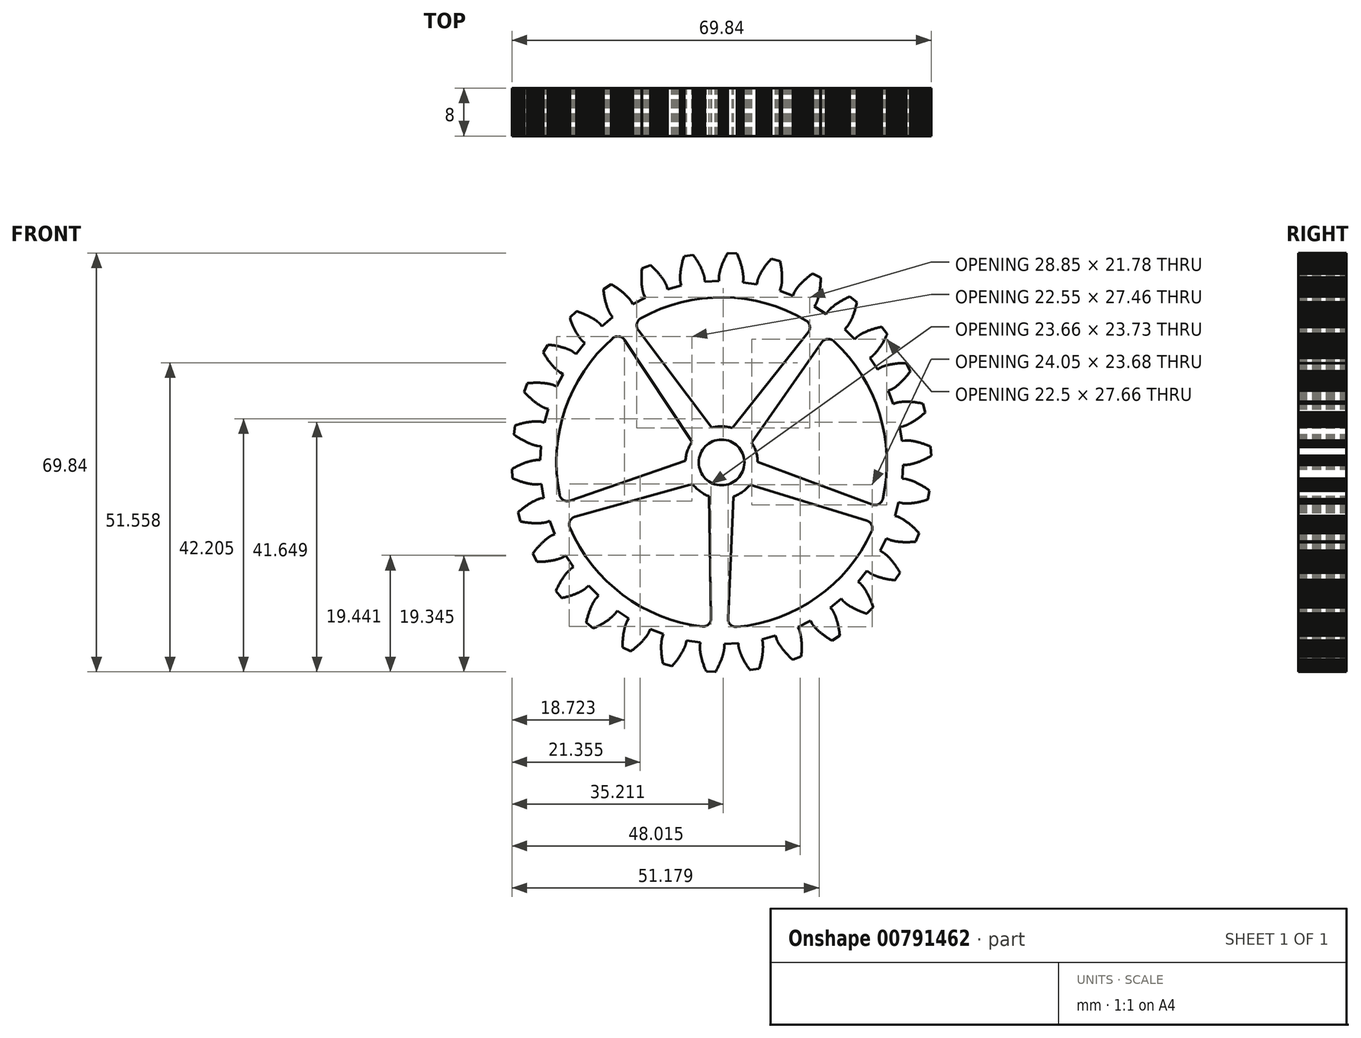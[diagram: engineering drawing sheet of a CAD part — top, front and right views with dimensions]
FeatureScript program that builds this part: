
annotation { "Feature Type Name" : "Feature", "Feature Type Description" : "" }
export const myFeature = defineFeature(function(context is Context, id is Id, definition is map)
    precondition{}
    {
        {
            var Q0;
            Q0=qCreatedBy(makeId("Front.planeOp"),FACE);
            var sketch = newSketch(context, id + "F0", { "sketchPlane" : qUnion([Q0])});
            skCircle(sketch, "E0", {"center": v(0, 0) * mm, "radius": 32.75 * mm, "construction": true});
            skArc(sketch, "E1", {"start": v(26.86, -6.05) * mm, "mid": v(26.3, 8.17) * mm, "end": v(18.7, 20.2) * mm});
            skLineSegment(sketch, "E2", {"start": v(-1.73, -25.97) * mm, "end": v(-2.1, -5.63) * mm});
            skLineSegment(sketch, "E3", {"start": v(1.07, -26) * mm, "end": v(1.95, -5.68) * mm});
            skLineSegment(sketch, "E4", {"start": v(24.16, -9.67) * mm, "end": v(4.7, -3.74) * mm});
            skLineSegment(sketch, "E5", {"start": v(25.06, -7.02) * mm, "end": v(6, 0.1) * mm});
            skLineSegment(sketch, "E6", {"start": v(16.67, 20) * mm, "end": v(5, 3.32) * mm});
            skLineSegment(sketch, "E7", {"start": v(14.42, 21.67) * mm, "end": v(1.76, 5.75) * mm});
            skLineSegment(sketch, "E8", {"start": v(-13.86, 22.03) * mm, "end": v(-1.61, 5.79) * mm});
            skLineSegment(sketch, "E9", {"start": v(-16.15, 20.41) * mm, "end": v(-4.92, 3.45) * mm});
            skLineSegment(sketch, "E10", {"start": v(-25.24, -6.38) * mm, "end": v(-6, 0.26) * mm});
            skLineSegment(sketch, "E11", {"start": v(-24.4, -9.05) * mm, "end": v(-4.8, -3.61) * mm});
            skArc(sketch, "E12", {"start": v(-3.25, -27.34) * mm, "mid": v(-2.18, -27) * mm, "end": v(-1.73, -25.97) * mm});
            skArc(sketch, "E13", {"start": v(1.07, -26) * mm, "mid": v(1.49, -27.05) * mm, "end": v(2.55, -27.41) * mm});
            skArc(sketch, "E14", {"start": v(-24.4, -9.05) * mm, "mid": v(-25.26, -9.77) * mm, "end": v(-25.29, -10.9) * mm});
            skArc(sketch, "E15", {"start": v(-27, -5.36) * mm, "mid": v(-26.35, -6.27) * mm, "end": v(-25.24, -6.38) * mm});
            skArc(sketch, "E16", {"start": v(-16.15, 20.41) * mm, "mid": v(-17.1, 21) * mm, "end": v(-18.17, 20.68) * mm});
            skArc(sketch, "E17", {"start": v(-13.44, 24.03) * mm, "mid": v(-14.1, 23.12) * mm, "end": v(-13.86, 22.03) * mm});
            skArc(sketch, "E18", {"start": v(14.42, 21.67) * mm, "mid": v(14.7, 22.75) * mm, "end": v(14.05, 23.67) * mm});
            skArc(sketch, "E19", {"start": v(18.7, 20.2) * mm, "mid": v(17.63, 20.56) * mm, "end": v(16.67, 20) * mm});
            skArc(sketch, "E20", {"start": v(25.06, -7.02) * mm, "mid": v(26.18, -6.94) * mm, "end": v(26.86, -6.05) * mm});
            skArc(sketch, "E21", {"start": v(25, -11.54) * mm, "mid": v(25, -10.42) * mm, "end": v(24.16, -9.67) * mm});
            skArc(sketch, "E22", {"start": v(2.55, -27.41) * mm, "mid": v(15.9, -22.48) * mm, "end": v(25, -11.54) * mm});
            skArc(sketch, "E23", {"start": v(-25.29, -10.9) * mm, "mid": v(-16.47, -22.06) * mm, "end": v(-3.25, -27.34) * mm});
            skArc(sketch, "E24", {"start": v(-18.17, 20.68) * mm, "mid": v(-26.07, 8.84) * mm, "end": v(-27, -5.36) * mm});
            skArc(sketch, "E25", {"start": v(14.05, 23.67) * mm, "mid": v(0.35, 27.53) * mm, "end": v(-13.44, 24.03) * mm});
            skCircle(sketch, "E26", {"center": v(0, 0) * mm, "radius": 3.8 * mm});
            skLineSegment(sketch, "E27", {"start": v(-30.24, 0.39) * mm, "end": v(-30.78, 0.4) * mm});
            skLineSegment(sketch, "E28", {"start": v(-30.78, 0.4) * mm, "end": v(-30.79, 0.4) * mm});
            skLineSegment(sketch, "E29", {"start": v(-30.79, 0.4) * mm, "end": v(-30.8, 0.4) * mm});
            skLineSegment(sketch, "E30", {"start": v(-30.8, 0.4) * mm, "end": v(-30.81, 0.4) * mm});
            skLineSegment(sketch, "E31", {"start": v(-30.81, 0.4) * mm, "end": v(-30.84, 0.4) * mm});
            skLineSegment(sketch, "E32", {"start": v(-30.84, 0.4) * mm, "end": v(-30.86, 0.4) * mm});
            skLineSegment(sketch, "E33", {"start": v(-30.86, 0.4) * mm, "end": v(-30.89, 0.39) * mm});
            skLineSegment(sketch, "E34", {"start": v(-30.89, 0.39) * mm, "end": v(-30.92, 0.39) * mm});
            skLineSegment(sketch, "E35", {"start": v(-30.92, 0.39) * mm, "end": v(-30.96, 0.38) * mm});
            skLineSegment(sketch, "E36", {"start": v(-30.96, 0.38) * mm, "end": v(-31, 0.38) * mm});
            skLineSegment(sketch, "E37", {"start": v(-31, 0.38) * mm, "end": v(-31.05, 0.37) * mm});
            skLineSegment(sketch, "E38", {"start": v(-31.05, 0.37) * mm, "end": v(-31.1, 0.37) * mm});
            skLineSegment(sketch, "E39", {"start": v(-31.1, 0.37) * mm, "end": v(-31.15, 0.36) * mm});
            skLineSegment(sketch, "E40", {"start": v(-31.15, 0.36) * mm, "end": v(-31.2, 0.35) * mm});
            skLineSegment(sketch, "E41", {"start": v(-31.2, 0.35) * mm, "end": v(-31.27, 0.34) * mm});
            skLineSegment(sketch, "E42", {"start": v(-31.27, 0.34) * mm, "end": v(-31.34, 0.33) * mm});
            skLineSegment(sketch, "E43", {"start": v(-31.34, 0.33) * mm, "end": v(-31.4, 0.32) * mm});
            skLineSegment(sketch, "E44", {"start": v(-31.4, 0.32) * mm, "end": v(-31.48, 0.3) * mm});
            skLineSegment(sketch, "E45", {"start": v(-31.48, 0.3) * mm, "end": v(-31.56, 0.29) * mm});
            skLineSegment(sketch, "E46", {"start": v(-31.56, 0.29) * mm, "end": v(-31.64, 0.27) * mm});
            skLineSegment(sketch, "E47", {"start": v(-31.64, 0.27) * mm, "end": v(-31.72, 0.25) * mm});
            skLineSegment(sketch, "E48", {"start": v(-31.72, 0.25) * mm, "end": v(-31.81, 0.23) * mm});
            skLineSegment(sketch, "E49", {"start": v(-31.81, 0.23) * mm, "end": v(-31.9, 0.2) * mm});
            skLineSegment(sketch, "E50", {"start": v(-31.9, 0.2) * mm, "end": v(-32, 0.17) * mm});
            skLineSegment(sketch, "E51", {"start": v(-32, 0.17) * mm, "end": v(-32.1, 0.15) * mm});
            skLineSegment(sketch, "E52", {"start": v(-32.1, 0.15) * mm, "end": v(-32.2, 0.12) * mm});
            skLineSegment(sketch, "E53", {"start": v(-32.2, 0.12) * mm, "end": v(-32.31, 0.08) * mm});
            skLineSegment(sketch, "E54", {"start": v(-32.31, 0.08) * mm, "end": v(-32.42, 0.05) * mm});
            skLineSegment(sketch, "E55", {"start": v(-32.42, 0.05) * mm, "end": v(-32.54, 0) * mm});
            skLineSegment(sketch, "E56", {"start": v(-32.54, 0) * mm, "end": v(-32.66, -0.03) * mm});
            skLineSegment(sketch, "E57", {"start": v(-32.66, -0.03) * mm, "end": v(-32.78, -0.08) * mm});
            skLineSegment(sketch, "E58", {"start": v(-32.78, -0.08) * mm, "end": v(-32.9, -0.12) * mm});
            skLineSegment(sketch, "E59", {"start": v(-32.9, -0.12) * mm, "end": v(-33.03, -0.17) * mm});
            skLineSegment(sketch, "E60", {"start": v(-33.03, -0.17) * mm, "end": v(-33.16, -0.23) * mm});
            skLineSegment(sketch, "E61", {"start": v(-33.16, -0.23) * mm, "end": v(-33.3, -0.28) * mm});
            skLineSegment(sketch, "E62", {"start": v(-33.3, -0.28) * mm, "end": v(-33.43, -0.34) * mm});
            skLineSegment(sketch, "E63", {"start": v(-33.43, -0.34) * mm, "end": v(-33.57, -0.4) * mm});
            skLineSegment(sketch, "E64", {"start": v(-33.57, -0.4) * mm, "end": v(-33.72, -0.47) * mm});
            skLineSegment(sketch, "E65", {"start": v(-33.72, -0.47) * mm, "end": v(-33.87, -0.54) * mm});
            skLineSegment(sketch, "E66", {"start": v(-33.87, -0.54) * mm, "end": v(-34.02, -0.61) * mm});
            skLineSegment(sketch, "E67", {"start": v(-34.02, -0.61) * mm, "end": v(-34.17, -0.7) * mm});
            skLineSegment(sketch, "E68", {"start": v(-34.17, -0.7) * mm, "end": v(-34.32, -0.77) * mm});
            skLineSegment(sketch, "E69", {"start": v(-34.32, -0.77) * mm, "end": v(-34.48, -0.85) * mm});
            skLineSegment(sketch, "E70", {"start": v(-34.48, -0.85) * mm, "end": v(-34.64, -0.94) * mm});
            skLineSegment(sketch, "E71", {"start": v(-34.64, -0.94) * mm, "end": v(-34.8, -1.03) * mm});
            skLineSegment(sketch, "E72", {"start": v(-34.8, -1.03) * mm, "end": v(-34.92, -1.13) * mm});
            skLineSegment(sketch, "E73", {"start": v(-34.92, -1.13) * mm, "end": v(-34.84, -2.6) * mm});
            skLineSegment(sketch, "E74", {"start": v(-34.84, -2.6) * mm, "end": v(-34.72, -2.68) * mm});
            skLineSegment(sketch, "E75", {"start": v(-34.72, -2.68) * mm, "end": v(-34.55, -2.76) * mm});
            skLineSegment(sketch, "E76", {"start": v(-34.55, -2.76) * mm, "end": v(-34.38, -2.83) * mm});
            skLineSegment(sketch, "E77", {"start": v(-34.38, -2.83) * mm, "end": v(-34.21, -2.9) * mm});
            skLineSegment(sketch, "E78", {"start": v(-34.21, -2.9) * mm, "end": v(-34.05, -2.96) * mm});
            skLineSegment(sketch, "E79", {"start": v(-34.05, -2.96) * mm, "end": v(-33.89, -3.02) * mm});
            skLineSegment(sketch, "E80", {"start": v(-33.89, -3.02) * mm, "end": v(-33.73, -3.07) * mm});
            skLineSegment(sketch, "E81", {"start": v(-33.73, -3.07) * mm, "end": v(-33.58, -3.13) * mm});
            skLineSegment(sketch, "E82", {"start": v(-33.58, -3.13) * mm, "end": v(-33.43, -3.18) * mm});
            skLineSegment(sketch, "E83", {"start": v(-33.43, -3.18) * mm, "end": v(-33.28, -3.22) * mm});
            skLineSegment(sketch, "E84", {"start": v(-33.28, -3.22) * mm, "end": v(-33.14, -3.27) * mm});
            skLineSegment(sketch, "E85", {"start": v(-33.14, -3.27) * mm, "end": v(-33, -3.3) * mm});
            skLineSegment(sketch, "E86", {"start": v(-33, -3.3) * mm, "end": v(-32.86, -3.35) * mm});
            skLineSegment(sketch, "E87", {"start": v(-32.86, -3.35) * mm, "end": v(-32.73, -3.38) * mm});
            skLineSegment(sketch, "E88", {"start": v(-32.73, -3.38) * mm, "end": v(-32.6, -3.42) * mm});
            skLineSegment(sketch, "E89", {"start": v(-32.6, -3.42) * mm, "end": v(-32.47, -3.45) * mm});
            skLineSegment(sketch, "E90", {"start": v(-32.47, -3.45) * mm, "end": v(-32.35, -3.48) * mm});
            skLineSegment(sketch, "E91", {"start": v(-32.35, -3.48) * mm, "end": v(-32.23, -3.5) * mm});
            skLineSegment(sketch, "E92", {"start": v(-32.23, -3.5) * mm, "end": v(-32.12, -3.53) * mm});
            skLineSegment(sketch, "E93", {"start": v(-32.12, -3.53) * mm, "end": v(-32, -3.55) * mm});
            skLineSegment(sketch, "E94", {"start": v(-32, -3.55) * mm, "end": v(-31.9, -3.57) * mm});
            skLineSegment(sketch, "E95", {"start": v(-31.9, -3.57) * mm, "end": v(-31.8, -3.58) * mm});
            skLineSegment(sketch, "E96", {"start": v(-31.8, -3.58) * mm, "end": v(-31.7, -3.6) * mm});
            skLineSegment(sketch, "E97", {"start": v(-31.7, -3.6) * mm, "end": v(-31.6, -3.61) * mm});
            skLineSegment(sketch, "E98", {"start": v(-31.6, -3.61) * mm, "end": v(-31.52, -3.63) * mm});
            skLineSegment(sketch, "E99", {"start": v(-31.52, -3.63) * mm, "end": v(-31.43, -3.64) * mm});
            skLineSegment(sketch, "E100", {"start": v(-31.43, -3.64) * mm, "end": v(-31.35, -3.65) * mm});
            skLineSegment(sketch, "E101", {"start": v(-31.35, -3.65) * mm, "end": v(-31.27, -3.66) * mm});
            skLineSegment(sketch, "E102", {"start": v(-31.27, -3.66) * mm, "end": v(-31.2, -3.66) * mm});
            skLineSegment(sketch, "E103", {"start": v(-31.2, -3.66) * mm, "end": v(-31.12, -3.67) * mm});
            skLineSegment(sketch, "E104", {"start": v(-31.12, -3.67) * mm, "end": v(-31.06, -3.67) * mm});
            skLineSegment(sketch, "E105", {"start": v(-31.06, -3.67) * mm, "end": v(-31, -3.68) * mm});
            skLineSegment(sketch, "E106", {"start": v(-31, -3.68) * mm, "end": v(-30.93, -3.68) * mm});
            skLineSegment(sketch, "E107", {"start": v(-30.93, -3.68) * mm, "end": v(-30.88, -3.68) * mm});
            skLineSegment(sketch, "E108", {"start": v(-30.88, -3.68) * mm, "end": v(-30.83, -3.68) * mm});
            skLineSegment(sketch, "E109", {"start": v(-30.83, -3.68) * mm, "end": v(-30.78, -3.68) * mm});
            skLineSegment(sketch, "E110", {"start": v(-30.78, -3.68) * mm, "end": v(-30.74, -3.68) * mm});
            skLineSegment(sketch, "E111", {"start": v(-30.74, -3.68) * mm, "end": v(-30.7, -3.68) * mm});
            skLineSegment(sketch, "E112", {"start": v(-30.7, -3.68) * mm, "end": v(-30.67, -3.68) * mm});
            skLineSegment(sketch, "E113", {"start": v(-30.67, -3.68) * mm, "end": v(-30.64, -3.68) * mm});
            skLineSegment(sketch, "E114", {"start": v(-30.64, -3.68) * mm, "end": v(-30.62, -3.68) * mm});
            skLineSegment(sketch, "E115", {"start": v(-30.62, -3.68) * mm, "end": v(-30.6, -3.68) * mm});
            skLineSegment(sketch, "E116", {"start": v(-30.6, -3.68) * mm, "end": v(-30.58, -3.68) * mm});
            skLineSegment(sketch, "E117", {"start": v(-30.58, -3.68) * mm, "end": v(-30.57, -3.67) * mm});
            skLineSegment(sketch, "E118", {"start": v(-30.57, -3.67) * mm, "end": v(-30.56, -3.67) * mm});
            skLineSegment(sketch, "E119", {"start": v(-30.56, -3.67) * mm, "end": v(-30.02, -3.6) * mm});
            skLineSegment(sketch, "E120", {"start": v(-30.02, -3.6) * mm, "end": v(-29.66, -5.9) * mm});
            skLineSegment(sketch, "E121", {"start": v(-29.66, -5.9) * mm, "end": v(-30.19, -6.01) * mm});
            skLineSegment(sketch, "E122", {"start": v(-30.19, -6.01) * mm, "end": v(-30.2, -6.01) * mm});
            skLineSegment(sketch, "E123", {"start": v(-30.2, -6.01) * mm, "end": v(-30.2, -6.02) * mm});
            skLineSegment(sketch, "E124", {"start": v(-30.2, -6.02) * mm, "end": v(-30.22, -6.02) * mm});
            skLineSegment(sketch, "E125", {"start": v(-30.22, -6.02) * mm, "end": v(-30.24, -6.03) * mm});
            skLineSegment(sketch, "E126", {"start": v(-30.24, -6.03) * mm, "end": v(-30.27, -6.03) * mm});
            skLineSegment(sketch, "E127", {"start": v(-30.27, -6.03) * mm, "end": v(-30.3, -6.04) * mm});
            skLineSegment(sketch, "E128", {"start": v(-30.3, -6.04) * mm, "end": v(-30.33, -6.05) * mm});
            skLineSegment(sketch, "E129", {"start": v(-30.33, -6.05) * mm, "end": v(-30.36, -6.06) * mm});
            skLineSegment(sketch, "E130", {"start": v(-30.36, -6.06) * mm, "end": v(-30.4, -6.07) * mm});
            skLineSegment(sketch, "E131", {"start": v(-30.4, -6.07) * mm, "end": v(-30.45, -6.09) * mm});
            skLineSegment(sketch, "E132", {"start": v(-30.45, -6.09) * mm, "end": v(-30.5, -6.1) * mm});
            skLineSegment(sketch, "E133", {"start": v(-30.5, -6.1) * mm, "end": v(-30.54, -6.12) * mm});
            skLineSegment(sketch, "E134", {"start": v(-30.54, -6.12) * mm, "end": v(-30.6, -6.15) * mm});
            skLineSegment(sketch, "E135", {"start": v(-30.6, -6.15) * mm, "end": v(-30.66, -6.17) * mm});
            skLineSegment(sketch, "E136", {"start": v(-30.66, -6.17) * mm, "end": v(-30.72, -6.2) * mm});
            skLineSegment(sketch, "E137", {"start": v(-30.72, -6.2) * mm, "end": v(-30.78, -6.22) * mm});
            skLineSegment(sketch, "E138", {"start": v(-30.78, -6.22) * mm, "end": v(-30.85, -6.25) * mm});
            skLineSegment(sketch, "E139", {"start": v(-30.85, -6.25) * mm, "end": v(-30.93, -6.28) * mm});
            skLineSegment(sketch, "E140", {"start": v(-30.93, -6.28) * mm, "end": v(-31, -6.32) * mm});
            skLineSegment(sketch, "E141", {"start": v(-31, -6.32) * mm, "end": v(-31.08, -6.35) * mm});
            skLineSegment(sketch, "E142", {"start": v(-31.08, -6.35) * mm, "end": v(-31.16, -6.4) * mm});
            skLineSegment(sketch, "E143", {"start": v(-31.16, -6.4) * mm, "end": v(-31.25, -6.44) * mm});
            skLineSegment(sketch, "E144", {"start": v(-31.25, -6.44) * mm, "end": v(-31.34, -6.48) * mm});
            skLineSegment(sketch, "E145", {"start": v(-31.34, -6.48) * mm, "end": v(-31.43, -6.53) * mm});
            skLineSegment(sketch, "E146", {"start": v(-31.43, -6.53) * mm, "end": v(-31.52, -6.58) * mm});
            skLineSegment(sketch, "E147", {"start": v(-31.52, -6.58) * mm, "end": v(-31.62, -6.64) * mm});
            skLineSegment(sketch, "E148", {"start": v(-31.62, -6.64) * mm, "end": v(-31.72, -6.7) * mm});
            skLineSegment(sketch, "E149", {"start": v(-31.72, -6.7) * mm, "end": v(-31.83, -6.76) * mm});
            skLineSegment(sketch, "E150", {"start": v(-31.83, -6.76) * mm, "end": v(-31.93, -6.82) * mm});
            skLineSegment(sketch, "E151", {"start": v(-31.93, -6.82) * mm, "end": v(-32.04, -6.9) * mm});
            skLineSegment(sketch, "E152", {"start": v(-32.04, -6.9) * mm, "end": v(-32.16, -6.96) * mm});
            skLineSegment(sketch, "E153", {"start": v(-32.16, -6.96) * mm, "end": v(-32.27, -7.04) * mm});
            skLineSegment(sketch, "E154", {"start": v(-32.27, -7.04) * mm, "end": v(-32.39, -7.12) * mm});
            skLineSegment(sketch, "E155", {"start": v(-32.39, -7.12) * mm, "end": v(-32.5, -7.2) * mm});
            skLineSegment(sketch, "E156", {"start": v(-32.5, -7.2) * mm, "end": v(-32.63, -7.29) * mm});
            skLineSegment(sketch, "E157", {"start": v(-32.63, -7.29) * mm, "end": v(-32.76, -7.38) * mm});
            skLineSegment(sketch, "E158", {"start": v(-32.76, -7.38) * mm, "end": v(-32.88, -7.47) * mm});
            skLineSegment(sketch, "E159", {"start": v(-32.88, -7.47) * mm, "end": v(-33.01, -7.57) * mm});
            skLineSegment(sketch, "E160", {"start": v(-33.01, -7.57) * mm, "end": v(-33.14, -7.67) * mm});
            skLineSegment(sketch, "E161", {"start": v(-33.14, -7.67) * mm, "end": v(-33.28, -7.78) * mm});
            skLineSegment(sketch, "E162", {"start": v(-33.28, -7.78) * mm, "end": v(-33.41, -7.89) * mm});
            skLineSegment(sketch, "E163", {"start": v(-33.41, -7.89) * mm, "end": v(-33.55, -8) * mm});
            skLineSegment(sketch, "E164", {"start": v(-33.55, -8) * mm, "end": v(-33.69, -8.12) * mm});
            skLineSegment(sketch, "E165", {"start": v(-33.69, -8.12) * mm, "end": v(-33.83, -8.25) * mm});
            skLineSegment(sketch, "E166", {"start": v(-33.83, -8.25) * mm, "end": v(-33.92, -8.36) * mm});
            skLineSegment(sketch, "E167", {"start": v(-33.92, -8.36) * mm, "end": v(-33.53, -9.79) * mm});
            skLineSegment(sketch, "E168", {"start": v(-33.53, -9.79) * mm, "end": v(-33.4, -9.84) * mm});
            skLineSegment(sketch, "E169", {"start": v(-33.4, -9.84) * mm, "end": v(-33.22, -9.88) * mm});
            skLineSegment(sketch, "E170", {"start": v(-33.22, -9.88) * mm, "end": v(-33.04, -9.91) * mm});
            skLineSegment(sketch, "E171", {"start": v(-33.04, -9.91) * mm, "end": v(-32.86, -9.94) * mm});
            skLineSegment(sketch, "E172", {"start": v(-32.86, -9.94) * mm, "end": v(-32.69, -9.97) * mm});
            skLineSegment(sketch, "E173", {"start": v(-32.69, -9.97) * mm, "end": v(-32.52, -10) * mm});
            skLineSegment(sketch, "E174", {"start": v(-32.52, -10) * mm, "end": v(-32.35, -10.02) * mm});
            skLineSegment(sketch, "E175", {"start": v(-32.35, -10.02) * mm, "end": v(-32.2, -10.04) * mm});
            skLineSegment(sketch, "E176", {"start": v(-32.2, -10.04) * mm, "end": v(-32.04, -10.06) * mm});
            skLineSegment(sketch, "E177", {"start": v(-32.04, -10.06) * mm, "end": v(-31.88, -10.07) * mm});
            skLineSegment(sketch, "E178", {"start": v(-31.88, -10.07) * mm, "end": v(-31.73, -10.09) * mm});
            skLineSegment(sketch, "E179", {"start": v(-31.73, -10.09) * mm, "end": v(-31.59, -10.1) * mm});
            skLineSegment(sketch, "E180", {"start": v(-31.59, -10.1) * mm, "end": v(-31.45, -10.1) * mm});
            skLineSegment(sketch, "E181", {"start": v(-31.45, -10.1) * mm, "end": v(-31.3, -10.11) * mm});
            skLineSegment(sketch, "E182", {"start": v(-31.3, -10.11) * mm, "end": v(-31.18, -10.12) * mm});
            skLineSegment(sketch, "E183", {"start": v(-31.18, -10.12) * mm, "end": v(-31.05, -10.12) * mm});
            skLineSegment(sketch, "E184", {"start": v(-31.05, -10.12) * mm, "end": v(-30.92, -10.13) * mm});
            skLineSegment(sketch, "E185", {"start": v(-30.92, -10.13) * mm, "end": v(-30.8, -10.13) * mm});
            skLineSegment(sketch, "E186", {"start": v(-30.8, -10.13) * mm, "end": v(-30.68, -10.13) * mm});
            skLineSegment(sketch, "E187", {"start": v(-30.68, -10.13) * mm, "end": v(-30.57, -10.12) * mm});
            skLineSegment(sketch, "E188", {"start": v(-30.57, -10.12) * mm, "end": v(-30.46, -10.12) * mm});
            skLineSegment(sketch, "E189", {"start": v(-30.46, -10.12) * mm, "end": v(-30.36, -10.12) * mm});
            skLineSegment(sketch, "E190", {"start": v(-30.36, -10.12) * mm, "end": v(-30.26, -10.11) * mm});
            skLineSegment(sketch, "E191", {"start": v(-30.26, -10.11) * mm, "end": v(-30.16, -10.1) * mm});
            skLineSegment(sketch, "E192", {"start": v(-30.16, -10.1) * mm, "end": v(-30.07, -10.1) * mm});
            skLineSegment(sketch, "E193", {"start": v(-30.07, -10.1) * mm, "end": v(-29.99, -10.1) * mm});
            skLineSegment(sketch, "E194", {"start": v(-29.99, -10.1) * mm, "end": v(-29.9, -10.09) * mm});
            skLineSegment(sketch, "E195", {"start": v(-29.9, -10.09) * mm, "end": v(-29.82, -10.08) * mm});
            skLineSegment(sketch, "E196", {"start": v(-29.82, -10.08) * mm, "end": v(-29.75, -10.07) * mm});
            skLineSegment(sketch, "E197", {"start": v(-29.75, -10.07) * mm, "end": v(-29.68, -10.06) * mm});
            skLineSegment(sketch, "E198", {"start": v(-29.68, -10.06) * mm, "end": v(-29.61, -10.05) * mm});
            skLineSegment(sketch, "E199", {"start": v(-29.61, -10.05) * mm, "end": v(-29.55, -10.04) * mm});
            skLineSegment(sketch, "E200", {"start": v(-29.55, -10.04) * mm, "end": v(-29.5, -10.03) * mm});
            skLineSegment(sketch, "E201", {"start": v(-29.5, -10.03) * mm, "end": v(-29.44, -10.02) * mm});
            skLineSegment(sketch, "E202", {"start": v(-29.44, -10.02) * mm, "end": v(-29.4, -10.01) * mm});
            skLineSegment(sketch, "E203", {"start": v(-29.4, -10.01) * mm, "end": v(-29.35, -10) * mm});
            skLineSegment(sketch, "E204", {"start": v(-29.35, -10) * mm, "end": v(-29.3, -10) * mm});
            skLineSegment(sketch, "E205", {"start": v(-29.3, -10) * mm, "end": v(-29.27, -9.98) * mm});
            skLineSegment(sketch, "E206", {"start": v(-29.27, -9.98) * mm, "end": v(-29.24, -9.98) * mm});
            skLineSegment(sketch, "E207", {"start": v(-29.24, -9.98) * mm, "end": v(-29.2, -9.97) * mm});
            skLineSegment(sketch, "E208", {"start": v(-29.2, -9.97) * mm, "end": v(-29.18, -9.96) * mm});
            skLineSegment(sketch, "E209", {"start": v(-29.18, -9.96) * mm, "end": v(-29.16, -9.96) * mm});
            skLineSegment(sketch, "E210", {"start": v(-29.16, -9.96) * mm, "end": v(-29.15, -9.95) * mm});
            skLineSegment(sketch, "E211", {"start": v(-29.15, -9.95) * mm, "end": v(-29.14, -9.95) * mm});
            skLineSegment(sketch, "E212", {"start": v(-29.14, -9.95) * mm, "end": v(-29.13, -9.95) * mm});
            skLineSegment(sketch, "E213", {"start": v(-29.13, -9.95) * mm, "end": v(-28.62, -9.77) * mm});
            skLineSegment(sketch, "E214", {"start": v(-28.62, -9.77) * mm, "end": v(-27.78, -11.94) * mm});
            skLineSegment(sketch, "E215", {"start": v(-27.78, -11.94) * mm, "end": v(-28.28, -12.16) * mm});
            skLineSegment(sketch, "E216", {"start": v(-28.28, -12.16) * mm, "end": v(-28.28, -12.16) * mm});
            skLineSegment(sketch, "E217", {"start": v(-28.28, -12.16) * mm, "end": v(-28.3, -12.17) * mm});
            skLineSegment(sketch, "E218", {"start": v(-28.3, -12.17) * mm, "end": v(-28.31, -12.17) * mm});
            skLineSegment(sketch, "E219", {"start": v(-28.31, -12.17) * mm, "end": v(-28.33, -12.18) * mm});
            skLineSegment(sketch, "E220", {"start": v(-28.33, -12.18) * mm, "end": v(-28.35, -12.2) * mm});
            skLineSegment(sketch, "E221", {"start": v(-28.35, -12.2) * mm, "end": v(-28.38, -12.2) * mm});
            skLineSegment(sketch, "E222", {"start": v(-28.38, -12.2) * mm, "end": v(-28.4, -12.22) * mm});
            skLineSegment(sketch, "E223", {"start": v(-28.4, -12.22) * mm, "end": v(-28.44, -12.24) * mm});
            skLineSegment(sketch, "E224", {"start": v(-28.44, -12.24) * mm, "end": v(-28.48, -12.26) * mm});
            skLineSegment(sketch, "E225", {"start": v(-28.48, -12.26) * mm, "end": v(-28.51, -12.29) * mm});
            skLineSegment(sketch, "E226", {"start": v(-28.51, -12.29) * mm, "end": v(-28.56, -12.31) * mm});
            skLineSegment(sketch, "E227", {"start": v(-28.56, -12.31) * mm, "end": v(-28.6, -12.34) * mm});
            skLineSegment(sketch, "E228", {"start": v(-28.6, -12.34) * mm, "end": v(-28.65, -12.37) * mm});
            skLineSegment(sketch, "E229", {"start": v(-28.65, -12.37) * mm, "end": v(-28.7, -12.4) * mm});
            skLineSegment(sketch, "E230", {"start": v(-28.7, -12.4) * mm, "end": v(-28.76, -12.44) * mm});
            skLineSegment(sketch, "E231", {"start": v(-28.76, -12.44) * mm, "end": v(-28.82, -12.48) * mm});
            skLineSegment(sketch, "E232", {"start": v(-28.82, -12.48) * mm, "end": v(-28.88, -12.53) * mm});
            skLineSegment(sketch, "E233", {"start": v(-28.88, -12.53) * mm, "end": v(-28.94, -12.57) * mm});
            skLineSegment(sketch, "E234", {"start": v(-28.94, -12.57) * mm, "end": v(-29.01, -12.62) * mm});
            skLineSegment(sketch, "E235", {"start": v(-29.01, -12.62) * mm, "end": v(-29.08, -12.68) * mm});
            skLineSegment(sketch, "E236", {"start": v(-29.08, -12.68) * mm, "end": v(-29.15, -12.73) * mm});
            skLineSegment(sketch, "E237", {"start": v(-29.15, -12.73) * mm, "end": v(-29.23, -12.8) * mm});
            skLineSegment(sketch, "E238", {"start": v(-29.23, -12.8) * mm, "end": v(-29.3, -12.86) * mm});
            skLineSegment(sketch, "E239", {"start": v(-29.3, -12.86) * mm, "end": v(-29.38, -12.92) * mm});
            skLineSegment(sketch, "E240", {"start": v(-29.38, -12.92) * mm, "end": v(-29.47, -13) * mm});
            skLineSegment(sketch, "E241", {"start": v(-29.47, -13) * mm, "end": v(-29.55, -13.07) * mm});
            skLineSegment(sketch, "E242", {"start": v(-29.55, -13.07) * mm, "end": v(-29.64, -13.15) * mm});
            skLineSegment(sketch, "E243", {"start": v(-29.64, -13.15) * mm, "end": v(-29.73, -13.23) * mm});
            skLineSegment(sketch, "E244", {"start": v(-29.73, -13.23) * mm, "end": v(-29.82, -13.31) * mm});
            skLineSegment(sketch, "E245", {"start": v(-29.82, -13.31) * mm, "end": v(-29.91, -13.4) * mm});
            skLineSegment(sketch, "E246", {"start": v(-29.91, -13.4) * mm, "end": v(-30, -13.5) * mm});
            skLineSegment(sketch, "E247", {"start": v(-30, -13.5) * mm, "end": v(-30.1, -13.6) * mm});
            skLineSegment(sketch, "E248", {"start": v(-30.1, -13.6) * mm, "end": v(-30.2, -13.7) * mm});
            skLineSegment(sketch, "E249", {"start": v(-30.2, -13.7) * mm, "end": v(-30.3, -13.8) * mm});
            skLineSegment(sketch, "E250", {"start": v(-30.3, -13.8) * mm, "end": v(-30.4, -13.91) * mm});
            skLineSegment(sketch, "E251", {"start": v(-30.4, -13.91) * mm, "end": v(-30.5, -14.03) * mm});
            skLineSegment(sketch, "E252", {"start": v(-30.5, -14.03) * mm, "end": v(-30.61, -14.15) * mm});
            skLineSegment(sketch, "E253", {"start": v(-30.61, -14.15) * mm, "end": v(-30.72, -14.27) * mm});
            skLineSegment(sketch, "E254", {"start": v(-30.72, -14.27) * mm, "end": v(-30.82, -14.4) * mm});
            skLineSegment(sketch, "E255", {"start": v(-30.82, -14.4) * mm, "end": v(-30.93, -14.53) * mm});
            skLineSegment(sketch, "E256", {"start": v(-30.93, -14.53) * mm, "end": v(-31.04, -14.66) * mm});
            skLineSegment(sketch, "E257", {"start": v(-31.04, -14.66) * mm, "end": v(-31.15, -14.8) * mm});
            skLineSegment(sketch, "E258", {"start": v(-31.15, -14.8) * mm, "end": v(-31.26, -14.95) * mm});
            skLineSegment(sketch, "E259", {"start": v(-31.26, -14.95) * mm, "end": v(-31.38, -15.1) * mm});
            skLineSegment(sketch, "E260", {"start": v(-31.38, -15.1) * mm, "end": v(-31.44, -15.23) * mm});
            skLineSegment(sketch, "E261", {"start": v(-31.44, -15.23) * mm, "end": v(-30.77, -16.55) * mm});
            skLineSegment(sketch, "E262", {"start": v(-30.77, -16.55) * mm, "end": v(-30.63, -16.57) * mm});
            skLineSegment(sketch, "E263", {"start": v(-30.63, -16.57) * mm, "end": v(-30.44, -16.57) * mm});
            skLineSegment(sketch, "E264", {"start": v(-30.44, -16.57) * mm, "end": v(-30.25, -16.56) * mm});
            skLineSegment(sketch, "E265", {"start": v(-30.25, -16.56) * mm, "end": v(-30.08, -16.56) * mm});
            skLineSegment(sketch, "E266", {"start": v(-30.08, -16.56) * mm, "end": v(-29.9, -16.55) * mm});
            skLineSegment(sketch, "E267", {"start": v(-29.9, -16.55) * mm, "end": v(-29.73, -16.54) * mm});
            skLineSegment(sketch, "E268", {"start": v(-29.73, -16.54) * mm, "end": v(-29.56, -16.53) * mm});
            skLineSegment(sketch, "E269", {"start": v(-29.56, -16.53) * mm, "end": v(-29.4, -16.51) * mm});
            skLineSegment(sketch, "E270", {"start": v(-29.4, -16.51) * mm, "end": v(-29.24, -16.5) * mm});
            skLineSegment(sketch, "E271", {"start": v(-29.24, -16.5) * mm, "end": v(-29.1, -16.48) * mm});
            skLineSegment(sketch, "E272", {"start": v(-29.1, -16.48) * mm, "end": v(-28.94, -16.46) * mm});
            skLineSegment(sketch, "E273", {"start": v(-28.94, -16.46) * mm, "end": v(-28.8, -16.44) * mm});
            skLineSegment(sketch, "E274", {"start": v(-28.8, -16.44) * mm, "end": v(-28.66, -16.42) * mm});
            skLineSegment(sketch, "E275", {"start": v(-28.66, -16.42) * mm, "end": v(-28.52, -16.4) * mm});
            skLineSegment(sketch, "E276", {"start": v(-28.52, -16.4) * mm, "end": v(-28.4, -16.38) * mm});
            skLineSegment(sketch, "E277", {"start": v(-28.4, -16.38) * mm, "end": v(-28.26, -16.36) * mm});
            skLineSegment(sketch, "E278", {"start": v(-28.26, -16.36) * mm, "end": v(-28.14, -16.33) * mm});
            skLineSegment(sketch, "E279", {"start": v(-28.14, -16.33) * mm, "end": v(-28.02, -16.3) * mm});
            skLineSegment(sketch, "E280", {"start": v(-28.02, -16.3) * mm, "end": v(-27.9, -16.28) * mm});
            skLineSegment(sketch, "E281", {"start": v(-27.9, -16.28) * mm, "end": v(-27.8, -16.26) * mm});
            skLineSegment(sketch, "E282", {"start": v(-27.8, -16.26) * mm, "end": v(-27.7, -16.23) * mm});
            skLineSegment(sketch, "E283", {"start": v(-27.7, -16.23) * mm, "end": v(-27.6, -16.2) * mm});
            skLineSegment(sketch, "E284", {"start": v(-27.6, -16.2) * mm, "end": v(-27.5, -16.18) * mm});
            skLineSegment(sketch, "E285", {"start": v(-27.5, -16.18) * mm, "end": v(-27.4, -16.16) * mm});
            skLineSegment(sketch, "E286", {"start": v(-27.4, -16.16) * mm, "end": v(-27.32, -16.13) * mm});
            skLineSegment(sketch, "E287", {"start": v(-27.32, -16.13) * mm, "end": v(-27.23, -16.1) * mm});
            skLineSegment(sketch, "E288", {"start": v(-27.23, -16.1) * mm, "end": v(-27.15, -16.08) * mm});
            skLineSegment(sketch, "E289", {"start": v(-27.15, -16.08) * mm, "end": v(-27.08, -16.06) * mm});
            skLineSegment(sketch, "E290", {"start": v(-27.08, -16.06) * mm, "end": v(-27, -16.03) * mm});
            skLineSegment(sketch, "E291", {"start": v(-27, -16.03) * mm, "end": v(-26.94, -16) * mm});
            skLineSegment(sketch, "E292", {"start": v(-26.94, -16) * mm, "end": v(-26.88, -15.99) * mm});
            skLineSegment(sketch, "E293", {"start": v(-26.88, -15.99) * mm, "end": v(-26.82, -15.96) * mm});
            skLineSegment(sketch, "E294", {"start": v(-26.82, -15.96) * mm, "end": v(-26.76, -15.94) * mm});
            skLineSegment(sketch, "E295", {"start": v(-26.76, -15.94) * mm, "end": v(-26.71, -15.92) * mm});
            skLineSegment(sketch, "E296", {"start": v(-26.71, -15.92) * mm, "end": v(-26.67, -15.9) * mm});
            skLineSegment(sketch, "E297", {"start": v(-26.67, -15.9) * mm, "end": v(-26.63, -15.88) * mm});
            skLineSegment(sketch, "E298", {"start": v(-26.63, -15.88) * mm, "end": v(-26.59, -15.87) * mm});
            skLineSegment(sketch, "E299", {"start": v(-26.59, -15.87) * mm, "end": v(-26.55, -15.85) * mm});
            skLineSegment(sketch, "E300", {"start": v(-26.55, -15.85) * mm, "end": v(-26.52, -15.84) * mm});
            skLineSegment(sketch, "E301", {"start": v(-26.52, -15.84) * mm, "end": v(-26.5, -15.82) * mm});
            skLineSegment(sketch, "E302", {"start": v(-26.5, -15.82) * mm, "end": v(-26.47, -15.81) * mm});
            skLineSegment(sketch, "E303", {"start": v(-26.47, -15.81) * mm, "end": v(-26.46, -15.8) * mm});
            skLineSegment(sketch, "E304", {"start": v(-26.46, -15.8) * mm, "end": v(-26.44, -15.8) * mm});
            skLineSegment(sketch, "E305", {"start": v(-26.44, -15.8) * mm, "end": v(-26.43, -15.79) * mm});
            skLineSegment(sketch, "E306", {"start": v(-26.43, -15.79) * mm, "end": v(-26.42, -15.79) * mm});
            skLineSegment(sketch, "E307", {"start": v(-26.42, -15.79) * mm, "end": v(-25.96, -15.5) * mm});
            skLineSegment(sketch, "E308", {"start": v(-25.96, -15.5) * mm, "end": v(-24.69, -17.46) * mm});
            skLineSegment(sketch, "E309", {"start": v(-24.69, -17.46) * mm, "end": v(-25.13, -17.77) * mm});
            skLineSegment(sketch, "E310", {"start": v(-25.13, -17.77) * mm, "end": v(-25.14, -17.78) * mm});
            skLineSegment(sketch, "E311", {"start": v(-25.14, -17.78) * mm, "end": v(-25.15, -17.78) * mm});
            skLineSegment(sketch, "E312", {"start": v(-25.15, -17.78) * mm, "end": v(-25.16, -17.8) * mm});
            skLineSegment(sketch, "E313", {"start": v(-25.16, -17.8) * mm, "end": v(-25.18, -17.8) * mm});
            skLineSegment(sketch, "E314", {"start": v(-25.18, -17.8) * mm, "end": v(-25.2, -17.82) * mm});
            skLineSegment(sketch, "E315", {"start": v(-25.2, -17.82) * mm, "end": v(-25.22, -17.84) * mm});
            skLineSegment(sketch, "E316", {"start": v(-25.22, -17.84) * mm, "end": v(-25.24, -17.86) * mm});
            skLineSegment(sketch, "E317", {"start": v(-25.24, -17.86) * mm, "end": v(-25.27, -17.89) * mm});
            skLineSegment(sketch, "E318", {"start": v(-25.27, -17.89) * mm, "end": v(-25.3, -17.92) * mm});
            skLineSegment(sketch, "E319", {"start": v(-25.3, -17.92) * mm, "end": v(-25.34, -17.95) * mm});
            skLineSegment(sketch, "E320", {"start": v(-25.34, -17.95) * mm, "end": v(-25.37, -17.98) * mm});
            skLineSegment(sketch, "E321", {"start": v(-25.37, -17.98) * mm, "end": v(-25.41, -18.02) * mm});
            skLineSegment(sketch, "E322", {"start": v(-25.41, -18.02) * mm, "end": v(-25.45, -18.06) * mm});
            skLineSegment(sketch, "E323", {"start": v(-25.45, -18.06) * mm, "end": v(-25.5, -18.1) * mm});
            skLineSegment(sketch, "E324", {"start": v(-25.5, -18.1) * mm, "end": v(-25.54, -18.15) * mm});
            skLineSegment(sketch, "E325", {"start": v(-25.54, -18.15) * mm, "end": v(-25.6, -18.2) * mm});
            skLineSegment(sketch, "E326", {"start": v(-25.6, -18.2) * mm, "end": v(-25.64, -18.26) * mm});
            skLineSegment(sketch, "E327", {"start": v(-25.64, -18.26) * mm, "end": v(-25.7, -18.32) * mm});
            skLineSegment(sketch, "E328", {"start": v(-25.7, -18.32) * mm, "end": v(-25.75, -18.38) * mm});
            skLineSegment(sketch, "E329", {"start": v(-25.75, -18.38) * mm, "end": v(-25.8, -18.45) * mm});
            skLineSegment(sketch, "E330", {"start": v(-25.8, -18.45) * mm, "end": v(-25.87, -18.52) * mm});
            skLineSegment(sketch, "E331", {"start": v(-25.87, -18.52) * mm, "end": v(-25.93, -18.6) * mm});
            skLineSegment(sketch, "E332", {"start": v(-25.93, -18.6) * mm, "end": v(-26, -18.67) * mm});
            skLineSegment(sketch, "E333", {"start": v(-26, -18.67) * mm, "end": v(-26.06, -18.75) * mm});
            skLineSegment(sketch, "E334", {"start": v(-26.06, -18.75) * mm, "end": v(-26.12, -18.84) * mm});
            skLineSegment(sketch, "E335", {"start": v(-26.12, -18.84) * mm, "end": v(-26.19, -18.93) * mm});
            skLineSegment(sketch, "E336", {"start": v(-26.19, -18.93) * mm, "end": v(-26.26, -19.02) * mm});
            skLineSegment(sketch, "E337", {"start": v(-26.26, -19.02) * mm, "end": v(-26.33, -19.12) * mm});
            skLineSegment(sketch, "E338", {"start": v(-26.33, -19.12) * mm, "end": v(-26.4, -19.22) * mm});
            skLineSegment(sketch, "E339", {"start": v(-26.4, -19.22) * mm, "end": v(-26.47, -19.33) * mm});
            skLineSegment(sketch, "E340", {"start": v(-26.47, -19.33) * mm, "end": v(-26.54, -19.44) * mm});
            skLineSegment(sketch, "E341", {"start": v(-26.54, -19.44) * mm, "end": v(-26.62, -19.56) * mm});
            skLineSegment(sketch, "E342", {"start": v(-26.62, -19.56) * mm, "end": v(-26.7, -19.68) * mm});
            skLineSegment(sketch, "E343", {"start": v(-26.7, -19.68) * mm, "end": v(-26.77, -19.8) * mm});
            skLineSegment(sketch, "E344", {"start": v(-26.77, -19.8) * mm, "end": v(-26.85, -19.93) * mm});
            skLineSegment(sketch, "E345", {"start": v(-26.85, -19.93) * mm, "end": v(-26.92, -20.06) * mm});
            skLineSegment(sketch, "E346", {"start": v(-26.92, -20.06) * mm, "end": v(-27, -20.2) * mm});
            skLineSegment(sketch, "E347", {"start": v(-27, -20.2) * mm, "end": v(-27.08, -20.34) * mm});
            skLineSegment(sketch, "E348", {"start": v(-27.08, -20.34) * mm, "end": v(-27.16, -20.5) * mm});
            skLineSegment(sketch, "E349", {"start": v(-27.16, -20.5) * mm, "end": v(-27.24, -20.64) * mm});
            skLineSegment(sketch, "E350", {"start": v(-27.24, -20.64) * mm, "end": v(-27.32, -20.8) * mm});
            skLineSegment(sketch, "E351", {"start": v(-27.32, -20.8) * mm, "end": v(-27.4, -20.96) * mm});
            skLineSegment(sketch, "E352", {"start": v(-27.4, -20.96) * mm, "end": v(-27.47, -21.12) * mm});
            skLineSegment(sketch, "E353", {"start": v(-27.47, -21.12) * mm, "end": v(-27.55, -21.3) * mm});
            skLineSegment(sketch, "E354", {"start": v(-27.55, -21.3) * mm, "end": v(-27.58, -21.43) * mm});
            skLineSegment(sketch, "E355", {"start": v(-27.58, -21.43) * mm, "end": v(-26.65, -22.58) * mm});
            skLineSegment(sketch, "E356", {"start": v(-26.65, -22.58) * mm, "end": v(-26.51, -22.58) * mm});
            skLineSegment(sketch, "E357", {"start": v(-26.51, -22.58) * mm, "end": v(-26.33, -22.54) * mm});
            skLineSegment(sketch, "E358", {"start": v(-26.33, -22.54) * mm, "end": v(-26.15, -22.5) * mm});
            skLineSegment(sketch, "E359", {"start": v(-26.15, -22.5) * mm, "end": v(-25.98, -22.45) * mm});
            skLineSegment(sketch, "E360", {"start": v(-25.98, -22.45) * mm, "end": v(-25.8, -22.4) * mm});
            skLineSegment(sketch, "E361", {"start": v(-25.8, -22.4) * mm, "end": v(-25.64, -22.36) * mm});
            skLineSegment(sketch, "E362", {"start": v(-25.64, -22.36) * mm, "end": v(-25.48, -22.31) * mm});
            skLineSegment(sketch, "E363", {"start": v(-25.48, -22.31) * mm, "end": v(-25.33, -22.26) * mm});
            skLineSegment(sketch, "E364", {"start": v(-25.33, -22.26) * mm, "end": v(-25.18, -22.22) * mm});
            skLineSegment(sketch, "E365", {"start": v(-25.18, -22.22) * mm, "end": v(-25.03, -22.17) * mm});
            skLineSegment(sketch, "E366", {"start": v(-25.03, -22.17) * mm, "end": v(-24.89, -22.12) * mm});
            skLineSegment(sketch, "E367", {"start": v(-24.89, -22.12) * mm, "end": v(-24.75, -22.07) * mm});
            skLineSegment(sketch, "E368", {"start": v(-24.75, -22.07) * mm, "end": v(-24.62, -22.02) * mm});
            skLineSegment(sketch, "E369", {"start": v(-24.62, -22.02) * mm, "end": v(-24.49, -21.97) * mm});
            skLineSegment(sketch, "E370", {"start": v(-24.49, -21.97) * mm, "end": v(-24.36, -21.92) * mm});
            skLineSegment(sketch, "E371", {"start": v(-24.36, -21.92) * mm, "end": v(-24.24, -21.88) * mm});
            skLineSegment(sketch, "E372", {"start": v(-24.24, -21.88) * mm, "end": v(-24.13, -21.83) * mm});
            skLineSegment(sketch, "E373", {"start": v(-24.13, -21.83) * mm, "end": v(-24.02, -21.78) * mm});
            skLineSegment(sketch, "E374", {"start": v(-24.02, -21.78) * mm, "end": v(-23.91, -21.73) * mm});
            skLineSegment(sketch, "E375", {"start": v(-23.91, -21.73) * mm, "end": v(-23.81, -21.68) * mm});
            skLineSegment(sketch, "E376", {"start": v(-23.81, -21.68) * mm, "end": v(-23.71, -21.64) * mm});
            skLineSegment(sketch, "E377", {"start": v(-23.71, -21.64) * mm, "end": v(-23.62, -21.6) * mm});
            skLineSegment(sketch, "E378", {"start": v(-23.62, -21.6) * mm, "end": v(-23.53, -21.55) * mm});
            skLineSegment(sketch, "E379", {"start": v(-23.53, -21.55) * mm, "end": v(-23.45, -21.5) * mm});
            skLineSegment(sketch, "E380", {"start": v(-23.45, -21.5) * mm, "end": v(-23.36, -21.46) * mm});
            skLineSegment(sketch, "E381", {"start": v(-23.36, -21.46) * mm, "end": v(-23.29, -21.42) * mm});
            skLineSegment(sketch, "E382", {"start": v(-23.29, -21.42) * mm, "end": v(-23.22, -21.38) * mm});
            skLineSegment(sketch, "E383", {"start": v(-23.22, -21.38) * mm, "end": v(-23.15, -21.34) * mm});
            skLineSegment(sketch, "E384", {"start": v(-23.15, -21.34) * mm, "end": v(-23.08, -21.3) * mm});
            skLineSegment(sketch, "E385", {"start": v(-23.08, -21.3) * mm, "end": v(-23.02, -21.26) * mm});
            skLineSegment(sketch, "E386", {"start": v(-23.02, -21.26) * mm, "end": v(-22.97, -21.22) * mm});
            skLineSegment(sketch, "E387", {"start": v(-22.97, -21.22) * mm, "end": v(-22.91, -21.2) * mm});
            skLineSegment(sketch, "E388", {"start": v(-22.91, -21.2) * mm, "end": v(-22.86, -21.16) * mm});
            skLineSegment(sketch, "E389", {"start": v(-22.86, -21.16) * mm, "end": v(-22.82, -21.13) * mm});
            skLineSegment(sketch, "E390", {"start": v(-22.82, -21.13) * mm, "end": v(-22.78, -21.1) * mm});
            skLineSegment(sketch, "E391", {"start": v(-22.78, -21.1) * mm, "end": v(-22.74, -21.07) * mm});
            skLineSegment(sketch, "E392", {"start": v(-22.74, -21.07) * mm, "end": v(-22.7, -21.05) * mm});
            skLineSegment(sketch, "E393", {"start": v(-22.7, -21.05) * mm, "end": v(-22.68, -21.03) * mm});
            skLineSegment(sketch, "E394", {"start": v(-22.68, -21.03) * mm, "end": v(-22.65, -21) * mm});
            skLineSegment(sketch, "E395", {"start": v(-22.65, -21) * mm, "end": v(-22.63, -20.99) * mm});
            skLineSegment(sketch, "E396", {"start": v(-22.63, -20.99) * mm, "end": v(-22.6, -20.97) * mm});
            skLineSegment(sketch, "E397", {"start": v(-22.6, -20.97) * mm, "end": v(-22.6, -20.96) * mm});
            skLineSegment(sketch, "E398", {"start": v(-22.6, -20.96) * mm, "end": v(-22.58, -20.95) * mm});
            skLineSegment(sketch, "E399", {"start": v(-22.58, -20.95) * mm, "end": v(-22.57, -20.94) * mm});
            skLineSegment(sketch, "E400", {"start": v(-22.57, -20.94) * mm, "end": v(-22.56, -20.93) * mm});
            skLineSegment(sketch, "E401", {"start": v(-22.56, -20.93) * mm, "end": v(-22.17, -20.57) * mm});
            skLineSegment(sketch, "E402", {"start": v(-22.17, -20.57) * mm, "end": v(-20.52, -22.21) * mm});
            skLineSegment(sketch, "E403", {"start": v(-20.52, -22.21) * mm, "end": v(-20.89, -22.6) * mm});
            skLineSegment(sketch, "E404", {"start": v(-20.89, -22.6) * mm, "end": v(-20.9, -22.61) * mm});
            skLineSegment(sketch, "E405", {"start": v(-20.9, -22.61) * mm, "end": v(-20.9, -22.62) * mm});
            skLineSegment(sketch, "E406", {"start": v(-20.9, -22.62) * mm, "end": v(-20.91, -22.64) * mm});
            skLineSegment(sketch, "E407", {"start": v(-20.91, -22.64) * mm, "end": v(-20.92, -22.65) * mm});
            skLineSegment(sketch, "E408", {"start": v(-20.92, -22.65) * mm, "end": v(-20.94, -22.67) * mm});
            skLineSegment(sketch, "E409", {"start": v(-20.94, -22.67) * mm, "end": v(-20.96, -22.7) * mm});
            skLineSegment(sketch, "E410", {"start": v(-20.96, -22.7) * mm, "end": v(-20.98, -22.72) * mm});
            skLineSegment(sketch, "E411", {"start": v(-20.98, -22.72) * mm, "end": v(-21, -22.75) * mm});
            skLineSegment(sketch, "E412", {"start": v(-21, -22.75) * mm, "end": v(-21.03, -22.79) * mm});
            skLineSegment(sketch, "E413", {"start": v(-21.03, -22.79) * mm, "end": v(-21.05, -22.82) * mm});
            skLineSegment(sketch, "E414", {"start": v(-21.05, -22.82) * mm, "end": v(-21.08, -22.86) * mm});
            skLineSegment(sketch, "E415", {"start": v(-21.08, -22.86) * mm, "end": v(-21.11, -22.9) * mm});
            skLineSegment(sketch, "E416", {"start": v(-21.11, -22.9) * mm, "end": v(-21.14, -22.96) * mm});
            skLineSegment(sketch, "E417", {"start": v(-21.14, -22.96) * mm, "end": v(-21.18, -23) * mm});
            skLineSegment(sketch, "E418", {"start": v(-21.18, -23) * mm, "end": v(-21.21, -23.07) * mm});
            skLineSegment(sketch, "E419", {"start": v(-21.21, -23.07) * mm, "end": v(-21.25, -23.13) * mm});
            skLineSegment(sketch, "E420", {"start": v(-21.25, -23.13) * mm, "end": v(-21.29, -23.2) * mm});
            skLineSegment(sketch, "E421", {"start": v(-21.29, -23.2) * mm, "end": v(-21.33, -23.26) * mm});
            skLineSegment(sketch, "E422", {"start": v(-21.33, -23.26) * mm, "end": v(-21.37, -23.33) * mm});
            skLineSegment(sketch, "E423", {"start": v(-21.37, -23.33) * mm, "end": v(-21.41, -23.4) * mm});
            skLineSegment(sketch, "E424", {"start": v(-21.41, -23.4) * mm, "end": v(-21.45, -23.49) * mm});
            skLineSegment(sketch, "E425", {"start": v(-21.45, -23.49) * mm, "end": v(-21.5, -23.57) * mm});
            skLineSegment(sketch, "E426", {"start": v(-21.5, -23.57) * mm, "end": v(-21.54, -23.66) * mm});
            skLineSegment(sketch, "E427", {"start": v(-21.54, -23.66) * mm, "end": v(-21.59, -23.76) * mm});
            skLineSegment(sketch, "E428", {"start": v(-21.59, -23.76) * mm, "end": v(-21.63, -23.86) * mm});
            skLineSegment(sketch, "E429", {"start": v(-21.63, -23.86) * mm, "end": v(-21.68, -23.96) * mm});
            skLineSegment(sketch, "E430", {"start": v(-21.68, -23.96) * mm, "end": v(-21.73, -24.06) * mm});
            skLineSegment(sketch, "E431", {"start": v(-21.73, -24.06) * mm, "end": v(-21.78, -24.18) * mm});
            skLineSegment(sketch, "E432", {"start": v(-21.78, -24.18) * mm, "end": v(-21.83, -24.3) * mm});
            skLineSegment(sketch, "E433", {"start": v(-21.83, -24.3) * mm, "end": v(-21.87, -24.41) * mm});
            skLineSegment(sketch, "E434", {"start": v(-21.87, -24.41) * mm, "end": v(-21.92, -24.53) * mm});
            skLineSegment(sketch, "E435", {"start": v(-21.92, -24.53) * mm, "end": v(-21.97, -24.66) * mm});
            skLineSegment(sketch, "E436", {"start": v(-21.97, -24.66) * mm, "end": v(-22.02, -24.8) * mm});
            skLineSegment(sketch, "E437", {"start": v(-22.02, -24.8) * mm, "end": v(-22.07, -24.93) * mm});
            skLineSegment(sketch, "E438", {"start": v(-22.07, -24.93) * mm, "end": v(-22.12, -25.08) * mm});
            skLineSegment(sketch, "E439", {"start": v(-22.12, -25.08) * mm, "end": v(-22.16, -25.22) * mm});
            skLineSegment(sketch, "E440", {"start": v(-22.16, -25.22) * mm, "end": v(-22.21, -25.37) * mm});
            skLineSegment(sketch, "E441", {"start": v(-22.21, -25.37) * mm, "end": v(-22.26, -25.53) * mm});
            skLineSegment(sketch, "E442", {"start": v(-22.26, -25.53) * mm, "end": v(-22.3, -25.69) * mm});
            skLineSegment(sketch, "E443", {"start": v(-22.3, -25.69) * mm, "end": v(-22.35, -25.85) * mm});
            skLineSegment(sketch, "E444", {"start": v(-22.35, -25.85) * mm, "end": v(-22.4, -26.02) * mm});
            skLineSegment(sketch, "E445", {"start": v(-22.4, -26.02) * mm, "end": v(-22.44, -26.2) * mm});
            skLineSegment(sketch, "E446", {"start": v(-22.44, -26.2) * mm, "end": v(-22.48, -26.37) * mm});
            skLineSegment(sketch, "E447", {"start": v(-22.48, -26.37) * mm, "end": v(-22.52, -26.56) * mm});
            skLineSegment(sketch, "E448", {"start": v(-22.52, -26.56) * mm, "end": v(-22.52, -26.7) * mm});
            skLineSegment(sketch, "E449", {"start": v(-22.52, -26.7) * mm, "end": v(-21.38, -27.63) * mm});
            skLineSegment(sketch, "E450", {"start": v(-21.38, -27.63) * mm, "end": v(-21.24, -27.6) * mm});
            skLineSegment(sketch, "E451", {"start": v(-21.24, -27.6) * mm, "end": v(-21.07, -27.52) * mm});
            skLineSegment(sketch, "E452", {"start": v(-21.07, -27.52) * mm, "end": v(-20.9, -27.44) * mm});
            skLineSegment(sketch, "E453", {"start": v(-20.9, -27.44) * mm, "end": v(-20.74, -27.36) * mm});
            skLineSegment(sketch, "E454", {"start": v(-20.74, -27.36) * mm, "end": v(-20.59, -27.28) * mm});
            skLineSegment(sketch, "E455", {"start": v(-20.59, -27.28) * mm, "end": v(-20.43, -27.2) * mm});
            skLineSegment(sketch, "E456", {"start": v(-20.43, -27.2) * mm, "end": v(-20.29, -27.12) * mm});
            skLineSegment(sketch, "E457", {"start": v(-20.29, -27.12) * mm, "end": v(-20.14, -27.04) * mm});
            skLineSegment(sketch, "E458", {"start": v(-20.14, -27.04) * mm, "end": v(-20, -26.97) * mm});
            skLineSegment(sketch, "E459", {"start": v(-20, -26.97) * mm, "end": v(-19.87, -26.89) * mm});
            skLineSegment(sketch, "E460", {"start": v(-19.87, -26.89) * mm, "end": v(-19.74, -26.81) * mm});
            skLineSegment(sketch, "E461", {"start": v(-19.74, -26.81) * mm, "end": v(-19.62, -26.73) * mm});
            skLineSegment(sketch, "E462", {"start": v(-19.62, -26.73) * mm, "end": v(-19.5, -26.66) * mm});
            skLineSegment(sketch, "E463", {"start": v(-19.5, -26.66) * mm, "end": v(-19.38, -26.58) * mm});
            skLineSegment(sketch, "E464", {"start": v(-19.38, -26.58) * mm, "end": v(-19.27, -26.51) * mm});
            skLineSegment(sketch, "E465", {"start": v(-19.27, -26.51) * mm, "end": v(-19.17, -26.44) * mm});
            skLineSegment(sketch, "E466", {"start": v(-19.17, -26.44) * mm, "end": v(-19.06, -26.37) * mm});
            skLineSegment(sketch, "E467", {"start": v(-19.06, -26.37) * mm, "end": v(-18.97, -26.3) * mm});
            skLineSegment(sketch, "E468", {"start": v(-18.97, -26.3) * mm, "end": v(-18.87, -26.23) * mm});
            skLineSegment(sketch, "E469", {"start": v(-18.87, -26.23) * mm, "end": v(-18.78, -26.16) * mm});
            skLineSegment(sketch, "E470", {"start": v(-18.78, -26.16) * mm, "end": v(-18.7, -26.1) * mm});
            skLineSegment(sketch, "E471", {"start": v(-18.7, -26.1) * mm, "end": v(-18.61, -26.03) * mm});
            skLineSegment(sketch, "E472", {"start": v(-18.61, -26.03) * mm, "end": v(-18.54, -25.97) * mm});
            skLineSegment(sketch, "E473", {"start": v(-18.54, -25.97) * mm, "end": v(-18.46, -25.9) * mm});
            skLineSegment(sketch, "E474", {"start": v(-18.46, -25.9) * mm, "end": v(-18.4, -25.85) * mm});
            skLineSegment(sketch, "E475", {"start": v(-18.4, -25.85) * mm, "end": v(-18.33, -25.8) * mm});
            skLineSegment(sketch, "E476", {"start": v(-18.33, -25.8) * mm, "end": v(-18.26, -25.74) * mm});
            skLineSegment(sketch, "E477", {"start": v(-18.26, -25.74) * mm, "end": v(-18.2, -25.68) * mm});
            skLineSegment(sketch, "E478", {"start": v(-18.2, -25.68) * mm, "end": v(-18.15, -25.63) * mm});
            skLineSegment(sketch, "E479", {"start": v(-18.15, -25.63) * mm, "end": v(-18.1, -25.58) * mm});
            skLineSegment(sketch, "E480", {"start": v(-18.1, -25.58) * mm, "end": v(-18.05, -25.54) * mm});
            skLineSegment(sketch, "E481", {"start": v(-18.05, -25.54) * mm, "end": v(-18, -25.5) * mm});
            skLineSegment(sketch, "E482", {"start": v(-18, -25.5) * mm, "end": v(-17.97, -25.45) * mm});
            skLineSegment(sketch, "E483", {"start": v(-17.97, -25.45) * mm, "end": v(-17.93, -25.41) * mm});
            skLineSegment(sketch, "E484", {"start": v(-17.93, -25.41) * mm, "end": v(-17.9, -25.37) * mm});
            skLineSegment(sketch, "E485", {"start": v(-17.9, -25.37) * mm, "end": v(-17.86, -25.34) * mm});
            skLineSegment(sketch, "E486", {"start": v(-17.86, -25.34) * mm, "end": v(-17.84, -25.3) * mm});
            skLineSegment(sketch, "E487", {"start": v(-17.84, -25.3) * mm, "end": v(-17.81, -25.28) * mm});
            skLineSegment(sketch, "E488", {"start": v(-17.81, -25.28) * mm, "end": v(-17.79, -25.26) * mm});
            skLineSegment(sketch, "E489", {"start": v(-17.79, -25.26) * mm, "end": v(-17.77, -25.23) * mm});
            skLineSegment(sketch, "E490", {"start": v(-17.77, -25.23) * mm, "end": v(-17.75, -25.21) * mm});
            skLineSegment(sketch, "E491", {"start": v(-17.75, -25.21) * mm, "end": v(-17.74, -25.2) * mm});
            skLineSegment(sketch, "E492", {"start": v(-17.74, -25.2) * mm, "end": v(-17.73, -25.18) * mm});
            skLineSegment(sketch, "E493", {"start": v(-17.73, -25.18) * mm, "end": v(-17.72, -25.17) * mm});
            skLineSegment(sketch, "E494", {"start": v(-17.72, -25.17) * mm, "end": v(-17.72, -25.17) * mm});
            skLineSegment(sketch, "E495", {"start": v(-17.72, -25.17) * mm, "end": v(-17.4, -24.73) * mm});
            skLineSegment(sketch, "E496", {"start": v(-17.4, -24.73) * mm, "end": v(-15.45, -26) * mm});
            skLineSegment(sketch, "E497", {"start": v(-15.45, -26) * mm, "end": v(-15.73, -26.46) * mm});
            skLineSegment(sketch, "E498", {"start": v(-15.73, -26.46) * mm, "end": v(-15.73, -26.46) * mm});
            skLineSegment(sketch, "E499", {"start": v(-15.73, -26.46) * mm, "end": v(-15.74, -26.47) * mm});
            skLineSegment(sketch, "E500", {"start": v(-15.74, -26.47) * mm, "end": v(-15.75, -26.49) * mm});
            skLineSegment(sketch, "E501", {"start": v(-15.75, -26.49) * mm, "end": v(-15.76, -26.5) * mm});
            skLineSegment(sketch, "E502", {"start": v(-15.76, -26.5) * mm, "end": v(-15.77, -26.53) * mm});
            skLineSegment(sketch, "E503", {"start": v(-15.77, -26.53) * mm, "end": v(-15.78, -26.56) * mm});
            skLineSegment(sketch, "E504", {"start": v(-15.78, -26.56) * mm, "end": v(-15.8, -26.59) * mm});
            skLineSegment(sketch, "E505", {"start": v(-15.8, -26.59) * mm, "end": v(-15.81, -26.62) * mm});
            skLineSegment(sketch, "E506", {"start": v(-15.81, -26.62) * mm, "end": v(-15.83, -26.66) * mm});
            skLineSegment(sketch, "E507", {"start": v(-15.83, -26.66) * mm, "end": v(-15.85, -26.7) * mm});
            skLineSegment(sketch, "E508", {"start": v(-15.85, -26.7) * mm, "end": v(-15.87, -26.75) * mm});
            skLineSegment(sketch, "E509", {"start": v(-15.87, -26.75) * mm, "end": v(-15.89, -26.8) * mm});
            skLineSegment(sketch, "E510", {"start": v(-15.89, -26.8) * mm, "end": v(-15.9, -26.85) * mm});
            skLineSegment(sketch, "E511", {"start": v(-15.9, -26.85) * mm, "end": v(-15.93, -26.9) * mm});
            skLineSegment(sketch, "E512", {"start": v(-15.93, -26.9) * mm, "end": v(-15.95, -26.97) * mm});
            skLineSegment(sketch, "E513", {"start": v(-15.95, -26.97) * mm, "end": v(-15.98, -27.04) * mm});
            skLineSegment(sketch, "E514", {"start": v(-15.98, -27.04) * mm, "end": v(-16, -27.11) * mm});
            skLineSegment(sketch, "E515", {"start": v(-16, -27.11) * mm, "end": v(-16.03, -27.19) * mm});
            skLineSegment(sketch, "E516", {"start": v(-16.03, -27.19) * mm, "end": v(-16.05, -27.26) * mm});
            skLineSegment(sketch, "E517", {"start": v(-16.05, -27.26) * mm, "end": v(-16.08, -27.35) * mm});
            skLineSegment(sketch, "E518", {"start": v(-16.08, -27.35) * mm, "end": v(-16.1, -27.44) * mm});
            skLineSegment(sketch, "E519", {"start": v(-16.1, -27.44) * mm, "end": v(-16.13, -27.53) * mm});
            skLineSegment(sketch, "E520", {"start": v(-16.13, -27.53) * mm, "end": v(-16.15, -27.63) * mm});
            skLineSegment(sketch, "E521", {"start": v(-16.15, -27.63) * mm, "end": v(-16.18, -27.73) * mm});
            skLineSegment(sketch, "E522", {"start": v(-16.18, -27.73) * mm, "end": v(-16.2, -27.83) * mm});
            skLineSegment(sketch, "E523", {"start": v(-16.2, -27.83) * mm, "end": v(-16.23, -27.94) * mm});
            skLineSegment(sketch, "E524", {"start": v(-16.23, -27.94) * mm, "end": v(-16.25, -28.06) * mm});
            skLineSegment(sketch, "E525", {"start": v(-16.25, -28.06) * mm, "end": v(-16.27, -28.17) * mm});
            skLineSegment(sketch, "E526", {"start": v(-16.27, -28.17) * mm, "end": v(-16.3, -28.3) * mm});
            skLineSegment(sketch, "E527", {"start": v(-16.3, -28.3) * mm, "end": v(-16.32, -28.42) * mm});
            skLineSegment(sketch, "E528", {"start": v(-16.32, -28.42) * mm, "end": v(-16.34, -28.56) * mm});
            skLineSegment(sketch, "E529", {"start": v(-16.34, -28.56) * mm, "end": v(-16.36, -28.7) * mm});
            skLineSegment(sketch, "E530", {"start": v(-16.36, -28.7) * mm, "end": v(-16.38, -28.83) * mm});
            skLineSegment(sketch, "E531", {"start": v(-16.38, -28.83) * mm, "end": v(-16.4, -28.98) * mm});
            skLineSegment(sketch, "E532", {"start": v(-16.4, -28.98) * mm, "end": v(-16.42, -29.13) * mm});
            skLineSegment(sketch, "E533", {"start": v(-16.42, -29.13) * mm, "end": v(-16.44, -29.28) * mm});
            skLineSegment(sketch, "E534", {"start": v(-16.44, -29.28) * mm, "end": v(-16.45, -29.44) * mm});
            skLineSegment(sketch, "E535", {"start": v(-16.45, -29.44) * mm, "end": v(-16.46, -29.6) * mm});
            skLineSegment(sketch, "E536", {"start": v(-16.46, -29.6) * mm, "end": v(-16.48, -29.76) * mm});
            skLineSegment(sketch, "E537", {"start": v(-16.48, -29.76) * mm, "end": v(-16.49, -29.94) * mm});
            skLineSegment(sketch, "E538", {"start": v(-16.49, -29.94) * mm, "end": v(-16.5, -30.11) * mm});
            skLineSegment(sketch, "E539", {"start": v(-16.5, -30.11) * mm, "end": v(-16.5, -30.29) * mm});
            skLineSegment(sketch, "E540", {"start": v(-16.5, -30.29) * mm, "end": v(-16.5, -30.47) * mm});
            skLineSegment(sketch, "E541", {"start": v(-16.5, -30.47) * mm, "end": v(-16.5, -30.66) * mm});
            skLineSegment(sketch, "E542", {"start": v(-16.5, -30.66) * mm, "end": v(-16.48, -30.8) * mm});
            skLineSegment(sketch, "E543", {"start": v(-16.48, -30.8) * mm, "end": v(-15.17, -31.47) * mm});
            skLineSegment(sketch, "E544", {"start": v(-15.17, -31.47) * mm, "end": v(-15.04, -31.4) * mm});
            skLineSegment(sketch, "E545", {"start": v(-15.04, -31.4) * mm, "end": v(-14.89, -31.3) * mm});
            skLineSegment(sketch, "E546", {"start": v(-14.89, -31.3) * mm, "end": v(-14.74, -31.18) * mm});
            skLineSegment(sketch, "E547", {"start": v(-14.74, -31.18) * mm, "end": v(-14.6, -31.07) * mm});
            skLineSegment(sketch, "E548", {"start": v(-14.6, -31.07) * mm, "end": v(-14.46, -30.96) * mm});
            skLineSegment(sketch, "E549", {"start": v(-14.46, -30.96) * mm, "end": v(-14.33, -30.85) * mm});
            skLineSegment(sketch, "E550", {"start": v(-14.33, -30.85) * mm, "end": v(-14.2, -30.75) * mm});
            skLineSegment(sketch, "E551", {"start": v(-14.2, -30.75) * mm, "end": v(-14.08, -30.64) * mm});
            skLineSegment(sketch, "E552", {"start": v(-14.08, -30.64) * mm, "end": v(-13.96, -30.54) * mm});
            skLineSegment(sketch, "E553", {"start": v(-13.96, -30.54) * mm, "end": v(-13.85, -30.43) * mm});
            skLineSegment(sketch, "E554", {"start": v(-13.85, -30.43) * mm, "end": v(-13.74, -30.33) * mm});
            skLineSegment(sketch, "E555", {"start": v(-13.74, -30.33) * mm, "end": v(-13.63, -30.23) * mm});
            skLineSegment(sketch, "E556", {"start": v(-13.63, -30.23) * mm, "end": v(-13.53, -30.13) * mm});
            skLineSegment(sketch, "E557", {"start": v(-13.53, -30.13) * mm, "end": v(-13.43, -30.03) * mm});
            skLineSegment(sketch, "E558", {"start": v(-13.43, -30.03) * mm, "end": v(-13.34, -29.94) * mm});
            skLineSegment(sketch, "E559", {"start": v(-13.34, -29.94) * mm, "end": v(-13.25, -29.85) * mm});
            skLineSegment(sketch, "E560", {"start": v(-13.25, -29.85) * mm, "end": v(-13.17, -29.75) * mm});
            skLineSegment(sketch, "E561", {"start": v(-13.17, -29.75) * mm, "end": v(-13.08, -29.67) * mm});
            skLineSegment(sketch, "E562", {"start": v(-13.08, -29.67) * mm, "end": v(-13, -29.58) * mm});
            skLineSegment(sketch, "E563", {"start": v(-13, -29.58) * mm, "end": v(-12.93, -29.5) * mm});
            skLineSegment(sketch, "E564", {"start": v(-12.93, -29.5) * mm, "end": v(-12.86, -29.41) * mm});
            skLineSegment(sketch, "E565", {"start": v(-12.86, -29.41) * mm, "end": v(-12.8, -29.33) * mm});
            skLineSegment(sketch, "E566", {"start": v(-12.8, -29.33) * mm, "end": v(-12.73, -29.25) * mm});
            skLineSegment(sketch, "E567", {"start": v(-12.73, -29.25) * mm, "end": v(-12.67, -29.18) * mm});
            skLineSegment(sketch, "E568", {"start": v(-12.67, -29.18) * mm, "end": v(-12.62, -29.1) * mm});
            skLineSegment(sketch, "E569", {"start": v(-12.62, -29.1) * mm, "end": v(-12.56, -29.04) * mm});
            skLineSegment(sketch, "E570", {"start": v(-12.56, -29.04) * mm, "end": v(-12.51, -28.97) * mm});
            skLineSegment(sketch, "E571", {"start": v(-12.51, -28.97) * mm, "end": v(-12.47, -28.9) * mm});
            skLineSegment(sketch, "E572", {"start": v(-12.47, -28.9) * mm, "end": v(-12.42, -28.84) * mm});
            skLineSegment(sketch, "E573", {"start": v(-12.42, -28.84) * mm, "end": v(-12.38, -28.79) * mm});
            skLineSegment(sketch, "E574", {"start": v(-12.38, -28.79) * mm, "end": v(-12.35, -28.73) * mm});
            skLineSegment(sketch, "E575", {"start": v(-12.35, -28.73) * mm, "end": v(-12.31, -28.68) * mm});
            skLineSegment(sketch, "E576", {"start": v(-12.31, -28.68) * mm, "end": v(-12.28, -28.63) * mm});
            skLineSegment(sketch, "E577", {"start": v(-12.28, -28.63) * mm, "end": v(-12.25, -28.58) * mm});
            skLineSegment(sketch, "E578", {"start": v(-12.25, -28.58) * mm, "end": v(-12.23, -28.54) * mm});
            skLineSegment(sketch, "E579", {"start": v(-12.23, -28.54) * mm, "end": v(-12.2, -28.5) * mm});
            skLineSegment(sketch, "E580", {"start": v(-12.2, -28.5) * mm, "end": v(-12.18, -28.46) * mm});
            skLineSegment(sketch, "E581", {"start": v(-12.18, -28.46) * mm, "end": v(-12.17, -28.43) * mm});
            skLineSegment(sketch, "E582", {"start": v(-12.17, -28.43) * mm, "end": v(-12.15, -28.4) * mm});
            skLineSegment(sketch, "E583", {"start": v(-12.15, -28.4) * mm, "end": v(-12.14, -28.38) * mm});
            skLineSegment(sketch, "E584", {"start": v(-12.14, -28.38) * mm, "end": v(-12.12, -28.35) * mm});
            skLineSegment(sketch, "E585", {"start": v(-12.12, -28.35) * mm, "end": v(-12.11, -28.34) * mm});
            skLineSegment(sketch, "E586", {"start": v(-12.11, -28.34) * mm, "end": v(-12.1, -28.32) * mm});
            skLineSegment(sketch, "E587", {"start": v(-12.1, -28.32) * mm, "end": v(-12.1, -28.3) * mm});
            skLineSegment(sketch, "E588", {"start": v(-12.1, -28.3) * mm, "end": v(-12.1, -28.3) * mm});
            skLineSegment(sketch, "E589", {"start": v(-12.1, -28.3) * mm, "end": v(-11.89, -27.8) * mm});
            skLineSegment(sketch, "E590", {"start": v(-11.89, -27.8) * mm, "end": v(-9.71, -28.64) * mm});
            skLineSegment(sketch, "E591", {"start": v(-9.71, -28.64) * mm, "end": v(-9.89, -29.15) * mm});
            skLineSegment(sketch, "E592", {"start": v(-9.89, -29.15) * mm, "end": v(-9.89, -29.16) * mm});
            skLineSegment(sketch, "E593", {"start": v(-9.89, -29.16) * mm, "end": v(-9.9, -29.17) * mm});
            skLineSegment(sketch, "E594", {"start": v(-9.9, -29.17) * mm, "end": v(-9.9, -29.18) * mm});
            skLineSegment(sketch, "E595", {"start": v(-9.9, -29.18) * mm, "end": v(-9.9, -29.2) * mm});
            skLineSegment(sketch, "E596", {"start": v(-9.9, -29.2) * mm, "end": v(-9.9, -29.23) * mm});
            skLineSegment(sketch, "E597", {"start": v(-9.9, -29.23) * mm, "end": v(-9.92, -29.26) * mm});
            skLineSegment(sketch, "E598", {"start": v(-9.92, -29.26) * mm, "end": v(-9.92, -29.29) * mm});
            skLineSegment(sketch, "E599", {"start": v(-9.92, -29.29) * mm, "end": v(-9.93, -29.33) * mm});
            skLineSegment(sketch, "E600", {"start": v(-9.93, -29.33) * mm, "end": v(-9.94, -29.37) * mm});
            skLineSegment(sketch, "E601", {"start": v(-9.94, -29.37) * mm, "end": v(-9.95, -29.41) * mm});
            skLineSegment(sketch, "E602", {"start": v(-9.95, -29.41) * mm, "end": v(-9.96, -29.46) * mm});
            skLineSegment(sketch, "E603", {"start": v(-9.96, -29.46) * mm, "end": v(-9.97, -29.51) * mm});
            skLineSegment(sketch, "E604", {"start": v(-9.97, -29.51) * mm, "end": v(-9.98, -29.57) * mm});
            skLineSegment(sketch, "E605", {"start": v(-9.98, -29.57) * mm, "end": v(-9.99, -29.63) * mm});
            skLineSegment(sketch, "E606", {"start": v(-9.99, -29.63) * mm, "end": v(-10, -29.7) * mm});
            skLineSegment(sketch, "E607", {"start": v(-10, -29.7) * mm, "end": v(-10, -29.77) * mm});
            skLineSegment(sketch, "E608", {"start": v(-10, -29.77) * mm, "end": v(-10.01, -29.84) * mm});
            skLineSegment(sketch, "E609", {"start": v(-10.01, -29.84) * mm, "end": v(-10.02, -29.92) * mm});
            skLineSegment(sketch, "E610", {"start": v(-10.02, -29.92) * mm, "end": v(-10.03, -30) * mm});
            skLineSegment(sketch, "E611", {"start": v(-10.03, -30) * mm, "end": v(-10.04, -30.1) * mm});
            skLineSegment(sketch, "E612", {"start": v(-10.04, -30.1) * mm, "end": v(-10.04, -30.18) * mm});
            skLineSegment(sketch, "E613", {"start": v(-10.04, -30.18) * mm, "end": v(-10.05, -30.28) * mm});
            skLineSegment(sketch, "E614", {"start": v(-10.05, -30.28) * mm, "end": v(-10.05, -30.38) * mm});
            skLineSegment(sketch, "E615", {"start": v(-10.05, -30.38) * mm, "end": v(-10.06, -30.48) * mm});
            skLineSegment(sketch, "E616", {"start": v(-10.06, -30.48) * mm, "end": v(-10.06, -30.6) * mm});
            skLineSegment(sketch, "E617", {"start": v(-10.06, -30.6) * mm, "end": v(-10.06, -30.7) * mm});
            skLineSegment(sketch, "E618", {"start": v(-10.06, -30.7) * mm, "end": v(-10.06, -30.82) * mm});
            skLineSegment(sketch, "E619", {"start": v(-10.06, -30.82) * mm, "end": v(-10.06, -30.94) * mm});
            skLineSegment(sketch, "E620", {"start": v(-10.06, -30.94) * mm, "end": v(-10.06, -31.07) * mm});
            skLineSegment(sketch, "E621", {"start": v(-10.06, -31.07) * mm, "end": v(-10.05, -31.2) * mm});
            skLineSegment(sketch, "E622", {"start": v(-10.05, -31.2) * mm, "end": v(-10.05, -31.33) * mm});
            skLineSegment(sketch, "E623", {"start": v(-10.05, -31.33) * mm, "end": v(-10.04, -31.47) * mm});
            skLineSegment(sketch, "E624", {"start": v(-10.04, -31.47) * mm, "end": v(-10.03, -31.6) * mm});
            skLineSegment(sketch, "E625", {"start": v(-10.03, -31.6) * mm, "end": v(-10.02, -31.75) * mm});
            skLineSegment(sketch, "E626", {"start": v(-10.02, -31.75) * mm, "end": v(-10, -31.9) * mm});
            skLineSegment(sketch, "E627", {"start": v(-10, -31.9) * mm, "end": v(-9.99, -32.06) * mm});
            skLineSegment(sketch, "E628", {"start": v(-9.99, -32.06) * mm, "end": v(-9.97, -32.21) * mm});
            skLineSegment(sketch, "E629", {"start": v(-9.97, -32.21) * mm, "end": v(-9.95, -32.38) * mm});
            skLineSegment(sketch, "E630", {"start": v(-9.95, -32.38) * mm, "end": v(-9.93, -32.54) * mm});
            skLineSegment(sketch, "E631", {"start": v(-9.93, -32.54) * mm, "end": v(-9.9, -32.7) * mm});
            skLineSegment(sketch, "E632", {"start": v(-9.9, -32.7) * mm, "end": v(-9.87, -32.88) * mm});
            skLineSegment(sketch, "E633", {"start": v(-9.87, -32.88) * mm, "end": v(-9.84, -33.06) * mm});
            skLineSegment(sketch, "E634", {"start": v(-9.84, -33.06) * mm, "end": v(-9.8, -33.24) * mm});
            skLineSegment(sketch, "E635", {"start": v(-9.8, -33.24) * mm, "end": v(-9.77, -33.42) * mm});
            skLineSegment(sketch, "E636", {"start": v(-9.77, -33.42) * mm, "end": v(-9.72, -33.55) * mm});
            skLineSegment(sketch, "E637", {"start": v(-9.72, -33.55) * mm, "end": v(-8.3, -33.94) * mm});
            skLineSegment(sketch, "E638", {"start": v(-8.3, -33.94) * mm, "end": v(-8.18, -33.85) * mm});
            skLineSegment(sketch, "E639", {"start": v(-8.18, -33.85) * mm, "end": v(-8.05, -33.7) * mm});
            skLineSegment(sketch, "E640", {"start": v(-8.05, -33.7) * mm, "end": v(-7.93, -33.57) * mm});
            skLineSegment(sketch, "E641", {"start": v(-7.93, -33.57) * mm, "end": v(-7.82, -33.43) * mm});
            skLineSegment(sketch, "E642", {"start": v(-7.82, -33.43) * mm, "end": v(-7.7, -33.3) * mm});
            skLineSegment(sketch, "E643", {"start": v(-7.7, -33.3) * mm, "end": v(-7.6, -33.16) * mm});
            skLineSegment(sketch, "E644", {"start": v(-7.6, -33.16) * mm, "end": v(-7.5, -33.03) * mm});
            skLineSegment(sketch, "E645", {"start": v(-7.5, -33.03) * mm, "end": v(-7.4, -32.9) * mm});
            skLineSegment(sketch, "E646", {"start": v(-7.4, -32.9) * mm, "end": v(-7.3, -32.77) * mm});
            skLineSegment(sketch, "E647", {"start": v(-7.3, -32.77) * mm, "end": v(-7.22, -32.65) * mm});
            skLineSegment(sketch, "E648", {"start": v(-7.22, -32.65) * mm, "end": v(-7.13, -32.52) * mm});
            skLineSegment(sketch, "E649", {"start": v(-7.13, -32.52) * mm, "end": v(-7.05, -32.4) * mm});
            skLineSegment(sketch, "E650", {"start": v(-7.05, -32.4) * mm, "end": v(-6.97, -32.29) * mm});
            skLineSegment(sketch, "E651", {"start": v(-6.97, -32.29) * mm, "end": v(-6.9, -32.17) * mm});
            skLineSegment(sketch, "E652", {"start": v(-6.9, -32.17) * mm, "end": v(-6.82, -32.06) * mm});
            skLineSegment(sketch, "E653", {"start": v(-6.82, -32.06) * mm, "end": v(-6.76, -31.95) * mm});
            skLineSegment(sketch, "E654", {"start": v(-6.76, -31.95) * mm, "end": v(-6.7, -31.84) * mm});
            skLineSegment(sketch, "E655", {"start": v(-6.7, -31.84) * mm, "end": v(-6.63, -31.74) * mm});
            skLineSegment(sketch, "E656", {"start": v(-6.63, -31.74) * mm, "end": v(-6.57, -31.64) * mm});
            skLineSegment(sketch, "E657", {"start": v(-6.57, -31.64) * mm, "end": v(-6.52, -31.54) * mm});
            skLineSegment(sketch, "E658", {"start": v(-6.52, -31.54) * mm, "end": v(-6.47, -31.44) * mm});
            skLineSegment(sketch, "E659", {"start": v(-6.47, -31.44) * mm, "end": v(-6.42, -31.35) * mm});
            skLineSegment(sketch, "E660", {"start": v(-6.42, -31.35) * mm, "end": v(-6.37, -31.26) * mm});
            skLineSegment(sketch, "E661", {"start": v(-6.37, -31.26) * mm, "end": v(-6.33, -31.18) * mm});
            skLineSegment(sketch, "E662", {"start": v(-6.33, -31.18) * mm, "end": v(-6.29, -31.1) * mm});
            skLineSegment(sketch, "E663", {"start": v(-6.29, -31.1) * mm, "end": v(-6.25, -31.01) * mm});
            skLineSegment(sketch, "E664", {"start": v(-6.25, -31.01) * mm, "end": v(-6.22, -30.94) * mm});
            skLineSegment(sketch, "E665", {"start": v(-6.22, -30.94) * mm, "end": v(-6.19, -30.87) * mm});
            skLineSegment(sketch, "E666", {"start": v(-6.19, -30.87) * mm, "end": v(-6.16, -30.8) * mm});
            skLineSegment(sketch, "E667", {"start": v(-6.16, -30.8) * mm, "end": v(-6.13, -30.73) * mm});
            skLineSegment(sketch, "E668", {"start": v(-6.13, -30.73) * mm, "end": v(-6.1, -30.67) * mm});
            skLineSegment(sketch, "E669", {"start": v(-6.1, -30.67) * mm, "end": v(-6.08, -30.61) * mm});
            skLineSegment(sketch, "E670", {"start": v(-6.08, -30.61) * mm, "end": v(-6.06, -30.56) * mm});
            skLineSegment(sketch, "E671", {"start": v(-6.06, -30.56) * mm, "end": v(-6.04, -30.5) * mm});
            skLineSegment(sketch, "E672", {"start": v(-6.04, -30.5) * mm, "end": v(-6.03, -30.46) * mm});
            skLineSegment(sketch, "E673", {"start": v(-6.03, -30.46) * mm, "end": v(-6.01, -30.42) * mm});
            skLineSegment(sketch, "E674", {"start": v(-6.01, -30.42) * mm, "end": v(-6, -30.38) * mm});
            skLineSegment(sketch, "E675", {"start": v(-6, -30.38) * mm, "end": v(-5.99, -30.34) * mm});
            skLineSegment(sketch, "E676", {"start": v(-5.99, -30.34) * mm, "end": v(-5.98, -30.3) * mm});
            skLineSegment(sketch, "E677", {"start": v(-5.98, -30.3) * mm, "end": v(-5.97, -30.28) * mm});
            skLineSegment(sketch, "E678", {"start": v(-5.97, -30.28) * mm, "end": v(-5.96, -30.26) * mm});
            skLineSegment(sketch, "E679", {"start": v(-5.96, -30.26) * mm, "end": v(-5.96, -30.24) * mm});
            skLineSegment(sketch, "E680", {"start": v(-5.96, -30.24) * mm, "end": v(-5.95, -30.22) * mm});
            skLineSegment(sketch, "E681", {"start": v(-5.95, -30.22) * mm, "end": v(-5.95, -30.2) * mm});
            skLineSegment(sketch, "E682", {"start": v(-5.95, -30.2) * mm, "end": v(-5.95, -30.2) * mm});
            skLineSegment(sketch, "E683", {"start": v(-5.95, -30.2) * mm, "end": v(-5.85, -29.67) * mm});
            skLineSegment(sketch, "E684", {"start": v(-5.85, -29.67) * mm, "end": v(-3.55, -30.03) * mm});
            skLineSegment(sketch, "E685", {"start": v(-3.55, -30.03) * mm, "end": v(-3.6, -30.57) * mm});
            skLineSegment(sketch, "E686", {"start": v(-3.6, -30.57) * mm, "end": v(-3.61, -30.58) * mm});
            skLineSegment(sketch, "E687", {"start": v(-3.61, -30.58) * mm, "end": v(-3.61, -30.59) * mm});
            skLineSegment(sketch, "E688", {"start": v(-3.61, -30.59) * mm, "end": v(-3.61, -30.6) * mm});
            skLineSegment(sketch, "E689", {"start": v(-3.61, -30.6) * mm, "end": v(-3.61, -30.63) * mm});
            skLineSegment(sketch, "E690", {"start": v(-3.61, -30.63) * mm, "end": v(-3.61, -30.65) * mm});
            skLineSegment(sketch, "E691", {"start": v(-3.61, -30.65) * mm, "end": v(-3.62, -30.68) * mm});
            skLineSegment(sketch, "E692", {"start": v(-3.62, -30.68) * mm, "end": v(-3.62, -30.71) * mm});
            skLineSegment(sketch, "E693", {"start": v(-3.62, -30.71) * mm, "end": v(-3.62, -30.75) * mm});
            skLineSegment(sketch, "E694", {"start": v(-3.62, -30.75) * mm, "end": v(-3.62, -30.8) * mm});
            skLineSegment(sketch, "E695", {"start": v(-3.62, -30.8) * mm, "end": v(-3.62, -30.84) * mm});
            skLineSegment(sketch, "E696", {"start": v(-3.62, -30.84) * mm, "end": v(-3.62, -30.89) * mm});
            skLineSegment(sketch, "E697", {"start": v(-3.62, -30.89) * mm, "end": v(-3.61, -30.94) * mm});
            skLineSegment(sketch, "E698", {"start": v(-3.61, -30.94) * mm, "end": v(-3.61, -31) * mm});
            skLineSegment(sketch, "E699", {"start": v(-3.61, -31) * mm, "end": v(-3.6, -31.06) * mm});
            skLineSegment(sketch, "E700", {"start": v(-3.6, -31.06) * mm, "end": v(-3.6, -31.13) * mm});
            skLineSegment(sketch, "E701", {"start": v(-3.6, -31.13) * mm, "end": v(-3.6, -31.2) * mm});
            skLineSegment(sketch, "E702", {"start": v(-3.6, -31.2) * mm, "end": v(-3.6, -31.27) * mm});
            skLineSegment(sketch, "E703", {"start": v(-3.6, -31.27) * mm, "end": v(-3.58, -31.35) * mm});
            skLineSegment(sketch, "E704", {"start": v(-3.58, -31.35) * mm, "end": v(-3.57, -31.44) * mm});
            skLineSegment(sketch, "E705", {"start": v(-3.57, -31.44) * mm, "end": v(-3.56, -31.52) * mm});
            skLineSegment(sketch, "E706", {"start": v(-3.56, -31.52) * mm, "end": v(-3.55, -31.61) * mm});
            skLineSegment(sketch, "E707", {"start": v(-3.55, -31.61) * mm, "end": v(-3.53, -31.7) * mm});
            skLineSegment(sketch, "E708", {"start": v(-3.53, -31.7) * mm, "end": v(-3.52, -31.8) * mm});
            skLineSegment(sketch, "E709", {"start": v(-3.52, -31.8) * mm, "end": v(-3.5, -31.9) * mm});
            skLineSegment(sketch, "E710", {"start": v(-3.5, -31.9) * mm, "end": v(-3.48, -32.02) * mm});
            skLineSegment(sketch, "E711", {"start": v(-3.48, -32.02) * mm, "end": v(-3.46, -32.13) * mm});
            skLineSegment(sketch, "E712", {"start": v(-3.46, -32.13) * mm, "end": v(-3.43, -32.24) * mm});
            skLineSegment(sketch, "E713", {"start": v(-3.43, -32.24) * mm, "end": v(-3.4, -32.36) * mm});
            skLineSegment(sketch, "E714", {"start": v(-3.4, -32.36) * mm, "end": v(-3.38, -32.48) * mm});
            skLineSegment(sketch, "E715", {"start": v(-3.38, -32.48) * mm, "end": v(-3.35, -32.6) * mm});
            skLineSegment(sketch, "E716", {"start": v(-3.35, -32.6) * mm, "end": v(-3.31, -32.73) * mm});
            skLineSegment(sketch, "E717", {"start": v(-3.31, -32.73) * mm, "end": v(-3.28, -32.87) * mm});
            skLineSegment(sketch, "E718", {"start": v(-3.28, -32.87) * mm, "end": v(-3.24, -33) * mm});
            skLineSegment(sketch, "E719", {"start": v(-3.24, -33) * mm, "end": v(-3.2, -33.14) * mm});
            skLineSegment(sketch, "E720", {"start": v(-3.2, -33.14) * mm, "end": v(-3.15, -33.29) * mm});
            skLineSegment(sketch, "E721", {"start": v(-3.15, -33.29) * mm, "end": v(-3.1, -33.43) * mm});
            skLineSegment(sketch, "E722", {"start": v(-3.1, -33.43) * mm, "end": v(-3.06, -33.58) * mm});
            skLineSegment(sketch, "E723", {"start": v(-3.06, -33.58) * mm, "end": v(-3, -33.74) * mm});
            skLineSegment(sketch, "E724", {"start": v(-3, -33.74) * mm, "end": v(-2.95, -33.9) * mm});
            skLineSegment(sketch, "E725", {"start": v(-2.95, -33.9) * mm, "end": v(-2.89, -34.05) * mm});
            skLineSegment(sketch, "E726", {"start": v(-2.89, -34.05) * mm, "end": v(-2.82, -34.22) * mm});
            skLineSegment(sketch, "E727", {"start": v(-2.82, -34.22) * mm, "end": v(-2.75, -34.38) * mm});
            skLineSegment(sketch, "E728", {"start": v(-2.75, -34.38) * mm, "end": v(-2.68, -34.55) * mm});
            skLineSegment(sketch, "E729", {"start": v(-2.68, -34.55) * mm, "end": v(-2.61, -34.72) * mm});
            skLineSegment(sketch, "E730", {"start": v(-2.61, -34.72) * mm, "end": v(-2.53, -34.84) * mm});
            skLineSegment(sketch, "E731", {"start": v(-2.53, -34.84) * mm, "end": v(-1.05, -34.92) * mm});
            skLineSegment(sketch, "E732", {"start": v(-1.05, -34.92) * mm, "end": v(-0.96, -34.8) * mm});
            skLineSegment(sketch, "E733", {"start": v(-0.96, -34.8) * mm, "end": v(-0.87, -34.64) * mm});
            skLineSegment(sketch, "E734", {"start": v(-0.87, -34.64) * mm, "end": v(-0.78, -34.48) * mm});
            skLineSegment(sketch, "E735", {"start": v(-0.78, -34.48) * mm, "end": v(-0.7, -34.33) * mm});
            skLineSegment(sketch, "E736", {"start": v(-0.7, -34.33) * mm, "end": v(-0.62, -34.17) * mm});
            skLineSegment(sketch, "E737", {"start": v(-0.62, -34.17) * mm, "end": v(-0.54, -34.02) * mm});
            skLineSegment(sketch, "E738", {"start": v(-0.54, -34.02) * mm, "end": v(-0.47, -33.87) * mm});
            skLineSegment(sketch, "E739", {"start": v(-0.47, -33.87) * mm, "end": v(-0.4, -33.72) * mm});
            skLineSegment(sketch, "E740", {"start": v(-0.4, -33.72) * mm, "end": v(-0.34, -33.58) * mm});
            skLineSegment(sketch, "E741", {"start": v(-0.34, -33.58) * mm, "end": v(-0.27, -33.43) * mm});
            skLineSegment(sketch, "E742", {"start": v(-0.27, -33.43) * mm, "end": v(-0.21, -33.3) * mm});
            skLineSegment(sketch, "E743", {"start": v(-0.21, -33.3) * mm, "end": v(-0.16, -33.16) * mm});
            skLineSegment(sketch, "E744", {"start": v(-0.16, -33.16) * mm, "end": v(-0.1, -33.03) * mm});
            skLineSegment(sketch, "E745", {"start": v(-0.1, -33.03) * mm, "end": v(-0.06, -32.9) * mm});
            skLineSegment(sketch, "E746", {"start": v(-0.06, -32.9) * mm, "end": v(0, -32.78) * mm});
            skLineSegment(sketch, "E747", {"start": v(0, -32.78) * mm, "end": v(0.03, -32.66) * mm});
            skLineSegment(sketch, "E748", {"start": v(0.03, -32.66) * mm, "end": v(0.07, -32.54) * mm});
            skLineSegment(sketch, "E749", {"start": v(0.07, -32.54) * mm, "end": v(0.11, -32.42) * mm});
            skLineSegment(sketch, "E750", {"start": v(0.11, -32.42) * mm, "end": v(0.15, -32.31) * mm});
            skLineSegment(sketch, "E751", {"start": v(0.15, -32.31) * mm, "end": v(0.18, -32.2) * mm});
            skLineSegment(sketch, "E752", {"start": v(0.18, -32.2) * mm, "end": v(0.21, -32.1) * mm});
            skLineSegment(sketch, "E753", {"start": v(0.21, -32.1) * mm, "end": v(0.24, -32) * mm});
            skLineSegment(sketch, "E754", {"start": v(0.24, -32) * mm, "end": v(0.27, -31.9) * mm});
            skLineSegment(sketch, "E755", {"start": v(0.27, -31.9) * mm, "end": v(0.3, -31.81) * mm});
            skLineSegment(sketch, "E756", {"start": v(0.3, -31.81) * mm, "end": v(0.31, -31.72) * mm});
            skLineSegment(sketch, "E757", {"start": v(0.31, -31.72) * mm, "end": v(0.33, -31.64) * mm});
            skLineSegment(sketch, "E758", {"start": v(0.33, -31.64) * mm, "end": v(0.35, -31.56) * mm});
            skLineSegment(sketch, "E759", {"start": v(0.35, -31.56) * mm, "end": v(0.37, -31.48) * mm});
            skLineSegment(sketch, "E760", {"start": v(0.37, -31.48) * mm, "end": v(0.38, -31.4) * mm});
            skLineSegment(sketch, "E761", {"start": v(0.38, -31.4) * mm, "end": v(0.4, -31.33) * mm});
            skLineSegment(sketch, "E762", {"start": v(0.4, -31.33) * mm, "end": v(0.4, -31.27) * mm});
            skLineSegment(sketch, "E763", {"start": v(0.4, -31.27) * mm, "end": v(0.42, -31.2) * mm});
            skLineSegment(sketch, "E764", {"start": v(0.42, -31.2) * mm, "end": v(0.42, -31.15) * mm});
            skLineSegment(sketch, "E765", {"start": v(0.42, -31.15) * mm, "end": v(0.43, -31.1) * mm});
            skLineSegment(sketch, "E766", {"start": v(0.43, -31.1) * mm, "end": v(0.44, -31.05) * mm});
            skLineSegment(sketch, "E767", {"start": v(0.44, -31.05) * mm, "end": v(0.44, -31) * mm});
            skLineSegment(sketch, "E768", {"start": v(0.44, -31) * mm, "end": v(0.45, -30.96) * mm});
            skLineSegment(sketch, "E769", {"start": v(0.45, -30.96) * mm, "end": v(0.45, -30.92) * mm});
            skLineSegment(sketch, "E770", {"start": v(0.45, -30.92) * mm, "end": v(0.45, -30.89) * mm});
            skLineSegment(sketch, "E771", {"start": v(0.45, -30.89) * mm, "end": v(0.46, -30.86) * mm});
            skLineSegment(sketch, "E772", {"start": v(0.46, -30.86) * mm, "end": v(0.46, -30.83) * mm});
            skLineSegment(sketch, "E773", {"start": v(0.46, -30.83) * mm, "end": v(0.46, -30.81) * mm});
            skLineSegment(sketch, "E774", {"start": v(0.46, -30.81) * mm, "end": v(0.46, -30.8) * mm});
            skLineSegment(sketch, "E775", {"start": v(0.46, -30.8) * mm, "end": v(0.46, -30.78) * mm});
            skLineSegment(sketch, "E776", {"start": v(0.46, -30.78) * mm, "end": v(0.46, -30.78) * mm});
            skLineSegment(sketch, "E777", {"start": v(0.46, -30.78) * mm, "end": v(0.45, -30.24) * mm});
            skLineSegment(sketch, "E778", {"start": v(0.45, -30.24) * mm, "end": v(2.77, -30.11) * mm});
            skLineSegment(sketch, "E779", {"start": v(2.77, -30.11) * mm, "end": v(2.82, -30.65) * mm});
            skLineSegment(sketch, "E780", {"start": v(2.82, -30.65) * mm, "end": v(2.83, -30.66) * mm});
            skLineSegment(sketch, "E781", {"start": v(2.83, -30.66) * mm, "end": v(2.83, -30.67) * mm});
            skLineSegment(sketch, "E782", {"start": v(2.83, -30.67) * mm, "end": v(2.83, -30.69) * mm});
            skLineSegment(sketch, "E783", {"start": v(2.83, -30.69) * mm, "end": v(2.83, -30.7) * mm});
            skLineSegment(sketch, "E784", {"start": v(2.83, -30.7) * mm, "end": v(2.84, -30.73) * mm});
            skLineSegment(sketch, "E785", {"start": v(2.84, -30.73) * mm, "end": v(2.84, -30.76) * mm});
            skLineSegment(sketch, "E786", {"start": v(2.84, -30.76) * mm, "end": v(2.85, -30.8) * mm});
            skLineSegment(sketch, "E787", {"start": v(2.85, -30.8) * mm, "end": v(2.86, -30.83) * mm});
            skLineSegment(sketch, "E788", {"start": v(2.86, -30.83) * mm, "end": v(2.86, -30.87) * mm});
            skLineSegment(sketch, "E789", {"start": v(2.86, -30.87) * mm, "end": v(2.87, -30.92) * mm});
            skLineSegment(sketch, "E790", {"start": v(2.87, -30.92) * mm, "end": v(2.89, -30.96) * mm});
            skLineSegment(sketch, "E791", {"start": v(2.89, -30.96) * mm, "end": v(2.9, -31.02) * mm});
            skLineSegment(sketch, "E792", {"start": v(2.9, -31.02) * mm, "end": v(2.91, -31.07) * mm});
            skLineSegment(sketch, "E793", {"start": v(2.91, -31.07) * mm, "end": v(2.93, -31.13) * mm});
            skLineSegment(sketch, "E794", {"start": v(2.93, -31.13) * mm, "end": v(2.95, -31.2) * mm});
            skLineSegment(sketch, "E795", {"start": v(2.95, -31.2) * mm, "end": v(2.97, -31.27) * mm});
            skLineSegment(sketch, "E796", {"start": v(2.97, -31.27) * mm, "end": v(3, -31.34) * mm});
            skLineSegment(sketch, "E797", {"start": v(3, -31.34) * mm, "end": v(3.01, -31.41) * mm});
            skLineSegment(sketch, "E798", {"start": v(3.01, -31.41) * mm, "end": v(3.04, -31.5) * mm});
            skLineSegment(sketch, "E799", {"start": v(3.04, -31.5) * mm, "end": v(3.07, -31.57) * mm});
            skLineSegment(sketch, "E800", {"start": v(3.07, -31.57) * mm, "end": v(3.1, -31.66) * mm});
            skLineSegment(sketch, "E801", {"start": v(3.1, -31.66) * mm, "end": v(3.13, -31.75) * mm});
            skLineSegment(sketch, "E802", {"start": v(3.13, -31.75) * mm, "end": v(3.17, -31.84) * mm});
            skLineSegment(sketch, "E803", {"start": v(3.17, -31.84) * mm, "end": v(3.21, -31.94) * mm});
            skLineSegment(sketch, "E804", {"start": v(3.21, -31.94) * mm, "end": v(3.25, -32.04) * mm});
            skLineSegment(sketch, "E805", {"start": v(3.25, -32.04) * mm, "end": v(3.3, -32.14) * mm});
            skLineSegment(sketch, "E806", {"start": v(3.3, -32.14) * mm, "end": v(3.34, -32.25) * mm});
            skLineSegment(sketch, "E807", {"start": v(3.34, -32.25) * mm, "end": v(3.4, -32.36) * mm});
            skLineSegment(sketch, "E808", {"start": v(3.4, -32.36) * mm, "end": v(3.45, -32.47) * mm});
            skLineSegment(sketch, "E809", {"start": v(3.45, -32.47) * mm, "end": v(3.5, -32.59) * mm});
            skLineSegment(sketch, "E810", {"start": v(3.5, -32.59) * mm, "end": v(3.56, -32.7) * mm});
            skLineSegment(sketch, "E811", {"start": v(3.56, -32.7) * mm, "end": v(3.63, -32.83) * mm});
            skLineSegment(sketch, "E812", {"start": v(3.63, -32.83) * mm, "end": v(3.7, -32.96) * mm});
            skLineSegment(sketch, "E813", {"start": v(3.7, -32.96) * mm, "end": v(3.76, -33.08) * mm});
            skLineSegment(sketch, "E814", {"start": v(3.76, -33.08) * mm, "end": v(3.84, -33.21) * mm});
            skLineSegment(sketch, "E815", {"start": v(3.84, -33.21) * mm, "end": v(3.91, -33.35) * mm});
            skLineSegment(sketch, "E816", {"start": v(3.91, -33.35) * mm, "end": v(4, -33.48) * mm});
            skLineSegment(sketch, "E817", {"start": v(4, -33.48) * mm, "end": v(4.08, -33.62) * mm});
            skLineSegment(sketch, "E818", {"start": v(4.08, -33.62) * mm, "end": v(4.17, -33.76) * mm});
            skLineSegment(sketch, "E819", {"start": v(4.17, -33.76) * mm, "end": v(4.26, -33.9) * mm});
            skLineSegment(sketch, "E820", {"start": v(4.26, -33.9) * mm, "end": v(4.35, -34.06) * mm});
            skLineSegment(sketch, "E821", {"start": v(4.35, -34.06) * mm, "end": v(4.45, -34.2) * mm});
            skLineSegment(sketch, "E822", {"start": v(4.45, -34.2) * mm, "end": v(4.56, -34.35) * mm});
            skLineSegment(sketch, "E823", {"start": v(4.56, -34.35) * mm, "end": v(4.67, -34.5) * mm});
            skLineSegment(sketch, "E824", {"start": v(4.67, -34.5) * mm, "end": v(4.77, -34.6) * mm});
            skLineSegment(sketch, "E825", {"start": v(4.77, -34.6) * mm, "end": v(6.23, -34.37) * mm});
            skLineSegment(sketch, "E826", {"start": v(6.23, -34.37) * mm, "end": v(6.3, -34.25) * mm});
            skLineSegment(sketch, "E827", {"start": v(6.3, -34.25) * mm, "end": v(6.35, -34.07) * mm});
            skLineSegment(sketch, "E828", {"start": v(6.35, -34.07) * mm, "end": v(6.4, -33.9) * mm});
            skLineSegment(sketch, "E829", {"start": v(6.4, -33.9) * mm, "end": v(6.45, -33.72) * mm});
            skLineSegment(sketch, "E830", {"start": v(6.45, -33.72) * mm, "end": v(6.5, -33.55) * mm});
            skLineSegment(sketch, "E831", {"start": v(6.5, -33.55) * mm, "end": v(6.54, -33.39) * mm});
            skLineSegment(sketch, "E832", {"start": v(6.54, -33.39) * mm, "end": v(6.58, -33.22) * mm});
            skLineSegment(sketch, "E833", {"start": v(6.58, -33.22) * mm, "end": v(6.62, -33.07) * mm});
            skLineSegment(sketch, "E834", {"start": v(6.62, -33.07) * mm, "end": v(6.65, -32.91) * mm});
            skLineSegment(sketch, "E835", {"start": v(6.65, -32.91) * mm, "end": v(6.68, -32.76) * mm});
            skLineSegment(sketch, "E836", {"start": v(6.68, -32.76) * mm, "end": v(6.71, -32.61) * mm});
            skLineSegment(sketch, "E837", {"start": v(6.71, -32.61) * mm, "end": v(6.74, -32.47) * mm});
            skLineSegment(sketch, "E838", {"start": v(6.74, -32.47) * mm, "end": v(6.76, -32.33) * mm});
            skLineSegment(sketch, "E839", {"start": v(6.76, -32.33) * mm, "end": v(6.79, -32.2) * mm});
            skLineSegment(sketch, "E840", {"start": v(6.79, -32.2) * mm, "end": v(6.8, -32.06) * mm});
            skLineSegment(sketch, "E841", {"start": v(6.8, -32.06) * mm, "end": v(6.82, -31.93) * mm});
            skLineSegment(sketch, "E842", {"start": v(6.82, -31.93) * mm, "end": v(6.84, -31.81) * mm});
            skLineSegment(sketch, "E843", {"start": v(6.84, -31.81) * mm, "end": v(6.85, -31.7) * mm});
            skLineSegment(sketch, "E844", {"start": v(6.85, -31.7) * mm, "end": v(6.86, -31.57) * mm});
            skLineSegment(sketch, "E845", {"start": v(6.86, -31.57) * mm, "end": v(6.87, -31.46) * mm});
            skLineSegment(sketch, "E846", {"start": v(6.87, -31.46) * mm, "end": v(6.88, -31.35) * mm});
            skLineSegment(sketch, "E847", {"start": v(6.88, -31.35) * mm, "end": v(6.89, -31.25) * mm});
            skLineSegment(sketch, "E848", {"start": v(6.89, -31.25) * mm, "end": v(6.9, -31.15) * mm});
            skLineSegment(sketch, "E849", {"start": v(6.9, -31.15) * mm, "end": v(6.9, -31.06) * mm});
            skLineSegment(sketch, "E850", {"start": v(6.9, -31.06) * mm, "end": v(6.9, -30.96) * mm});
            skLineSegment(sketch, "E851", {"start": v(6.9, -30.96) * mm, "end": v(6.9, -30.88) * mm});
            skLineSegment(sketch, "E852", {"start": v(6.9, -30.88) * mm, "end": v(6.9, -30.8) * mm});
            skLineSegment(sketch, "E853", {"start": v(6.9, -30.8) * mm, "end": v(6.9, -30.71) * mm});
            skLineSegment(sketch, "E854", {"start": v(6.9, -30.71) * mm, "end": v(6.9, -30.64) * mm});
            skLineSegment(sketch, "E855", {"start": v(6.9, -30.64) * mm, "end": v(6.9, -30.57) * mm});
            skLineSegment(sketch, "E856", {"start": v(6.9, -30.57) * mm, "end": v(6.9, -30.5) * mm});
            skLineSegment(sketch, "E857", {"start": v(6.9, -30.5) * mm, "end": v(6.9, -30.44) * mm});
            skLineSegment(sketch, "E858", {"start": v(6.9, -30.44) * mm, "end": v(6.9, -30.38) * mm});
            skLineSegment(sketch, "E859", {"start": v(6.9, -30.38) * mm, "end": v(6.89, -30.33) * mm});
            skLineSegment(sketch, "E860", {"start": v(6.89, -30.33) * mm, "end": v(6.88, -30.28) * mm});
            skLineSegment(sketch, "E861", {"start": v(6.88, -30.28) * mm, "end": v(6.88, -30.23) * mm});
            skLineSegment(sketch, "E862", {"start": v(6.88, -30.23) * mm, "end": v(6.87, -30.19) * mm});
            skLineSegment(sketch, "E863", {"start": v(6.87, -30.19) * mm, "end": v(6.87, -30.15) * mm});
            skLineSegment(sketch, "E864", {"start": v(6.87, -30.15) * mm, "end": v(6.87, -30.12) * mm});
            skLineSegment(sketch, "E865", {"start": v(6.87, -30.12) * mm, "end": v(6.86, -30.1) * mm});
            skLineSegment(sketch, "E866", {"start": v(6.86, -30.1) * mm, "end": v(6.86, -30.07) * mm});
            skLineSegment(sketch, "E867", {"start": v(6.86, -30.07) * mm, "end": v(6.85, -30.05) * mm});
            skLineSegment(sketch, "E868", {"start": v(6.85, -30.05) * mm, "end": v(6.85, -30.03) * mm});
            skLineSegment(sketch, "E869", {"start": v(6.85, -30.03) * mm, "end": v(6.85, -30.02) * mm});
            skLineSegment(sketch, "E870", {"start": v(6.85, -30.02) * mm, "end": v(6.85, -30) * mm});
            skLineSegment(sketch, "E871", {"start": v(6.85, -30) * mm, "end": v(6.73, -29.48) * mm});
            skLineSegment(sketch, "E872", {"start": v(6.73, -29.48) * mm, "end": v(8.97, -28.88) * mm});
            skLineSegment(sketch, "E873", {"start": v(8.97, -28.88) * mm, "end": v(9.14, -29.4) * mm});
            skLineSegment(sketch, "E874", {"start": v(9.14, -29.4) * mm, "end": v(9.14, -29.4) * mm});
            skLineSegment(sketch, "E875", {"start": v(9.14, -29.4) * mm, "end": v(9.14, -29.41) * mm});
            skLineSegment(sketch, "E876", {"start": v(9.14, -29.41) * mm, "end": v(9.15, -29.43) * mm});
            skLineSegment(sketch, "E877", {"start": v(9.15, -29.43) * mm, "end": v(9.16, -29.45) * mm});
            skLineSegment(sketch, "E878", {"start": v(9.16, -29.45) * mm, "end": v(9.16, -29.47) * mm});
            skLineSegment(sketch, "E879", {"start": v(9.16, -29.47) * mm, "end": v(9.18, -29.5) * mm});
            skLineSegment(sketch, "E880", {"start": v(9.18, -29.5) * mm, "end": v(9.19, -29.53) * mm});
            skLineSegment(sketch, "E881", {"start": v(9.19, -29.53) * mm, "end": v(9.2, -29.56) * mm});
            skLineSegment(sketch, "E882", {"start": v(9.2, -29.56) * mm, "end": v(9.22, -29.6) * mm});
            skLineSegment(sketch, "E883", {"start": v(9.22, -29.6) * mm, "end": v(9.24, -29.64) * mm});
            skLineSegment(sketch, "E884", {"start": v(9.24, -29.64) * mm, "end": v(9.26, -29.69) * mm});
            skLineSegment(sketch, "E885", {"start": v(9.26, -29.69) * mm, "end": v(9.28, -29.74) * mm});
            skLineSegment(sketch, "E886", {"start": v(9.28, -29.74) * mm, "end": v(9.3, -29.79) * mm});
            skLineSegment(sketch, "E887", {"start": v(9.3, -29.79) * mm, "end": v(9.34, -29.84) * mm});
            skLineSegment(sketch, "E888", {"start": v(9.34, -29.84) * mm, "end": v(9.37, -29.9) * mm});
            skLineSegment(sketch, "E889", {"start": v(9.37, -29.9) * mm, "end": v(9.4, -29.97) * mm});
            skLineSegment(sketch, "E890", {"start": v(9.4, -29.97) * mm, "end": v(9.44, -30.03) * mm});
            skLineSegment(sketch, "E891", {"start": v(9.44, -30.03) * mm, "end": v(9.48, -30.1) * mm});
            skLineSegment(sketch, "E892", {"start": v(9.48, -30.1) * mm, "end": v(9.52, -30.17) * mm});
            skLineSegment(sketch, "E893", {"start": v(9.52, -30.17) * mm, "end": v(9.57, -30.25) * mm});
            skLineSegment(sketch, "E894", {"start": v(9.57, -30.25) * mm, "end": v(9.62, -30.32) * mm});
            skLineSegment(sketch, "E895", {"start": v(9.62, -30.32) * mm, "end": v(9.67, -30.4) * mm});
            skLineSegment(sketch, "E896", {"start": v(9.67, -30.4) * mm, "end": v(9.72, -30.49) * mm});
            skLineSegment(sketch, "E897", {"start": v(9.72, -30.49) * mm, "end": v(9.78, -30.57) * mm});
            skLineSegment(sketch, "E898", {"start": v(9.78, -30.57) * mm, "end": v(9.84, -30.66) * mm});
            skLineSegment(sketch, "E899", {"start": v(9.84, -30.66) * mm, "end": v(9.9, -30.76) * mm});
            skLineSegment(sketch, "E900", {"start": v(9.9, -30.76) * mm, "end": v(9.98, -30.85) * mm});
            skLineSegment(sketch, "E901", {"start": v(9.98, -30.85) * mm, "end": v(10.05, -30.95) * mm});
            skLineSegment(sketch, "E902", {"start": v(10.05, -30.95) * mm, "end": v(10.12, -31.05) * mm});
            skLineSegment(sketch, "E903", {"start": v(10.12, -31.05) * mm, "end": v(10.2, -31.15) * mm});
            skLineSegment(sketch, "E904", {"start": v(10.2, -31.15) * mm, "end": v(10.29, -31.25) * mm});
            skLineSegment(sketch, "E905", {"start": v(10.29, -31.25) * mm, "end": v(10.37, -31.36) * mm});
            skLineSegment(sketch, "E906", {"start": v(10.37, -31.36) * mm, "end": v(10.46, -31.47) * mm});
            skLineSegment(sketch, "E907", {"start": v(10.46, -31.47) * mm, "end": v(10.56, -31.58) * mm});
            skLineSegment(sketch, "E908", {"start": v(10.56, -31.58) * mm, "end": v(10.66, -31.7) * mm});
            skLineSegment(sketch, "E909", {"start": v(10.66, -31.7) * mm, "end": v(10.76, -31.8) * mm});
            skLineSegment(sketch, "E910", {"start": v(10.76, -31.8) * mm, "end": v(10.87, -31.92) * mm});
            skLineSegment(sketch, "E911", {"start": v(10.87, -31.92) * mm, "end": v(10.98, -32.04) * mm});
            skLineSegment(sketch, "E912", {"start": v(10.98, -32.04) * mm, "end": v(11.1, -32.16) * mm});
            skLineSegment(sketch, "E913", {"start": v(11.1, -32.16) * mm, "end": v(11.21, -32.28) * mm});
            skLineSegment(sketch, "E914", {"start": v(11.21, -32.28) * mm, "end": v(11.34, -32.4) * mm});
            skLineSegment(sketch, "E915", {"start": v(11.34, -32.4) * mm, "end": v(11.47, -32.53) * mm});
            skLineSegment(sketch, "E916", {"start": v(11.47, -32.53) * mm, "end": v(11.6, -32.66) * mm});
            skLineSegment(sketch, "E917", {"start": v(11.6, -32.66) * mm, "end": v(11.74, -32.78) * mm});
            skLineSegment(sketch, "E918", {"start": v(11.74, -32.78) * mm, "end": v(11.86, -32.86) * mm});
            skLineSegment(sketch, "E919", {"start": v(11.86, -32.86) * mm, "end": v(13.24, -32.33) * mm});
            skLineSegment(sketch, "E920", {"start": v(13.24, -32.33) * mm, "end": v(13.28, -32.2) * mm});
            skLineSegment(sketch, "E921", {"start": v(13.28, -32.2) * mm, "end": v(13.3, -32) * mm});
            skLineSegment(sketch, "E922", {"start": v(13.3, -32) * mm, "end": v(13.31, -31.82) * mm});
            skLineSegment(sketch, "E923", {"start": v(13.31, -31.82) * mm, "end": v(13.32, -31.64) * mm});
            skLineSegment(sketch, "E924", {"start": v(13.32, -31.64) * mm, "end": v(13.33, -31.47) * mm});
            skLineSegment(sketch, "E925", {"start": v(13.33, -31.47) * mm, "end": v(13.34, -31.3) * mm});
            skLineSegment(sketch, "E926", {"start": v(13.34, -31.3) * mm, "end": v(13.35, -31.13) * mm});
            skLineSegment(sketch, "E927", {"start": v(13.35, -31.13) * mm, "end": v(13.35, -30.97) * mm});
            skLineSegment(sketch, "E928", {"start": v(13.35, -30.97) * mm, "end": v(13.35, -30.8) * mm});
            skLineSegment(sketch, "E929", {"start": v(13.35, -30.8) * mm, "end": v(13.35, -30.65) * mm});
            skLineSegment(sketch, "E930", {"start": v(13.35, -30.65) * mm, "end": v(13.35, -30.5) * mm});
            skLineSegment(sketch, "E931", {"start": v(13.35, -30.5) * mm, "end": v(13.34, -30.36) * mm});
            skLineSegment(sketch, "E932", {"start": v(13.34, -30.36) * mm, "end": v(13.34, -30.22) * mm});
            skLineSegment(sketch, "E933", {"start": v(13.34, -30.22) * mm, "end": v(13.33, -30.08) * mm});
            skLineSegment(sketch, "E934", {"start": v(13.33, -30.08) * mm, "end": v(13.32, -29.95) * mm});
            skLineSegment(sketch, "E935", {"start": v(13.32, -29.95) * mm, "end": v(13.31, -29.82) * mm});
            skLineSegment(sketch, "E936", {"start": v(13.31, -29.82) * mm, "end": v(13.3, -29.7) * mm});
            skLineSegment(sketch, "E937", {"start": v(13.3, -29.7) * mm, "end": v(13.3, -29.57) * mm});
            skLineSegment(sketch, "E938", {"start": v(13.3, -29.57) * mm, "end": v(13.28, -29.46) * mm});
            skLineSegment(sketch, "E939", {"start": v(13.28, -29.46) * mm, "end": v(13.27, -29.35) * mm});
            skLineSegment(sketch, "E940", {"start": v(13.27, -29.35) * mm, "end": v(13.25, -29.24) * mm});
            skLineSegment(sketch, "E941", {"start": v(13.25, -29.24) * mm, "end": v(13.24, -29.14) * mm});
            skLineSegment(sketch, "E942", {"start": v(13.24, -29.14) * mm, "end": v(13.22, -29.04) * mm});
            skLineSegment(sketch, "E943", {"start": v(13.22, -29.04) * mm, "end": v(13.2, -28.94) * mm});
            skLineSegment(sketch, "E944", {"start": v(13.2, -28.94) * mm, "end": v(13.19, -28.85) * mm});
            skLineSegment(sketch, "E945", {"start": v(13.19, -28.85) * mm, "end": v(13.17, -28.77) * mm});
            skLineSegment(sketch, "E946", {"start": v(13.17, -28.77) * mm, "end": v(13.16, -28.68) * mm});
            skLineSegment(sketch, "E947", {"start": v(13.16, -28.68) * mm, "end": v(13.14, -28.6) * mm});
            skLineSegment(sketch, "E948", {"start": v(13.14, -28.6) * mm, "end": v(13.12, -28.53) * mm});
            skLineSegment(sketch, "E949", {"start": v(13.12, -28.53) * mm, "end": v(13.1, -28.46) * mm});
            skLineSegment(sketch, "E950", {"start": v(13.1, -28.46) * mm, "end": v(13.09, -28.4) * mm});
            skLineSegment(sketch, "E951", {"start": v(13.09, -28.4) * mm, "end": v(13.07, -28.34) * mm});
            skLineSegment(sketch, "E952", {"start": v(13.07, -28.34) * mm, "end": v(13.06, -28.28) * mm});
            skLineSegment(sketch, "E953", {"start": v(13.06, -28.28) * mm, "end": v(13.04, -28.23) * mm});
            skLineSegment(sketch, "E954", {"start": v(13.04, -28.23) * mm, "end": v(13.03, -28.18) * mm});
            skLineSegment(sketch, "E955", {"start": v(13.03, -28.18) * mm, "end": v(13.01, -28.14) * mm});
            skLineSegment(sketch, "E956", {"start": v(13.01, -28.14) * mm, "end": v(13, -28.1) * mm});
            skLineSegment(sketch, "E957", {"start": v(13, -28.1) * mm, "end": v(12.99, -28.07) * mm});
            skLineSegment(sketch, "E958", {"start": v(12.99, -28.07) * mm, "end": v(12.98, -28.03) * mm});
            skLineSegment(sketch, "E959", {"start": v(12.98, -28.03) * mm, "end": v(12.97, -28) * mm});
            skLineSegment(sketch, "E960", {"start": v(12.97, -28) * mm, "end": v(12.96, -27.98) * mm});
            skLineSegment(sketch, "E961", {"start": v(12.96, -27.98) * mm, "end": v(12.95, -27.96) * mm});
            skLineSegment(sketch, "E962", {"start": v(12.95, -27.96) * mm, "end": v(12.95, -27.95) * mm});
            skLineSegment(sketch, "E963", {"start": v(12.95, -27.95) * mm, "end": v(12.94, -27.94) * mm});
            skLineSegment(sketch, "E964", {"start": v(12.94, -27.94) * mm, "end": v(12.94, -27.93) * mm});
            skLineSegment(sketch, "E965", {"start": v(12.94, -27.93) * mm, "end": v(12.7, -27.44) * mm});
            skLineSegment(sketch, "E966", {"start": v(12.7, -27.44) * mm, "end": v(14.78, -26.38) * mm});
            skLineSegment(sketch, "E967", {"start": v(14.78, -26.38) * mm, "end": v(15.05, -26.85) * mm});
            skLineSegment(sketch, "E968", {"start": v(15.05, -26.85) * mm, "end": v(15.05, -26.86) * mm});
            skLineSegment(sketch, "E969", {"start": v(15.05, -26.86) * mm, "end": v(15.06, -26.87) * mm});
            skLineSegment(sketch, "E970", {"start": v(15.06, -26.87) * mm, "end": v(15.07, -26.88) * mm});
            skLineSegment(sketch, "E971", {"start": v(15.07, -26.88) * mm, "end": v(15.08, -26.9) * mm});
            skLineSegment(sketch, "E972", {"start": v(15.08, -26.9) * mm, "end": v(15.1, -26.92) * mm});
            skLineSegment(sketch, "E973", {"start": v(15.1, -26.92) * mm, "end": v(15.1, -26.95) * mm});
            skLineSegment(sketch, "E974", {"start": v(15.1, -26.95) * mm, "end": v(15.13, -26.97) * mm});
            skLineSegment(sketch, "E975", {"start": v(15.13, -26.97) * mm, "end": v(15.15, -27) * mm});
            skLineSegment(sketch, "E976", {"start": v(15.15, -27) * mm, "end": v(15.17, -27.04) * mm});
            skLineSegment(sketch, "E977", {"start": v(15.17, -27.04) * mm, "end": v(15.2, -27.07) * mm});
            skLineSegment(sketch, "E978", {"start": v(15.2, -27.07) * mm, "end": v(15.23, -27.11) * mm});
            skLineSegment(sketch, "E979", {"start": v(15.23, -27.11) * mm, "end": v(15.26, -27.16) * mm});
            skLineSegment(sketch, "E980", {"start": v(15.26, -27.16) * mm, "end": v(15.3, -27.2) * mm});
            skLineSegment(sketch, "E981", {"start": v(15.3, -27.2) * mm, "end": v(15.34, -27.25) * mm});
            skLineSegment(sketch, "E982", {"start": v(15.34, -27.25) * mm, "end": v(15.38, -27.3) * mm});
            skLineSegment(sketch, "E983", {"start": v(15.38, -27.3) * mm, "end": v(15.43, -27.36) * mm});
            skLineSegment(sketch, "E984", {"start": v(15.43, -27.36) * mm, "end": v(15.48, -27.41) * mm});
            skLineSegment(sketch, "E985", {"start": v(15.48, -27.41) * mm, "end": v(15.53, -27.47) * mm});
            skLineSegment(sketch, "E986", {"start": v(15.53, -27.47) * mm, "end": v(15.59, -27.53) * mm});
            skLineSegment(sketch, "E987", {"start": v(15.59, -27.53) * mm, "end": v(15.65, -27.6) * mm});
            skLineSegment(sketch, "E988", {"start": v(15.65, -27.6) * mm, "end": v(15.71, -27.66) * mm});
            skLineSegment(sketch, "E989", {"start": v(15.71, -27.66) * mm, "end": v(15.78, -27.73) * mm});
            skLineSegment(sketch, "E990", {"start": v(15.78, -27.73) * mm, "end": v(15.85, -27.8) * mm});
            skLineSegment(sketch, "E991", {"start": v(15.85, -27.8) * mm, "end": v(15.92, -27.87) * mm});
            skLineSegment(sketch, "E992", {"start": v(15.92, -27.87) * mm, "end": v(16, -27.95) * mm});
            skLineSegment(sketch, "E993", {"start": v(16, -27.95) * mm, "end": v(16.09, -28.02) * mm});
            skLineSegment(sketch, "E994", {"start": v(16.09, -28.02) * mm, "end": v(16.17, -28.1) * mm});
            skLineSegment(sketch, "E995", {"start": v(16.17, -28.1) * mm, "end": v(16.26, -28.18) * mm});
            skLineSegment(sketch, "E996", {"start": v(16.26, -28.18) * mm, "end": v(16.36, -28.26) * mm});
            skLineSegment(sketch, "E997", {"start": v(16.36, -28.26) * mm, "end": v(16.46, -28.35) * mm});
            skLineSegment(sketch, "E998", {"start": v(16.46, -28.35) * mm, "end": v(16.56, -28.43) * mm});
            skLineSegment(sketch, "E999", {"start": v(16.56, -28.43) * mm, "end": v(16.67, -28.52) * mm});
            skLineSegment(sketch, "E1000", {"start": v(16.67, -28.52) * mm, "end": v(16.78, -28.6) * mm});
            skLineSegment(sketch, "E1001", {"start": v(16.78, -28.6) * mm, "end": v(16.9, -28.7) * mm});
            skLineSegment(sketch, "E1002", {"start": v(16.9, -28.7) * mm, "end": v(17.01, -28.78) * mm});
            skLineSegment(sketch, "E1003", {"start": v(17.01, -28.78) * mm, "end": v(17.14, -28.87) * mm});
            skLineSegment(sketch, "E1004", {"start": v(17.14, -28.87) * mm, "end": v(17.27, -28.97) * mm});
            skLineSegment(sketch, "E1005", {"start": v(17.27, -28.97) * mm, "end": v(17.4, -29.06) * mm});
            skLineSegment(sketch, "E1006", {"start": v(17.4, -29.06) * mm, "end": v(17.54, -29.15) * mm});
            skLineSegment(sketch, "E1007", {"start": v(17.54, -29.15) * mm, "end": v(17.68, -29.25) * mm});
            skLineSegment(sketch, "E1008", {"start": v(17.68, -29.25) * mm, "end": v(17.83, -29.34) * mm});
            skLineSegment(sketch, "E1009", {"start": v(17.83, -29.34) * mm, "end": v(17.98, -29.44) * mm});
            skLineSegment(sketch, "E1010", {"start": v(17.98, -29.44) * mm, "end": v(18.14, -29.53) * mm});
            skLineSegment(sketch, "E1011", {"start": v(18.14, -29.53) * mm, "end": v(18.3, -29.63) * mm});
            skLineSegment(sketch, "E1012", {"start": v(18.3, -29.63) * mm, "end": v(18.43, -29.67) * mm});
            skLineSegment(sketch, "E1013", {"start": v(18.43, -29.67) * mm, "end": v(19.67, -28.87) * mm});
            skLineSegment(sketch, "E1014", {"start": v(19.67, -28.87) * mm, "end": v(19.68, -28.73) * mm});
            skLineSegment(sketch, "E1015", {"start": v(19.68, -28.73) * mm, "end": v(19.66, -28.54) * mm});
            skLineSegment(sketch, "E1016", {"start": v(19.66, -28.54) * mm, "end": v(19.64, -28.36) * mm});
            skLineSegment(sketch, "E1017", {"start": v(19.64, -28.36) * mm, "end": v(19.61, -28.18) * mm});
            skLineSegment(sketch, "E1018", {"start": v(19.61, -28.18) * mm, "end": v(19.58, -28) * mm});
            skLineSegment(sketch, "E1019", {"start": v(19.58, -28) * mm, "end": v(19.56, -27.84) * mm});
            skLineSegment(sketch, "E1020", {"start": v(19.56, -27.84) * mm, "end": v(19.53, -27.67) * mm});
            skLineSegment(sketch, "E1021", {"start": v(19.53, -27.67) * mm, "end": v(19.5, -27.52) * mm});
            skLineSegment(sketch, "E1022", {"start": v(19.5, -27.52) * mm, "end": v(19.46, -27.36) * mm});
            skLineSegment(sketch, "E1023", {"start": v(19.46, -27.36) * mm, "end": v(19.43, -27.2) * mm});
            skLineSegment(sketch, "E1024", {"start": v(19.43, -27.2) * mm, "end": v(19.4, -27.06) * mm});
            skLineSegment(sketch, "E1025", {"start": v(19.4, -27.06) * mm, "end": v(19.36, -26.92) * mm});
            skLineSegment(sketch, "E1026", {"start": v(19.36, -26.92) * mm, "end": v(19.33, -26.78) * mm});
            skLineSegment(sketch, "E1027", {"start": v(19.33, -26.78) * mm, "end": v(19.3, -26.65) * mm});
            skLineSegment(sketch, "E1028", {"start": v(19.3, -26.65) * mm, "end": v(19.26, -26.52) * mm});
            skLineSegment(sketch, "E1029", {"start": v(19.26, -26.52) * mm, "end": v(19.22, -26.4) * mm});
            skLineSegment(sketch, "E1030", {"start": v(19.22, -26.4) * mm, "end": v(19.19, -26.28) * mm});
            skLineSegment(sketch, "E1031", {"start": v(19.19, -26.28) * mm, "end": v(19.15, -26.16) * mm});
            skLineSegment(sketch, "E1032", {"start": v(19.15, -26.16) * mm, "end": v(19.11, -26.05) * mm});
            skLineSegment(sketch, "E1033", {"start": v(19.11, -26.05) * mm, "end": v(19.08, -25.95) * mm});
            skLineSegment(sketch, "E1034", {"start": v(19.08, -25.95) * mm, "end": v(19.04, -25.84) * mm});
            skLineSegment(sketch, "E1035", {"start": v(19.04, -25.84) * mm, "end": v(19, -25.75) * mm});
            skLineSegment(sketch, "E1036", {"start": v(19, -25.75) * mm, "end": v(18.97, -25.65) * mm});
            skLineSegment(sketch, "E1037", {"start": v(18.97, -25.65) * mm, "end": v(18.93, -25.56) * mm});
            skLineSegment(sketch, "E1038", {"start": v(18.93, -25.56) * mm, "end": v(18.9, -25.48) * mm});
            skLineSegment(sketch, "E1039", {"start": v(18.9, -25.48) * mm, "end": v(18.87, -25.4) * mm});
            skLineSegment(sketch, "E1040", {"start": v(18.87, -25.4) * mm, "end": v(18.83, -25.32) * mm});
            skLineSegment(sketch, "E1041", {"start": v(18.83, -25.32) * mm, "end": v(18.8, -25.25) * mm});
            skLineSegment(sketch, "E1042", {"start": v(18.8, -25.25) * mm, "end": v(18.77, -25.18) * mm});
            skLineSegment(sketch, "E1043", {"start": v(18.77, -25.18) * mm, "end": v(18.74, -25.12) * mm});
            skLineSegment(sketch, "E1044", {"start": v(18.74, -25.12) * mm, "end": v(18.7, -25.06) * mm});
            skLineSegment(sketch, "E1045", {"start": v(18.7, -25.06) * mm, "end": v(18.68, -25) * mm});
            skLineSegment(sketch, "E1046", {"start": v(18.68, -25) * mm, "end": v(18.65, -24.95) * mm});
            skLineSegment(sketch, "E1047", {"start": v(18.65, -24.95) * mm, "end": v(18.63, -24.9) * mm});
            skLineSegment(sketch, "E1048", {"start": v(18.63, -24.9) * mm, "end": v(18.6, -24.86) * mm});
            skLineSegment(sketch, "E1049", {"start": v(18.6, -24.86) * mm, "end": v(18.58, -24.82) * mm});
            skLineSegment(sketch, "E1050", {"start": v(18.58, -24.82) * mm, "end": v(18.56, -24.78) * mm});
            skLineSegment(sketch, "E1051", {"start": v(18.56, -24.78) * mm, "end": v(18.54, -24.75) * mm});
            skLineSegment(sketch, "E1052", {"start": v(18.54, -24.75) * mm, "end": v(18.52, -24.72) * mm});
            skLineSegment(sketch, "E1053", {"start": v(18.52, -24.72) * mm, "end": v(18.5, -24.7) * mm});
            skLineSegment(sketch, "E1054", {"start": v(18.5, -24.7) * mm, "end": v(18.5, -24.68) * mm});
            skLineSegment(sketch, "E1055", {"start": v(18.5, -24.68) * mm, "end": v(18.48, -24.66) * mm});
            skLineSegment(sketch, "E1056", {"start": v(18.48, -24.66) * mm, "end": v(18.47, -24.65) * mm});
            skLineSegment(sketch, "E1057", {"start": v(18.47, -24.65) * mm, "end": v(18.47, -24.64) * mm});
            skLineSegment(sketch, "E1058", {"start": v(18.47, -24.64) * mm, "end": v(18.46, -24.63) * mm});
            skLineSegment(sketch, "E1059", {"start": v(18.46, -24.63) * mm, "end": v(18.14, -24.2) * mm});
            skLineSegment(sketch, "E1060", {"start": v(18.14, -24.2) * mm, "end": v(19.94, -22.73) * mm});
            skLineSegment(sketch, "E1061", {"start": v(19.94, -22.73) * mm, "end": v(20.3, -23.14) * mm});
            skLineSegment(sketch, "E1062", {"start": v(20.3, -23.14) * mm, "end": v(20.3, -23.14) * mm});
            skLineSegment(sketch, "E1063", {"start": v(20.3, -23.14) * mm, "end": v(20.31, -23.15) * mm});
            skLineSegment(sketch, "E1064", {"start": v(20.31, -23.15) * mm, "end": v(20.33, -23.16) * mm});
            skLineSegment(sketch, "E1065", {"start": v(20.33, -23.16) * mm, "end": v(20.34, -23.18) * mm});
            skLineSegment(sketch, "E1066", {"start": v(20.34, -23.18) * mm, "end": v(20.36, -23.2) * mm});
            skLineSegment(sketch, "E1067", {"start": v(20.36, -23.2) * mm, "end": v(20.38, -23.22) * mm});
            skLineSegment(sketch, "E1068", {"start": v(20.38, -23.22) * mm, "end": v(20.4, -23.24) * mm});
            skLineSegment(sketch, "E1069", {"start": v(20.4, -23.24) * mm, "end": v(20.43, -23.26) * mm});
            skLineSegment(sketch, "E1070", {"start": v(20.43, -23.26) * mm, "end": v(20.46, -23.3) * mm});
            skLineSegment(sketch, "E1071", {"start": v(20.46, -23.3) * mm, "end": v(20.5, -23.32) * mm});
            skLineSegment(sketch, "E1072", {"start": v(20.5, -23.32) * mm, "end": v(20.53, -23.36) * mm});
            skLineSegment(sketch, "E1073", {"start": v(20.53, -23.36) * mm, "end": v(20.58, -23.39) * mm});
            skLineSegment(sketch, "E1074", {"start": v(20.58, -23.39) * mm, "end": v(20.62, -23.43) * mm});
            skLineSegment(sketch, "E1075", {"start": v(20.62, -23.43) * mm, "end": v(20.67, -23.47) * mm});
            skLineSegment(sketch, "E1076", {"start": v(20.67, -23.47) * mm, "end": v(20.72, -23.5) * mm});
            skLineSegment(sketch, "E1077", {"start": v(20.72, -23.5) * mm, "end": v(20.78, -23.55) * mm});
            skLineSegment(sketch, "E1078", {"start": v(20.78, -23.55) * mm, "end": v(20.84, -23.6) * mm});
            skLineSegment(sketch, "E1079", {"start": v(20.84, -23.6) * mm, "end": v(20.9, -23.64) * mm});
            skLineSegment(sketch, "E1080", {"start": v(20.9, -23.64) * mm, "end": v(20.97, -23.69) * mm});
            skLineSegment(sketch, "E1081", {"start": v(20.97, -23.69) * mm, "end": v(21.04, -23.74) * mm});
            skLineSegment(sketch, "E1082", {"start": v(21.04, -23.74) * mm, "end": v(21.12, -23.8) * mm});
            skLineSegment(sketch, "E1083", {"start": v(21.12, -23.8) * mm, "end": v(21.2, -23.84) * mm});
            skLineSegment(sketch, "E1084", {"start": v(21.2, -23.84) * mm, "end": v(21.28, -23.9) * mm});
            skLineSegment(sketch, "E1085", {"start": v(21.28, -23.9) * mm, "end": v(21.37, -23.95) * mm});
            skLineSegment(sketch, "E1086", {"start": v(21.37, -23.95) * mm, "end": v(21.46, -24) * mm});
            skLineSegment(sketch, "E1087", {"start": v(21.46, -24) * mm, "end": v(21.56, -24.07) * mm});
            skLineSegment(sketch, "E1088", {"start": v(21.56, -24.07) * mm, "end": v(21.66, -24.13) * mm});
            skLineSegment(sketch, "E1089", {"start": v(21.66, -24.13) * mm, "end": v(21.77, -24.18) * mm});
            skLineSegment(sketch, "E1090", {"start": v(21.77, -24.18) * mm, "end": v(21.88, -24.24) * mm});
            skLineSegment(sketch, "E1091", {"start": v(21.88, -24.24) * mm, "end": v(21.99, -24.3) * mm});
            skLineSegment(sketch, "E1092", {"start": v(21.99, -24.3) * mm, "end": v(22.1, -24.37) * mm});
            skLineSegment(sketch, "E1093", {"start": v(22.1, -24.37) * mm, "end": v(22.23, -24.43) * mm});
            skLineSegment(sketch, "E1094", {"start": v(22.23, -24.43) * mm, "end": v(22.36, -24.5) * mm});
            skLineSegment(sketch, "E1095", {"start": v(22.36, -24.5) * mm, "end": v(22.5, -24.55) * mm});
            skLineSegment(sketch, "E1096", {"start": v(22.5, -24.55) * mm, "end": v(22.63, -24.62) * mm});
            skLineSegment(sketch, "E1097", {"start": v(22.63, -24.62) * mm, "end": v(22.77, -24.68) * mm});
            skLineSegment(sketch, "E1098", {"start": v(22.77, -24.68) * mm, "end": v(22.91, -24.74) * mm});
            skLineSegment(sketch, "E1099", {"start": v(22.91, -24.74) * mm, "end": v(23.06, -24.8) * mm});
            skLineSegment(sketch, "E1100", {"start": v(23.06, -24.8) * mm, "end": v(23.22, -24.87) * mm});
            skLineSegment(sketch, "E1101", {"start": v(23.22, -24.87) * mm, "end": v(23.38, -24.93) * mm});
            skLineSegment(sketch, "E1102", {"start": v(23.38, -24.93) * mm, "end": v(23.54, -25) * mm});
            skLineSegment(sketch, "E1103", {"start": v(23.54, -25) * mm, "end": v(23.7, -25.05) * mm});
            skLineSegment(sketch, "E1104", {"start": v(23.7, -25.05) * mm, "end": v(23.88, -25.11) * mm});
            skLineSegment(sketch, "E1105", {"start": v(23.88, -25.11) * mm, "end": v(24.06, -25.17) * mm});
            skLineSegment(sketch, "E1106", {"start": v(24.06, -25.17) * mm, "end": v(24.2, -25.2) * mm});
            skLineSegment(sketch, "E1107", {"start": v(24.2, -25.2) * mm, "end": v(25.24, -24.15) * mm});
            skLineSegment(sketch, "E1108", {"start": v(25.24, -24.15) * mm, "end": v(25.22, -24) * mm});
            skLineSegment(sketch, "E1109", {"start": v(25.22, -24) * mm, "end": v(25.16, -23.83) * mm});
            skLineSegment(sketch, "E1110", {"start": v(25.16, -23.83) * mm, "end": v(25.1, -23.66) * mm});
            skLineSegment(sketch, "E1111", {"start": v(25.1, -23.66) * mm, "end": v(25.04, -23.49) * mm});
            skLineSegment(sketch, "E1112", {"start": v(25.04, -23.49) * mm, "end": v(24.98, -23.32) * mm});
            skLineSegment(sketch, "E1113", {"start": v(24.98, -23.32) * mm, "end": v(24.92, -23.16) * mm});
            skLineSegment(sketch, "E1114", {"start": v(24.92, -23.16) * mm, "end": v(24.85, -23.01) * mm});
            skLineSegment(sketch, "E1115", {"start": v(24.85, -23.01) * mm, "end": v(24.79, -22.86) * mm});
            skLineSegment(sketch, "E1116", {"start": v(24.79, -22.86) * mm, "end": v(24.73, -22.72) * mm});
            skLineSegment(sketch, "E1117", {"start": v(24.73, -22.72) * mm, "end": v(24.66, -22.58) * mm});
            skLineSegment(sketch, "E1118", {"start": v(24.66, -22.58) * mm, "end": v(24.6, -22.44) * mm});
            skLineSegment(sketch, "E1119", {"start": v(24.6, -22.44) * mm, "end": v(24.54, -22.3) * mm});
            skLineSegment(sketch, "E1120", {"start": v(24.54, -22.3) * mm, "end": v(24.48, -22.18) * mm});
            skLineSegment(sketch, "E1121", {"start": v(24.48, -22.18) * mm, "end": v(24.41, -22.06) * mm});
            skLineSegment(sketch, "E1122", {"start": v(24.41, -22.06) * mm, "end": v(24.35, -21.94) * mm});
            skLineSegment(sketch, "E1123", {"start": v(24.35, -21.94) * mm, "end": v(24.3, -21.83) * mm});
            skLineSegment(sketch, "E1124", {"start": v(24.3, -21.83) * mm, "end": v(24.23, -21.72) * mm});
            skLineSegment(sketch, "E1125", {"start": v(24.23, -21.72) * mm, "end": v(24.17, -21.61) * mm});
            skLineSegment(sketch, "E1126", {"start": v(24.17, -21.61) * mm, "end": v(24.11, -21.51) * mm});
            skLineSegment(sketch, "E1127", {"start": v(24.11, -21.51) * mm, "end": v(24.05, -21.41) * mm});
            skLineSegment(sketch, "E1128", {"start": v(24.05, -21.41) * mm, "end": v(24, -21.32) * mm});
            skLineSegment(sketch, "E1129", {"start": v(24, -21.32) * mm, "end": v(23.94, -21.23) * mm});
            skLineSegment(sketch, "E1130", {"start": v(23.94, -21.23) * mm, "end": v(23.89, -21.15) * mm});
            skLineSegment(sketch, "E1131", {"start": v(23.89, -21.15) * mm, "end": v(23.83, -21.07) * mm});
            skLineSegment(sketch, "E1132", {"start": v(23.83, -21.07) * mm, "end": v(23.78, -21) * mm});
            skLineSegment(sketch, "E1133", {"start": v(23.78, -21) * mm, "end": v(23.73, -20.92) * mm});
            skLineSegment(sketch, "E1134", {"start": v(23.73, -20.92) * mm, "end": v(23.69, -20.85) * mm});
            skLineSegment(sketch, "E1135", {"start": v(23.69, -20.85) * mm, "end": v(23.64, -20.79) * mm});
            skLineSegment(sketch, "E1136", {"start": v(23.64, -20.79) * mm, "end": v(23.6, -20.73) * mm});
            skLineSegment(sketch, "E1137", {"start": v(23.6, -20.73) * mm, "end": v(23.55, -20.67) * mm});
            skLineSegment(sketch, "E1138", {"start": v(23.55, -20.67) * mm, "end": v(23.5, -20.62) * mm});
            skLineSegment(sketch, "E1139", {"start": v(23.5, -20.62) * mm, "end": v(23.47, -20.57) * mm});
            skLineSegment(sketch, "E1140", {"start": v(23.47, -20.57) * mm, "end": v(23.43, -20.53) * mm});
            skLineSegment(sketch, "E1141", {"start": v(23.43, -20.53) * mm, "end": v(23.4, -20.49) * mm});
            skLineSegment(sketch, "E1142", {"start": v(23.4, -20.49) * mm, "end": v(23.37, -20.45) * mm});
            skLineSegment(sketch, "E1143", {"start": v(23.37, -20.45) * mm, "end": v(23.33, -20.41) * mm});
            skLineSegment(sketch, "E1144", {"start": v(23.33, -20.41) * mm, "end": v(23.3, -20.38) * mm});
            skLineSegment(sketch, "E1145", {"start": v(23.3, -20.38) * mm, "end": v(23.28, -20.36) * mm});
            skLineSegment(sketch, "E1146", {"start": v(23.28, -20.36) * mm, "end": v(23.26, -20.33) * mm});
            skLineSegment(sketch, "E1147", {"start": v(23.26, -20.33) * mm, "end": v(23.24, -20.31) * mm});
            skLineSegment(sketch, "E1148", {"start": v(23.24, -20.31) * mm, "end": v(23.22, -20.3) * mm});
            skLineSegment(sketch, "E1149", {"start": v(23.22, -20.3) * mm, "end": v(23.2, -20.28) * mm});
            skLineSegment(sketch, "E1150", {"start": v(23.2, -20.28) * mm, "end": v(23.2, -20.27) * mm});
            skLineSegment(sketch, "E1151", {"start": v(23.2, -20.27) * mm, "end": v(23.18, -20.26) * mm});
            skLineSegment(sketch, "E1152", {"start": v(23.18, -20.26) * mm, "end": v(23.18, -20.25) * mm});
            skLineSegment(sketch, "E1153", {"start": v(23.18, -20.25) * mm, "end": v(22.77, -19.9) * mm});
            skLineSegment(sketch, "E1154", {"start": v(22.77, -19.9) * mm, "end": v(24.23, -18.09) * mm});
            skLineSegment(sketch, "E1155", {"start": v(24.23, -18.09) * mm, "end": v(24.67, -18.4) * mm});
            skLineSegment(sketch, "E1156", {"start": v(24.67, -18.4) * mm, "end": v(24.67, -18.41) * mm});
            skLineSegment(sketch, "E1157", {"start": v(24.67, -18.41) * mm, "end": v(24.68, -18.42) * mm});
            skLineSegment(sketch, "E1158", {"start": v(24.68, -18.42) * mm, "end": v(24.7, -18.43) * mm});
            skLineSegment(sketch, "E1159", {"start": v(24.7, -18.43) * mm, "end": v(24.72, -18.44) * mm});
            skLineSegment(sketch, "E1160", {"start": v(24.72, -18.44) * mm, "end": v(24.74, -18.46) * mm});
            skLineSegment(sketch, "E1161", {"start": v(24.74, -18.46) * mm, "end": v(24.76, -18.47) * mm});
            skLineSegment(sketch, "E1162", {"start": v(24.76, -18.47) * mm, "end": v(24.79, -18.49) * mm});
            skLineSegment(sketch, "E1163", {"start": v(24.79, -18.49) * mm, "end": v(24.82, -18.5) * mm});
            skLineSegment(sketch, "E1164", {"start": v(24.82, -18.5) * mm, "end": v(24.86, -18.53) * mm});
            skLineSegment(sketch, "E1165", {"start": v(24.86, -18.53) * mm, "end": v(24.9, -18.55) * mm});
            skLineSegment(sketch, "E1166", {"start": v(24.9, -18.55) * mm, "end": v(24.94, -18.58) * mm});
            skLineSegment(sketch, "E1167", {"start": v(24.94, -18.58) * mm, "end": v(24.99, -18.6) * mm});
            skLineSegment(sketch, "E1168", {"start": v(24.99, -18.6) * mm, "end": v(25.04, -18.63) * mm});
            skLineSegment(sketch, "E1169", {"start": v(25.04, -18.63) * mm, "end": v(25.1, -18.66) * mm});
            skLineSegment(sketch, "E1170", {"start": v(25.1, -18.66) * mm, "end": v(25.16, -18.69) * mm});
            skLineSegment(sketch, "E1171", {"start": v(25.16, -18.69) * mm, "end": v(25.22, -18.72) * mm});
            skLineSegment(sketch, "E1172", {"start": v(25.22, -18.72) * mm, "end": v(25.29, -18.75) * mm});
            skLineSegment(sketch, "E1173", {"start": v(25.29, -18.75) * mm, "end": v(25.36, -18.78) * mm});
            skLineSegment(sketch, "E1174", {"start": v(25.36, -18.78) * mm, "end": v(25.44, -18.81) * mm});
            skLineSegment(sketch, "E1175", {"start": v(25.44, -18.81) * mm, "end": v(25.52, -18.85) * mm});
            skLineSegment(sketch, "E1176", {"start": v(25.52, -18.85) * mm, "end": v(25.6, -18.88) * mm});
            skLineSegment(sketch, "E1177", {"start": v(25.6, -18.88) * mm, "end": v(25.7, -18.92) * mm});
            skLineSegment(sketch, "E1178", {"start": v(25.7, -18.92) * mm, "end": v(25.79, -18.95) * mm});
            skLineSegment(sketch, "E1179", {"start": v(25.79, -18.95) * mm, "end": v(25.88, -18.99) * mm});
            skLineSegment(sketch, "E1180", {"start": v(25.88, -18.99) * mm, "end": v(25.99, -19.02) * mm});
            skLineSegment(sketch, "E1181", {"start": v(25.99, -19.02) * mm, "end": v(26.1, -19.06) * mm});
            skLineSegment(sketch, "E1182", {"start": v(26.1, -19.06) * mm, "end": v(26.2, -19.1) * mm});
            skLineSegment(sketch, "E1183", {"start": v(26.2, -19.1) * mm, "end": v(26.32, -19.13) * mm});
            skLineSegment(sketch, "E1184", {"start": v(26.32, -19.13) * mm, "end": v(26.44, -19.17) * mm});
            skLineSegment(sketch, "E1185", {"start": v(26.44, -19.17) * mm, "end": v(26.56, -19.2) * mm});
            skLineSegment(sketch, "E1186", {"start": v(26.56, -19.2) * mm, "end": v(26.7, -19.24) * mm});
            skLineSegment(sketch, "E1187", {"start": v(26.7, -19.24) * mm, "end": v(26.82, -19.27) * mm});
            skLineSegment(sketch, "E1188", {"start": v(26.82, -19.27) * mm, "end": v(26.96, -19.3) * mm});
            skLineSegment(sketch, "E1189", {"start": v(26.96, -19.3) * mm, "end": v(27.1, -19.34) * mm});
            skLineSegment(sketch, "E1190", {"start": v(27.1, -19.34) * mm, "end": v(27.25, -19.37) * mm});
            skLineSegment(sketch, "E1191", {"start": v(27.25, -19.37) * mm, "end": v(27.4, -19.4) * mm});
            skLineSegment(sketch, "E1192", {"start": v(27.4, -19.4) * mm, "end": v(27.56, -19.44) * mm});
            skLineSegment(sketch, "E1193", {"start": v(27.56, -19.44) * mm, "end": v(27.72, -19.47) * mm});
            skLineSegment(sketch, "E1194", {"start": v(27.72, -19.47) * mm, "end": v(27.88, -19.5) * mm});
            skLineSegment(sketch, "E1195", {"start": v(27.88, -19.5) * mm, "end": v(28.05, -19.53) * mm});
            skLineSegment(sketch, "E1196", {"start": v(28.05, -19.53) * mm, "end": v(28.22, -19.55) * mm});
            skLineSegment(sketch, "E1197", {"start": v(28.22, -19.55) * mm, "end": v(28.4, -19.58) * mm});
            skLineSegment(sketch, "E1198", {"start": v(28.4, -19.58) * mm, "end": v(28.58, -19.6) * mm});
            skLineSegment(sketch, "E1199", {"start": v(28.58, -19.6) * mm, "end": v(28.77, -19.62) * mm});
            skLineSegment(sketch, "E1200", {"start": v(28.77, -19.62) * mm, "end": v(28.9, -19.61) * mm});
            skLineSegment(sketch, "E1201", {"start": v(28.9, -19.61) * mm, "end": v(29.71, -18.37) * mm});
            skLineSegment(sketch, "E1202", {"start": v(29.71, -18.37) * mm, "end": v(29.66, -18.24) * mm});
            skLineSegment(sketch, "E1203", {"start": v(29.66, -18.24) * mm, "end": v(29.57, -18.08) * mm});
            skLineSegment(sketch, "E1204", {"start": v(29.57, -18.08) * mm, "end": v(29.47, -17.92) * mm});
            skLineSegment(sketch, "E1205", {"start": v(29.47, -17.92) * mm, "end": v(29.38, -17.77) * mm});
            skLineSegment(sketch, "E1206", {"start": v(29.38, -17.77) * mm, "end": v(29.28, -17.62) * mm});
            skLineSegment(sketch, "E1207", {"start": v(29.28, -17.62) * mm, "end": v(29.19, -17.48) * mm});
            skLineSegment(sketch, "E1208", {"start": v(29.19, -17.48) * mm, "end": v(29.1, -17.34) * mm});
            skLineSegment(sketch, "E1209", {"start": v(29.1, -17.34) * mm, "end": v(29, -17.2) * mm});
            skLineSegment(sketch, "E1210", {"start": v(29, -17.2) * mm, "end": v(28.9, -17.08) * mm});
            skLineSegment(sketch, "E1211", {"start": v(28.9, -17.08) * mm, "end": v(28.82, -16.95) * mm});
            skLineSegment(sketch, "E1212", {"start": v(28.82, -16.95) * mm, "end": v(28.73, -16.83) * mm});
            skLineSegment(sketch, "E1213", {"start": v(28.73, -16.83) * mm, "end": v(28.64, -16.72) * mm});
            skLineSegment(sketch, "E1214", {"start": v(28.64, -16.72) * mm, "end": v(28.55, -16.6) * mm});
            skLineSegment(sketch, "E1215", {"start": v(28.55, -16.6) * mm, "end": v(28.47, -16.5) * mm});
            skLineSegment(sketch, "E1216", {"start": v(28.47, -16.5) * mm, "end": v(28.38, -16.4) * mm});
            skLineSegment(sketch, "E1217", {"start": v(28.38, -16.4) * mm, "end": v(28.3, -16.3) * mm});
            skLineSegment(sketch, "E1218", {"start": v(28.3, -16.3) * mm, "end": v(28.22, -16.2) * mm});
            skLineSegment(sketch, "E1219", {"start": v(28.22, -16.2) * mm, "end": v(28.14, -16.11) * mm});
            skLineSegment(sketch, "E1220", {"start": v(28.14, -16.11) * mm, "end": v(28.06, -16.03) * mm});
            skLineSegment(sketch, "E1221", {"start": v(28.06, -16.03) * mm, "end": v(27.98, -15.94) * mm});
            skLineSegment(sketch, "E1222", {"start": v(27.98, -15.94) * mm, "end": v(27.9, -15.87) * mm});
            skLineSegment(sketch, "E1223", {"start": v(27.9, -15.87) * mm, "end": v(27.83, -15.8) * mm});
            skLineSegment(sketch, "E1224", {"start": v(27.83, -15.8) * mm, "end": v(27.76, -15.72) * mm});
            skLineSegment(sketch, "E1225", {"start": v(27.76, -15.72) * mm, "end": v(27.7, -15.65) * mm});
            skLineSegment(sketch, "E1226", {"start": v(27.7, -15.65) * mm, "end": v(27.63, -15.59) * mm});
            skLineSegment(sketch, "E1227", {"start": v(27.63, -15.59) * mm, "end": v(27.56, -15.53) * mm});
            skLineSegment(sketch, "E1228", {"start": v(27.56, -15.53) * mm, "end": v(27.5, -15.47) * mm});
            skLineSegment(sketch, "E1229", {"start": v(27.5, -15.47) * mm, "end": v(27.44, -15.42) * mm});
            skLineSegment(sketch, "E1230", {"start": v(27.44, -15.42) * mm, "end": v(27.39, -15.37) * mm});
            skLineSegment(sketch, "E1231", {"start": v(27.39, -15.37) * mm, "end": v(27.33, -15.33) * mm});
            skLineSegment(sketch, "E1232", {"start": v(27.33, -15.33) * mm, "end": v(27.28, -15.28) * mm});
            skLineSegment(sketch, "E1233", {"start": v(27.28, -15.28) * mm, "end": v(27.23, -15.24) * mm});
            skLineSegment(sketch, "E1234", {"start": v(27.23, -15.24) * mm, "end": v(27.19, -15.2) * mm});
            skLineSegment(sketch, "E1235", {"start": v(27.19, -15.2) * mm, "end": v(27.15, -15.17) * mm});
            skLineSegment(sketch, "E1236", {"start": v(27.15, -15.17) * mm, "end": v(27.1, -15.14) * mm});
            skLineSegment(sketch, "E1237", {"start": v(27.1, -15.14) * mm, "end": v(27.07, -15.12) * mm});
            skLineSegment(sketch, "E1238", {"start": v(27.07, -15.12) * mm, "end": v(27.04, -15.1) * mm});
            skLineSegment(sketch, "E1239", {"start": v(27.04, -15.1) * mm, "end": v(27, -15.07) * mm});
            skLineSegment(sketch, "E1240", {"start": v(27, -15.07) * mm, "end": v(26.98, -15.05) * mm});
            skLineSegment(sketch, "E1241", {"start": v(26.98, -15.05) * mm, "end": v(26.95, -15.04) * mm});
            skLineSegment(sketch, "E1242", {"start": v(26.95, -15.04) * mm, "end": v(26.93, -15.02) * mm});
            skLineSegment(sketch, "E1243", {"start": v(26.93, -15.02) * mm, "end": v(26.91, -15.01) * mm});
            skLineSegment(sketch, "E1244", {"start": v(26.91, -15.01) * mm, "end": v(26.9, -15) * mm});
            skLineSegment(sketch, "E1245", {"start": v(26.9, -15) * mm, "end": v(26.89, -15) * mm});
            skLineSegment(sketch, "E1246", {"start": v(26.89, -15) * mm, "end": v(26.88, -15) * mm});
            skLineSegment(sketch, "E1247", {"start": v(26.88, -15) * mm, "end": v(26.41, -14.73) * mm});
            skLineSegment(sketch, "E1248", {"start": v(26.41, -14.73) * mm, "end": v(27.46, -12.65) * mm});
            skLineSegment(sketch, "E1249", {"start": v(27.46, -12.65) * mm, "end": v(27.96, -12.88) * mm});
            skLineSegment(sketch, "E1250", {"start": v(27.96, -12.88) * mm, "end": v(27.96, -12.88) * mm});
            skLineSegment(sketch, "E1251", {"start": v(27.96, -12.88) * mm, "end": v(27.97, -12.89) * mm});
            skLineSegment(sketch, "E1252", {"start": v(27.97, -12.89) * mm, "end": v(28, -12.9) * mm});
            skLineSegment(sketch, "E1253", {"start": v(28, -12.9) * mm, "end": v(28, -12.9) * mm});
            skLineSegment(sketch, "E1254", {"start": v(28, -12.9) * mm, "end": v(28.03, -12.9) * mm});
            skLineSegment(sketch, "E1255", {"start": v(28.03, -12.9) * mm, "end": v(28.06, -12.92) * mm});
            skLineSegment(sketch, "E1256", {"start": v(28.06, -12.92) * mm, "end": v(28.1, -12.93) * mm});
            skLineSegment(sketch, "E1257", {"start": v(28.1, -12.93) * mm, "end": v(28.13, -12.94) * mm});
            skLineSegment(sketch, "E1258", {"start": v(28.13, -12.94) * mm, "end": v(28.17, -12.96) * mm});
            skLineSegment(sketch, "E1259", {"start": v(28.17, -12.96) * mm, "end": v(28.21, -12.97) * mm});
            skLineSegment(sketch, "E1260", {"start": v(28.21, -12.97) * mm, "end": v(28.26, -12.98) * mm});
            skLineSegment(sketch, "E1261", {"start": v(28.26, -12.98) * mm, "end": v(28.31, -13) * mm});
            skLineSegment(sketch, "E1262", {"start": v(28.31, -13) * mm, "end": v(28.37, -13.01) * mm});
            skLineSegment(sketch, "E1263", {"start": v(28.37, -13.01) * mm, "end": v(28.43, -13.03) * mm});
            skLineSegment(sketch, "E1264", {"start": v(28.43, -13.03) * mm, "end": v(28.5, -13.05) * mm});
            skLineSegment(sketch, "E1265", {"start": v(28.5, -13.05) * mm, "end": v(28.56, -13.06) * mm});
            skLineSegment(sketch, "E1266", {"start": v(28.56, -13.06) * mm, "end": v(28.63, -13.08) * mm});
            skLineSegment(sketch, "E1267", {"start": v(28.63, -13.08) * mm, "end": v(28.71, -13.1) * mm});
            skLineSegment(sketch, "E1268", {"start": v(28.71, -13.1) * mm, "end": v(28.8, -13.11) * mm});
            skLineSegment(sketch, "E1269", {"start": v(28.8, -13.11) * mm, "end": v(28.88, -13.13) * mm});
            skLineSegment(sketch, "E1270", {"start": v(28.88, -13.13) * mm, "end": v(28.97, -13.14) * mm});
            skLineSegment(sketch, "E1271", {"start": v(28.97, -13.14) * mm, "end": v(29.06, -13.16) * mm});
            skLineSegment(sketch, "E1272", {"start": v(29.06, -13.16) * mm, "end": v(29.16, -13.18) * mm});
            skLineSegment(sketch, "E1273", {"start": v(29.16, -13.18) * mm, "end": v(29.27, -13.19) * mm});
            skLineSegment(sketch, "E1274", {"start": v(29.27, -13.19) * mm, "end": v(29.37, -13.2) * mm});
            skLineSegment(sketch, "E1275", {"start": v(29.37, -13.2) * mm, "end": v(29.49, -13.22) * mm});
            skLineSegment(sketch, "E1276", {"start": v(29.49, -13.22) * mm, "end": v(29.6, -13.23) * mm});
            skLineSegment(sketch, "E1277", {"start": v(29.6, -13.23) * mm, "end": v(29.72, -13.24) * mm});
            skLineSegment(sketch, "E1278", {"start": v(29.72, -13.24) * mm, "end": v(29.85, -13.25) * mm});
            skLineSegment(sketch, "E1279", {"start": v(29.85, -13.25) * mm, "end": v(29.97, -13.26) * mm});
            skLineSegment(sketch, "E1280", {"start": v(29.97, -13.26) * mm, "end": v(30.1, -13.27) * mm});
            skLineSegment(sketch, "E1281", {"start": v(30.1, -13.27) * mm, "end": v(30.25, -13.27) * mm});
            skLineSegment(sketch, "E1282", {"start": v(30.25, -13.27) * mm, "end": v(30.39, -13.28) * mm});
            skLineSegment(sketch, "E1283", {"start": v(30.39, -13.28) * mm, "end": v(30.53, -13.28) * mm});
            skLineSegment(sketch, "E1284", {"start": v(30.53, -13.28) * mm, "end": v(30.68, -13.29) * mm});
            skLineSegment(sketch, "E1285", {"start": v(30.68, -13.29) * mm, "end": v(30.84, -13.29) * mm});
            skLineSegment(sketch, "E1286", {"start": v(30.84, -13.29) * mm, "end": v(31, -13.28) * mm});
            skLineSegment(sketch, "E1287", {"start": v(31, -13.28) * mm, "end": v(31.16, -13.28) * mm});
            skLineSegment(sketch, "E1288", {"start": v(31.16, -13.28) * mm, "end": v(31.32, -13.27) * mm});
            skLineSegment(sketch, "E1289", {"start": v(31.32, -13.27) * mm, "end": v(31.5, -13.27) * mm});
            skLineSegment(sketch, "E1290", {"start": v(31.5, -13.27) * mm, "end": v(31.67, -13.26) * mm});
            skLineSegment(sketch, "E1291", {"start": v(31.67, -13.26) * mm, "end": v(31.85, -13.24) * mm});
            skLineSegment(sketch, "E1292", {"start": v(31.85, -13.24) * mm, "end": v(32.03, -13.23) * mm});
            skLineSegment(sketch, "E1293", {"start": v(32.03, -13.23) * mm, "end": v(32.22, -13.21) * mm});
            skLineSegment(sketch, "E1294", {"start": v(32.22, -13.21) * mm, "end": v(32.36, -13.17) * mm});
            skLineSegment(sketch, "E1295", {"start": v(32.36, -13.17) * mm, "end": v(32.88, -11.8) * mm});
            skLineSegment(sketch, "E1296", {"start": v(32.88, -11.8) * mm, "end": v(32.8, -11.67) * mm});
            skLineSegment(sketch, "E1297", {"start": v(32.8, -11.67) * mm, "end": v(32.68, -11.53) * mm});
            skLineSegment(sketch, "E1298", {"start": v(32.68, -11.53) * mm, "end": v(32.55, -11.4) * mm});
            skLineSegment(sketch, "E1299", {"start": v(32.55, -11.4) * mm, "end": v(32.43, -11.27) * mm});
            skLineSegment(sketch, "E1300", {"start": v(32.43, -11.27) * mm, "end": v(32.3, -11.15) * mm});
            skLineSegment(sketch, "E1301", {"start": v(32.3, -11.15) * mm, "end": v(32.18, -11.03) * mm});
            skLineSegment(sketch, "E1302", {"start": v(32.18, -11.03) * mm, "end": v(32.06, -10.91) * mm});
            skLineSegment(sketch, "E1303", {"start": v(32.06, -10.91) * mm, "end": v(31.95, -10.8) * mm});
            skLineSegment(sketch, "E1304", {"start": v(31.95, -10.8) * mm, "end": v(31.83, -10.7) * mm});
            skLineSegment(sketch, "E1305", {"start": v(31.83, -10.7) * mm, "end": v(31.71, -10.6) * mm});
            skLineSegment(sketch, "E1306", {"start": v(31.71, -10.6) * mm, "end": v(31.6, -10.5) * mm});
            skLineSegment(sketch, "E1307", {"start": v(31.6, -10.5) * mm, "end": v(31.49, -10.4) * mm});
            skLineSegment(sketch, "E1308", {"start": v(31.49, -10.4) * mm, "end": v(31.38, -10.3) * mm});
            skLineSegment(sketch, "E1309", {"start": v(31.38, -10.3) * mm, "end": v(31.27, -10.22) * mm});
            skLineSegment(sketch, "E1310", {"start": v(31.27, -10.22) * mm, "end": v(31.17, -10.14) * mm});
            skLineSegment(sketch, "E1311", {"start": v(31.17, -10.14) * mm, "end": v(31.07, -10.06) * mm});
            skLineSegment(sketch, "E1312", {"start": v(31.07, -10.06) * mm, "end": v(30.97, -9.98) * mm});
            skLineSegment(sketch, "E1313", {"start": v(30.97, -9.98) * mm, "end": v(30.87, -9.91) * mm});
            skLineSegment(sketch, "E1314", {"start": v(30.87, -9.91) * mm, "end": v(30.78, -9.84) * mm});
            skLineSegment(sketch, "E1315", {"start": v(30.78, -9.84) * mm, "end": v(30.68, -9.78) * mm});
            skLineSegment(sketch, "E1316", {"start": v(30.68, -9.78) * mm, "end": v(30.6, -9.72) * mm});
            skLineSegment(sketch, "E1317", {"start": v(30.6, -9.72) * mm, "end": v(30.5, -9.66) * mm});
            skLineSegment(sketch, "E1318", {"start": v(30.5, -9.66) * mm, "end": v(30.42, -9.6) * mm});
            skLineSegment(sketch, "E1319", {"start": v(30.42, -9.6) * mm, "end": v(30.34, -9.55) * mm});
            skLineSegment(sketch, "E1320", {"start": v(30.34, -9.55) * mm, "end": v(30.27, -9.5) * mm});
            skLineSegment(sketch, "E1321", {"start": v(30.27, -9.5) * mm, "end": v(30.2, -9.46) * mm});
            skLineSegment(sketch, "E1322", {"start": v(30.2, -9.46) * mm, "end": v(30.12, -9.42) * mm});
            skLineSegment(sketch, "E1323", {"start": v(30.12, -9.42) * mm, "end": v(30.05, -9.38) * mm});
            skLineSegment(sketch, "E1324", {"start": v(30.05, -9.38) * mm, "end": v(29.99, -9.34) * mm});
            skLineSegment(sketch, "E1325", {"start": v(29.99, -9.34) * mm, "end": v(29.92, -9.3) * mm});
            skLineSegment(sketch, "E1326", {"start": v(29.92, -9.3) * mm, "end": v(29.86, -9.28) * mm});
            skLineSegment(sketch, "E1327", {"start": v(29.86, -9.28) * mm, "end": v(29.8, -9.25) * mm});
            skLineSegment(sketch, "E1328", {"start": v(29.8, -9.25) * mm, "end": v(29.76, -9.22) * mm});
            skLineSegment(sketch, "E1329", {"start": v(29.76, -9.22) * mm, "end": v(29.7, -9.2) * mm});
            skLineSegment(sketch, "E1330", {"start": v(29.7, -9.2) * mm, "end": v(29.66, -9.18) * mm});
            skLineSegment(sketch, "E1331", {"start": v(29.66, -9.18) * mm, "end": v(29.62, -9.16) * mm});
            skLineSegment(sketch, "E1332", {"start": v(29.62, -9.16) * mm, "end": v(29.58, -9.14) * mm});
            skLineSegment(sketch, "E1333", {"start": v(29.58, -9.14) * mm, "end": v(29.55, -9.13) * mm});
            skLineSegment(sketch, "E1334", {"start": v(29.55, -9.13) * mm, "end": v(29.52, -9.11) * mm});
            skLineSegment(sketch, "E1335", {"start": v(29.52, -9.11) * mm, "end": v(29.49, -9.1) * mm});
            skLineSegment(sketch, "E1336", {"start": v(29.49, -9.1) * mm, "end": v(29.47, -9.1) * mm});
            skLineSegment(sketch, "E1337", {"start": v(29.47, -9.1) * mm, "end": v(29.45, -9.09) * mm});
            skLineSegment(sketch, "E1338", {"start": v(29.45, -9.09) * mm, "end": v(29.43, -9.08) * mm});
            skLineSegment(sketch, "E1339", {"start": v(29.43, -9.08) * mm, "end": v(29.42, -9.08) * mm});
            skLineSegment(sketch, "E1340", {"start": v(29.42, -9.08) * mm, "end": v(29.41, -9.07) * mm});
            skLineSegment(sketch, "E1341", {"start": v(29.41, -9.07) * mm, "end": v(28.9, -8.91) * mm});
            skLineSegment(sketch, "E1342", {"start": v(28.9, -8.91) * mm, "end": v(29.5, -6.67) * mm});
            skLineSegment(sketch, "E1343", {"start": v(29.5, -6.67) * mm, "end": v(30.02, -6.78) * mm});
            skLineSegment(sketch, "E1344", {"start": v(30.02, -6.78) * mm, "end": v(30.03, -6.79) * mm});
            skLineSegment(sketch, "E1345", {"start": v(30.03, -6.79) * mm, "end": v(30.04, -6.79) * mm});
            skLineSegment(sketch, "E1346", {"start": v(30.04, -6.79) * mm, "end": v(30.06, -6.8) * mm});
            skLineSegment(sketch, "E1347", {"start": v(30.06, -6.8) * mm, "end": v(30.08, -6.8) * mm});
            skLineSegment(sketch, "E1348", {"start": v(30.08, -6.8) * mm, "end": v(30.1, -6.8) * mm});
            skLineSegment(sketch, "E1349", {"start": v(30.1, -6.8) * mm, "end": v(30.13, -6.8) * mm});
            skLineSegment(sketch, "E1350", {"start": v(30.13, -6.8) * mm, "end": v(30.17, -6.8) * mm});
            skLineSegment(sketch, "E1351", {"start": v(30.17, -6.8) * mm, "end": v(30.2, -6.81) * mm});
            skLineSegment(sketch, "E1352", {"start": v(30.2, -6.81) * mm, "end": v(30.25, -6.82) * mm});
            skLineSegment(sketch, "E1353", {"start": v(30.25, -6.82) * mm, "end": v(30.3, -6.82) * mm});
            skLineSegment(sketch, "E1354", {"start": v(30.3, -6.82) * mm, "end": v(30.34, -6.82) * mm});
            skLineSegment(sketch, "E1355", {"start": v(30.34, -6.82) * mm, "end": v(30.4, -6.83) * mm});
            skLineSegment(sketch, "E1356", {"start": v(30.4, -6.83) * mm, "end": v(30.45, -6.83) * mm});
            skLineSegment(sketch, "E1357", {"start": v(30.45, -6.83) * mm, "end": v(30.52, -6.83) * mm});
            skLineSegment(sketch, "E1358", {"start": v(30.52, -6.83) * mm, "end": v(30.58, -6.84) * mm});
            skLineSegment(sketch, "E1359", {"start": v(30.58, -6.84) * mm, "end": v(30.65, -6.84) * mm});
            skLineSegment(sketch, "E1360", {"start": v(30.65, -6.84) * mm, "end": v(30.73, -6.84) * mm});
            skLineSegment(sketch, "E1361", {"start": v(30.73, -6.84) * mm, "end": v(30.8, -6.84) * mm});
            skLineSegment(sketch, "E1362", {"start": v(30.8, -6.84) * mm, "end": v(30.9, -6.84) * mm});
            skLineSegment(sketch, "E1363", {"start": v(30.9, -6.84) * mm, "end": v(30.98, -6.84) * mm});
            skLineSegment(sketch, "E1364", {"start": v(30.98, -6.84) * mm, "end": v(31.07, -6.83) * mm});
            skLineSegment(sketch, "E1365", {"start": v(31.07, -6.83) * mm, "end": v(31.17, -6.83) * mm});
            skLineSegment(sketch, "E1366", {"start": v(31.17, -6.83) * mm, "end": v(31.26, -6.82) * mm});
            skLineSegment(sketch, "E1367", {"start": v(31.26, -6.82) * mm, "end": v(31.37, -6.82) * mm});
            skLineSegment(sketch, "E1368", {"start": v(31.37, -6.82) * mm, "end": v(31.48, -6.8) * mm});
            skLineSegment(sketch, "E1369", {"start": v(31.48, -6.8) * mm, "end": v(31.59, -6.8) * mm});
            skLineSegment(sketch, "E1370", {"start": v(31.59, -6.8) * mm, "end": v(31.7, -6.79) * mm});
            skLineSegment(sketch, "E1371", {"start": v(31.7, -6.79) * mm, "end": v(31.82, -6.77) * mm});
            skLineSegment(sketch, "E1372", {"start": v(31.82, -6.77) * mm, "end": v(31.95, -6.76) * mm});
            skLineSegment(sketch, "E1373", {"start": v(31.95, -6.76) * mm, "end": v(32.08, -6.74) * mm});
            skLineSegment(sketch, "E1374", {"start": v(32.08, -6.74) * mm, "end": v(32.2, -6.72) * mm});
            skLineSegment(sketch, "E1375", {"start": v(32.2, -6.72) * mm, "end": v(32.34, -6.7) * mm});
            skLineSegment(sketch, "E1376", {"start": v(32.34, -6.7) * mm, "end": v(32.48, -6.67) * mm});
            skLineSegment(sketch, "E1377", {"start": v(32.48, -6.67) * mm, "end": v(32.63, -6.65) * mm});
            skLineSegment(sketch, "E1378", {"start": v(32.63, -6.65) * mm, "end": v(32.77, -6.62) * mm});
            skLineSegment(sketch, "E1379", {"start": v(32.77, -6.62) * mm, "end": v(32.93, -6.58) * mm});
            skLineSegment(sketch, "E1380", {"start": v(32.93, -6.58) * mm, "end": v(33.08, -6.55) * mm});
            skLineSegment(sketch, "E1381", {"start": v(33.08, -6.55) * mm, "end": v(33.24, -6.51) * mm});
            skLineSegment(sketch, "E1382", {"start": v(33.24, -6.51) * mm, "end": v(33.4, -6.47) * mm});
            skLineSegment(sketch, "E1383", {"start": v(33.4, -6.47) * mm, "end": v(33.56, -6.43) * mm});
            skLineSegment(sketch, "E1384", {"start": v(33.56, -6.43) * mm, "end": v(33.73, -6.38) * mm});
            skLineSegment(sketch, "E1385", {"start": v(33.73, -6.38) * mm, "end": v(33.9, -6.33) * mm});
            skLineSegment(sketch, "E1386", {"start": v(33.9, -6.33) * mm, "end": v(34.08, -6.28) * mm});
            skLineSegment(sketch, "E1387", {"start": v(34.08, -6.28) * mm, "end": v(34.26, -6.23) * mm});
            skLineSegment(sketch, "E1388", {"start": v(34.26, -6.23) * mm, "end": v(34.39, -6.16) * mm});
            skLineSegment(sketch, "E1389", {"start": v(34.39, -6.16) * mm, "end": v(34.62, -4.7) * mm});
            skLineSegment(sketch, "E1390", {"start": v(34.62, -4.7) * mm, "end": v(34.52, -4.6) * mm});
            skLineSegment(sketch, "E1391", {"start": v(34.52, -4.6) * mm, "end": v(34.36, -4.49) * mm});
            skLineSegment(sketch, "E1392", {"start": v(34.36, -4.49) * mm, "end": v(34.21, -4.38) * mm});
            skLineSegment(sketch, "E1393", {"start": v(34.21, -4.38) * mm, "end": v(34.06, -4.28) * mm});
            skLineSegment(sketch, "E1394", {"start": v(34.06, -4.28) * mm, "end": v(33.92, -4.19) * mm});
            skLineSegment(sketch, "E1395", {"start": v(33.92, -4.19) * mm, "end": v(33.77, -4.1) * mm});
            skLineSegment(sketch, "E1396", {"start": v(33.77, -4.1) * mm, "end": v(33.63, -4) * mm});
            skLineSegment(sketch, "E1397", {"start": v(33.63, -4) * mm, "end": v(33.5, -3.92) * mm});
            skLineSegment(sketch, "E1398", {"start": v(33.5, -3.92) * mm, "end": v(33.36, -3.84) * mm});
            skLineSegment(sketch, "E1399", {"start": v(33.36, -3.84) * mm, "end": v(33.22, -3.77) * mm});
            skLineSegment(sketch, "E1400", {"start": v(33.22, -3.77) * mm, "end": v(33.1, -3.7) * mm});
            skLineSegment(sketch, "E1401", {"start": v(33.1, -3.7) * mm, "end": v(32.96, -3.62) * mm});
            skLineSegment(sketch, "E1402", {"start": v(32.96, -3.62) * mm, "end": v(32.84, -3.56) * mm});
            skLineSegment(sketch, "E1403", {"start": v(32.84, -3.56) * mm, "end": v(32.72, -3.5) * mm});
            skLineSegment(sketch, "E1404", {"start": v(32.72, -3.5) * mm, "end": v(32.6, -3.44) * mm});
            skLineSegment(sketch, "E1405", {"start": v(32.6, -3.44) * mm, "end": v(32.48, -3.38) * mm});
            skLineSegment(sketch, "E1406", {"start": v(32.48, -3.38) * mm, "end": v(32.37, -3.33) * mm});
            skLineSegment(sketch, "E1407", {"start": v(32.37, -3.33) * mm, "end": v(32.26, -3.28) * mm});
            skLineSegment(sketch, "E1408", {"start": v(32.26, -3.28) * mm, "end": v(32.15, -3.23) * mm});
            skLineSegment(sketch, "E1409", {"start": v(32.15, -3.23) * mm, "end": v(32.05, -3.19) * mm});
            skLineSegment(sketch, "E1410", {"start": v(32.05, -3.19) * mm, "end": v(31.95, -3.14) * mm});
            skLineSegment(sketch, "E1411", {"start": v(31.95, -3.14) * mm, "end": v(31.85, -3.1) * mm});
            skLineSegment(sketch, "E1412", {"start": v(31.85, -3.1) * mm, "end": v(31.76, -3.07) * mm});
            skLineSegment(sketch, "E1413", {"start": v(31.76, -3.07) * mm, "end": v(31.67, -3.04) * mm});
            skLineSegment(sketch, "E1414", {"start": v(31.67, -3.04) * mm, "end": v(31.58, -3) * mm});
            skLineSegment(sketch, "E1415", {"start": v(31.58, -3) * mm, "end": v(31.5, -2.98) * mm});
            skLineSegment(sketch, "E1416", {"start": v(31.5, -2.98) * mm, "end": v(31.42, -2.95) * mm});
            skLineSegment(sketch, "E1417", {"start": v(31.42, -2.95) * mm, "end": v(31.34, -2.92) * mm});
            skLineSegment(sketch, "E1418", {"start": v(31.34, -2.92) * mm, "end": v(31.27, -2.9) * mm});
            skLineSegment(sketch, "E1419", {"start": v(31.27, -2.9) * mm, "end": v(31.2, -2.88) * mm});
            skLineSegment(sketch, "E1420", {"start": v(31.2, -2.88) * mm, "end": v(31.14, -2.86) * mm});
            skLineSegment(sketch, "E1421", {"start": v(31.14, -2.86) * mm, "end": v(31.08, -2.85) * mm});
            skLineSegment(sketch, "E1422", {"start": v(31.08, -2.85) * mm, "end": v(31.02, -2.83) * mm});
            skLineSegment(sketch, "E1423", {"start": v(31.02, -2.83) * mm, "end": v(30.97, -2.82) * mm});
            skLineSegment(sketch, "E1424", {"start": v(30.97, -2.82) * mm, "end": v(30.92, -2.8) * mm});
            skLineSegment(sketch, "E1425", {"start": v(30.92, -2.8) * mm, "end": v(30.88, -2.8) * mm});
            skLineSegment(sketch, "E1426", {"start": v(30.88, -2.8) * mm, "end": v(30.84, -2.8) * mm});
            skLineSegment(sketch, "E1427", {"start": v(30.84, -2.8) * mm, "end": v(30.8, -2.78) * mm});
            skLineSegment(sketch, "E1428", {"start": v(30.8, -2.78) * mm, "end": v(30.77, -2.78) * mm});
            skLineSegment(sketch, "E1429", {"start": v(30.77, -2.78) * mm, "end": v(30.74, -2.77) * mm});
            skLineSegment(sketch, "E1430", {"start": v(30.74, -2.77) * mm, "end": v(30.71, -2.77) * mm});
            skLineSegment(sketch, "E1431", {"start": v(30.71, -2.77) * mm, "end": v(30.7, -2.77) * mm});
            skLineSegment(sketch, "E1432", {"start": v(30.7, -2.77) * mm, "end": v(30.68, -2.76) * mm});
            skLineSegment(sketch, "E1433", {"start": v(30.68, -2.76) * mm, "end": v(30.66, -2.76) * mm});
            skLineSegment(sketch, "E1434", {"start": v(30.66, -2.76) * mm, "end": v(30.66, -2.76) * mm});
            skLineSegment(sketch, "E1435", {"start": v(30.66, -2.76) * mm, "end": v(30.12, -2.71) * mm});
            skLineSegment(sketch, "E1436", {"start": v(30.12, -2.71) * mm, "end": v(30.24, -0.39) * mm});
            skLineSegment(sketch, "E1437", {"start": v(30.24, -0.39) * mm, "end": v(30.78, -0.4) * mm});
            skLineSegment(sketch, "E1438", {"start": v(30.78, -0.4) * mm, "end": v(30.79, -0.4) * mm});
            skLineSegment(sketch, "E1439", {"start": v(30.79, -0.4) * mm, "end": v(30.8, -0.4) * mm});
            skLineSegment(sketch, "E1440", {"start": v(30.8, -0.4) * mm, "end": v(30.81, -0.4) * mm});
            skLineSegment(sketch, "E1441", {"start": v(30.81, -0.4) * mm, "end": v(30.84, -0.4) * mm});
            skLineSegment(sketch, "E1442", {"start": v(30.84, -0.4) * mm, "end": v(30.86, -0.4) * mm});
            skLineSegment(sketch, "E1443", {"start": v(30.86, -0.4) * mm, "end": v(30.89, -0.39) * mm});
            skLineSegment(sketch, "E1444", {"start": v(30.89, -0.39) * mm, "end": v(30.92, -0.39) * mm});
            skLineSegment(sketch, "E1445", {"start": v(30.92, -0.39) * mm, "end": v(30.96, -0.38) * mm});
            skLineSegment(sketch, "E1446", {"start": v(30.96, -0.38) * mm, "end": v(31, -0.38) * mm});
            skLineSegment(sketch, "E1447", {"start": v(31, -0.38) * mm, "end": v(31.05, -0.37) * mm});
            skLineSegment(sketch, "E1448", {"start": v(31.05, -0.37) * mm, "end": v(31.1, -0.37) * mm});
            skLineSegment(sketch, "E1449", {"start": v(31.1, -0.37) * mm, "end": v(31.15, -0.36) * mm});
            skLineSegment(sketch, "E1450", {"start": v(31.15, -0.36) * mm, "end": v(31.2, -0.35) * mm});
            skLineSegment(sketch, "E1451", {"start": v(31.2, -0.35) * mm, "end": v(31.27, -0.34) * mm});
            skLineSegment(sketch, "E1452", {"start": v(31.27, -0.34) * mm, "end": v(31.34, -0.33) * mm});
            skLineSegment(sketch, "E1453", {"start": v(31.34, -0.33) * mm, "end": v(31.4, -0.32) * mm});
            skLineSegment(sketch, "E1454", {"start": v(31.4, -0.32) * mm, "end": v(31.48, -0.3) * mm});
            skLineSegment(sketch, "E1455", {"start": v(31.48, -0.3) * mm, "end": v(31.56, -0.29) * mm});
            skLineSegment(sketch, "E1456", {"start": v(31.56, -0.29) * mm, "end": v(31.64, -0.27) * mm});
            skLineSegment(sketch, "E1457", {"start": v(31.64, -0.27) * mm, "end": v(31.72, -0.25) * mm});
            skLineSegment(sketch, "E1458", {"start": v(31.72, -0.25) * mm, "end": v(31.81, -0.23) * mm});
            skLineSegment(sketch, "E1459", {"start": v(31.81, -0.23) * mm, "end": v(31.9, -0.2) * mm});
            skLineSegment(sketch, "E1460", {"start": v(31.9, -0.2) * mm, "end": v(32, -0.17) * mm});
            skLineSegment(sketch, "E1461", {"start": v(32, -0.17) * mm, "end": v(32.1, -0.15) * mm});
            skLineSegment(sketch, "E1462", {"start": v(32.1, -0.15) * mm, "end": v(32.2, -0.12) * mm});
            skLineSegment(sketch, "E1463", {"start": v(32.2, -0.12) * mm, "end": v(32.31, -0.08) * mm});
            skLineSegment(sketch, "E1464", {"start": v(32.31, -0.08) * mm, "end": v(32.42, -0.05) * mm});
            skLineSegment(sketch, "E1465", {"start": v(32.42, -0.05) * mm, "end": v(32.54, 0) * mm});
            skLineSegment(sketch, "E1466", {"start": v(32.54, 0) * mm, "end": v(32.66, 0.03) * mm});
            skLineSegment(sketch, "E1467", {"start": v(32.66, 0.03) * mm, "end": v(32.78, 0.08) * mm});
            skLineSegment(sketch, "E1468", {"start": v(32.78, 0.08) * mm, "end": v(32.9, 0.12) * mm});
            skLineSegment(sketch, "E1469", {"start": v(32.9, 0.12) * mm, "end": v(33.03, 0.17) * mm});
            skLineSegment(sketch, "E1470", {"start": v(33.03, 0.17) * mm, "end": v(33.16, 0.23) * mm});
            skLineSegment(sketch, "E1471", {"start": v(33.16, 0.23) * mm, "end": v(33.3, 0.28) * mm});
            skLineSegment(sketch, "E1472", {"start": v(33.3, 0.28) * mm, "end": v(33.43, 0.34) * mm});
            skLineSegment(sketch, "E1473", {"start": v(33.43, 0.34) * mm, "end": v(33.57, 0.4) * mm});
            skLineSegment(sketch, "E1474", {"start": v(33.57, 0.4) * mm, "end": v(33.72, 0.47) * mm});
            skLineSegment(sketch, "E1475", {"start": v(33.72, 0.47) * mm, "end": v(33.87, 0.54) * mm});
            skLineSegment(sketch, "E1476", {"start": v(33.87, 0.54) * mm, "end": v(34.02, 0.61) * mm});
            skLineSegment(sketch, "E1477", {"start": v(34.02, 0.61) * mm, "end": v(34.17, 0.7) * mm});
            skLineSegment(sketch, "E1478", {"start": v(34.17, 0.7) * mm, "end": v(34.32, 0.77) * mm});
            skLineSegment(sketch, "E1479", {"start": v(34.32, 0.77) * mm, "end": v(34.48, 0.85) * mm});
            skLineSegment(sketch, "E1480", {"start": v(34.48, 0.85) * mm, "end": v(34.64, 0.94) * mm});
            skLineSegment(sketch, "E1481", {"start": v(34.64, 0.94) * mm, "end": v(34.8, 1.03) * mm});
            skLineSegment(sketch, "E1482", {"start": v(34.8, 1.03) * mm, "end": v(34.92, 1.13) * mm});
            skLineSegment(sketch, "E1483", {"start": v(34.92, 1.13) * mm, "end": v(34.84, 2.6) * mm});
            skLineSegment(sketch, "E1484", {"start": v(34.84, 2.6) * mm, "end": v(34.72, 2.68) * mm});
            skLineSegment(sketch, "E1485", {"start": v(34.72, 2.68) * mm, "end": v(34.55, 2.76) * mm});
            skLineSegment(sketch, "E1486", {"start": v(34.55, 2.76) * mm, "end": v(34.38, 2.83) * mm});
            skLineSegment(sketch, "E1487", {"start": v(34.38, 2.83) * mm, "end": v(34.21, 2.9) * mm});
            skLineSegment(sketch, "E1488", {"start": v(34.21, 2.9) * mm, "end": v(34.05, 2.96) * mm});
            skLineSegment(sketch, "E1489", {"start": v(34.05, 2.96) * mm, "end": v(33.89, 3.02) * mm});
            skLineSegment(sketch, "E1490", {"start": v(33.89, 3.02) * mm, "end": v(33.73, 3.07) * mm});
            skLineSegment(sketch, "E1491", {"start": v(33.73, 3.07) * mm, "end": v(33.58, 3.13) * mm});
            skLineSegment(sketch, "E1492", {"start": v(33.58, 3.13) * mm, "end": v(33.43, 3.18) * mm});
            skLineSegment(sketch, "E1493", {"start": v(33.43, 3.18) * mm, "end": v(33.28, 3.22) * mm});
            skLineSegment(sketch, "E1494", {"start": v(33.28, 3.22) * mm, "end": v(33.14, 3.27) * mm});
            skLineSegment(sketch, "E1495", {"start": v(33.14, 3.27) * mm, "end": v(33, 3.3) * mm});
            skLineSegment(sketch, "E1496", {"start": v(33, 3.3) * mm, "end": v(32.86, 3.35) * mm});
            skLineSegment(sketch, "E1497", {"start": v(32.86, 3.35) * mm, "end": v(32.73, 3.38) * mm});
            skLineSegment(sketch, "E1498", {"start": v(32.73, 3.38) * mm, "end": v(32.6, 3.42) * mm});
            skLineSegment(sketch, "E1499", {"start": v(32.6, 3.42) * mm, "end": v(32.47, 3.45) * mm});
            skLineSegment(sketch, "E1500", {"start": v(32.47, 3.45) * mm, "end": v(32.35, 3.48) * mm});
            skLineSegment(sketch, "E1501", {"start": v(32.35, 3.48) * mm, "end": v(32.23, 3.5) * mm});
            skLineSegment(sketch, "E1502", {"start": v(32.23, 3.5) * mm, "end": v(32.12, 3.53) * mm});
            skLineSegment(sketch, "E1503", {"start": v(32.12, 3.53) * mm, "end": v(32, 3.55) * mm});
            skLineSegment(sketch, "E1504", {"start": v(32, 3.55) * mm, "end": v(31.9, 3.57) * mm});
            skLineSegment(sketch, "E1505", {"start": v(31.9, 3.57) * mm, "end": v(31.8, 3.58) * mm});
            skLineSegment(sketch, "E1506", {"start": v(31.8, 3.58) * mm, "end": v(31.7, 3.6) * mm});
            skLineSegment(sketch, "E1507", {"start": v(31.7, 3.6) * mm, "end": v(31.6, 3.61) * mm});
            skLineSegment(sketch, "E1508", {"start": v(31.6, 3.61) * mm, "end": v(31.52, 3.63) * mm});
            skLineSegment(sketch, "E1509", {"start": v(31.52, 3.63) * mm, "end": v(31.43, 3.64) * mm});
            skLineSegment(sketch, "E1510", {"start": v(31.43, 3.64) * mm, "end": v(31.35, 3.65) * mm});
            skLineSegment(sketch, "E1511", {"start": v(31.35, 3.65) * mm, "end": v(31.27, 3.66) * mm});
            skLineSegment(sketch, "E1512", {"start": v(31.27, 3.66) * mm, "end": v(31.2, 3.66) * mm});
            skLineSegment(sketch, "E1513", {"start": v(31.2, 3.66) * mm, "end": v(31.12, 3.67) * mm});
            skLineSegment(sketch, "E1514", {"start": v(31.12, 3.67) * mm, "end": v(31.06, 3.67) * mm});
            skLineSegment(sketch, "E1515", {"start": v(31.06, 3.67) * mm, "end": v(31, 3.68) * mm});
            skLineSegment(sketch, "E1516", {"start": v(31, 3.68) * mm, "end": v(30.93, 3.68) * mm});
            skLineSegment(sketch, "E1517", {"start": v(30.93, 3.68) * mm, "end": v(30.88, 3.68) * mm});
            skLineSegment(sketch, "E1518", {"start": v(30.88, 3.68) * mm, "end": v(30.83, 3.68) * mm});
            skLineSegment(sketch, "E1519", {"start": v(30.83, 3.68) * mm, "end": v(30.78, 3.68) * mm});
            skLineSegment(sketch, "E1520", {"start": v(30.78, 3.68) * mm, "end": v(30.74, 3.68) * mm});
            skLineSegment(sketch, "E1521", {"start": v(30.74, 3.68) * mm, "end": v(30.7, 3.68) * mm});
            skLineSegment(sketch, "E1522", {"start": v(30.7, 3.68) * mm, "end": v(30.67, 3.68) * mm});
            skLineSegment(sketch, "E1523", {"start": v(30.67, 3.68) * mm, "end": v(30.64, 3.68) * mm});
            skLineSegment(sketch, "E1524", {"start": v(30.64, 3.68) * mm, "end": v(30.62, 3.68) * mm});
            skLineSegment(sketch, "E1525", {"start": v(30.62, 3.68) * mm, "end": v(30.6, 3.68) * mm});
            skLineSegment(sketch, "E1526", {"start": v(30.6, 3.68) * mm, "end": v(30.58, 3.68) * mm});
            skLineSegment(sketch, "E1527", {"start": v(30.58, 3.68) * mm, "end": v(30.57, 3.67) * mm});
            skLineSegment(sketch, "E1528", {"start": v(30.57, 3.67) * mm, "end": v(30.56, 3.67) * mm});
            skLineSegment(sketch, "E1529", {"start": v(30.56, 3.67) * mm, "end": v(30.02, 3.6) * mm});
            skLineSegment(sketch, "E1530", {"start": v(30.02, 3.6) * mm, "end": v(29.66, 5.9) * mm});
            skLineSegment(sketch, "E1531", {"start": v(29.66, 5.9) * mm, "end": v(30.19, 6.01) * mm});
            skLineSegment(sketch, "E1532", {"start": v(30.19, 6.01) * mm, "end": v(30.2, 6.01) * mm});
            skLineSegment(sketch, "E1533", {"start": v(30.2, 6.01) * mm, "end": v(30.2, 6.02) * mm});
            skLineSegment(sketch, "E1534", {"start": v(30.2, 6.02) * mm, "end": v(30.22, 6.02) * mm});
            skLineSegment(sketch, "E1535", {"start": v(30.22, 6.02) * mm, "end": v(30.24, 6.03) * mm});
            skLineSegment(sketch, "E1536", {"start": v(30.24, 6.03) * mm, "end": v(30.27, 6.03) * mm});
            skLineSegment(sketch, "E1537", {"start": v(30.27, 6.03) * mm, "end": v(30.3, 6.04) * mm});
            skLineSegment(sketch, "E1538", {"start": v(30.3, 6.04) * mm, "end": v(30.33, 6.05) * mm});
            skLineSegment(sketch, "E1539", {"start": v(30.33, 6.05) * mm, "end": v(30.36, 6.06) * mm});
            skLineSegment(sketch, "E1540", {"start": v(30.36, 6.06) * mm, "end": v(30.4, 6.07) * mm});
            skLineSegment(sketch, "E1541", {"start": v(30.4, 6.07) * mm, "end": v(30.45, 6.09) * mm});
            skLineSegment(sketch, "E1542", {"start": v(30.45, 6.09) * mm, "end": v(30.5, 6.1) * mm});
            skLineSegment(sketch, "E1543", {"start": v(30.5, 6.1) * mm, "end": v(30.54, 6.12) * mm});
            skLineSegment(sketch, "E1544", {"start": v(30.54, 6.12) * mm, "end": v(30.6, 6.15) * mm});
            skLineSegment(sketch, "E1545", {"start": v(30.6, 6.15) * mm, "end": v(30.66, 6.17) * mm});
            skLineSegment(sketch, "E1546", {"start": v(30.66, 6.17) * mm, "end": v(30.72, 6.2) * mm});
            skLineSegment(sketch, "E1547", {"start": v(30.72, 6.2) * mm, "end": v(30.78, 6.22) * mm});
            skLineSegment(sketch, "E1548", {"start": v(30.78, 6.22) * mm, "end": v(30.85, 6.25) * mm});
            skLineSegment(sketch, "E1549", {"start": v(30.85, 6.25) * mm, "end": v(30.93, 6.28) * mm});
            skLineSegment(sketch, "E1550", {"start": v(30.93, 6.28) * mm, "end": v(31, 6.32) * mm});
            skLineSegment(sketch, "E1551", {"start": v(31, 6.32) * mm, "end": v(31.08, 6.35) * mm});
            skLineSegment(sketch, "E1552", {"start": v(31.08, 6.35) * mm, "end": v(31.16, 6.4) * mm});
            skLineSegment(sketch, "E1553", {"start": v(31.16, 6.4) * mm, "end": v(31.25, 6.44) * mm});
            skLineSegment(sketch, "E1554", {"start": v(31.25, 6.44) * mm, "end": v(31.34, 6.48) * mm});
            skLineSegment(sketch, "E1555", {"start": v(31.34, 6.48) * mm, "end": v(31.43, 6.53) * mm});
            skLineSegment(sketch, "E1556", {"start": v(31.43, 6.53) * mm, "end": v(31.52, 6.58) * mm});
            skLineSegment(sketch, "E1557", {"start": v(31.52, 6.58) * mm, "end": v(31.62, 6.64) * mm});
            skLineSegment(sketch, "E1558", {"start": v(31.62, 6.64) * mm, "end": v(31.72, 6.7) * mm});
            skLineSegment(sketch, "E1559", {"start": v(31.72, 6.7) * mm, "end": v(31.83, 6.76) * mm});
            skLineSegment(sketch, "E1560", {"start": v(31.83, 6.76) * mm, "end": v(31.93, 6.82) * mm});
            skLineSegment(sketch, "E1561", {"start": v(31.93, 6.82) * mm, "end": v(32.04, 6.9) * mm});
            skLineSegment(sketch, "E1562", {"start": v(32.04, 6.9) * mm, "end": v(32.16, 6.96) * mm});
            skLineSegment(sketch, "E1563", {"start": v(32.16, 6.96) * mm, "end": v(32.27, 7.04) * mm});
            skLineSegment(sketch, "E1564", {"start": v(32.27, 7.04) * mm, "end": v(32.39, 7.12) * mm});
            skLineSegment(sketch, "E1565", {"start": v(32.39, 7.12) * mm, "end": v(32.5, 7.2) * mm});
            skLineSegment(sketch, "E1566", {"start": v(32.5, 7.2) * mm, "end": v(32.63, 7.29) * mm});
            skLineSegment(sketch, "E1567", {"start": v(32.63, 7.29) * mm, "end": v(32.76, 7.38) * mm});
            skLineSegment(sketch, "E1568", {"start": v(32.76, 7.38) * mm, "end": v(32.88, 7.47) * mm});
            skLineSegment(sketch, "E1569", {"start": v(32.88, 7.47) * mm, "end": v(33.01, 7.57) * mm});
            skLineSegment(sketch, "E1570", {"start": v(33.01, 7.57) * mm, "end": v(33.14, 7.67) * mm});
            skLineSegment(sketch, "E1571", {"start": v(33.14, 7.67) * mm, "end": v(33.28, 7.78) * mm});
            skLineSegment(sketch, "E1572", {"start": v(33.28, 7.78) * mm, "end": v(33.41, 7.89) * mm});
            skLineSegment(sketch, "E1573", {"start": v(33.41, 7.89) * mm, "end": v(33.55, 8) * mm});
            skLineSegment(sketch, "E1574", {"start": v(33.55, 8) * mm, "end": v(33.69, 8.12) * mm});
            skLineSegment(sketch, "E1575", {"start": v(33.69, 8.12) * mm, "end": v(33.83, 8.25) * mm});
            skLineSegment(sketch, "E1576", {"start": v(33.83, 8.25) * mm, "end": v(33.92, 8.36) * mm});
            skLineSegment(sketch, "E1577", {"start": v(33.92, 8.36) * mm, "end": v(33.53, 9.79) * mm});
            skLineSegment(sketch, "E1578", {"start": v(33.53, 9.79) * mm, "end": v(33.4, 9.84) * mm});
            skLineSegment(sketch, "E1579", {"start": v(33.4, 9.84) * mm, "end": v(33.22, 9.88) * mm});
            skLineSegment(sketch, "E1580", {"start": v(33.22, 9.88) * mm, "end": v(33.04, 9.91) * mm});
            skLineSegment(sketch, "E1581", {"start": v(33.04, 9.91) * mm, "end": v(32.86, 9.94) * mm});
            skLineSegment(sketch, "E1582", {"start": v(32.86, 9.94) * mm, "end": v(32.69, 9.97) * mm});
            skLineSegment(sketch, "E1583", {"start": v(32.69, 9.97) * mm, "end": v(32.52, 10) * mm});
            skLineSegment(sketch, "E1584", {"start": v(32.52, 10) * mm, "end": v(32.35, 10.02) * mm});
            skLineSegment(sketch, "E1585", {"start": v(32.35, 10.02) * mm, "end": v(32.2, 10.04) * mm});
            skLineSegment(sketch, "E1586", {"start": v(32.2, 10.04) * mm, "end": v(32.04, 10.06) * mm});
            skLineSegment(sketch, "E1587", {"start": v(32.04, 10.06) * mm, "end": v(31.88, 10.07) * mm});
            skLineSegment(sketch, "E1588", {"start": v(31.88, 10.07) * mm, "end": v(31.73, 10.09) * mm});
            skLineSegment(sketch, "E1589", {"start": v(31.73, 10.09) * mm, "end": v(31.59, 10.1) * mm});
            skLineSegment(sketch, "E1590", {"start": v(31.59, 10.1) * mm, "end": v(31.45, 10.1) * mm});
            skLineSegment(sketch, "E1591", {"start": v(31.45, 10.1) * mm, "end": v(31.3, 10.11) * mm});
            skLineSegment(sketch, "E1592", {"start": v(31.3, 10.11) * mm, "end": v(31.18, 10.12) * mm});
            skLineSegment(sketch, "E1593", {"start": v(31.18, 10.12) * mm, "end": v(31.05, 10.12) * mm});
            skLineSegment(sketch, "E1594", {"start": v(31.05, 10.12) * mm, "end": v(30.92, 10.13) * mm});
            skLineSegment(sketch, "E1595", {"start": v(30.92, 10.13) * mm, "end": v(30.8, 10.13) * mm});
            skLineSegment(sketch, "E1596", {"start": v(30.8, 10.13) * mm, "end": v(30.68, 10.13) * mm});
            skLineSegment(sketch, "E1597", {"start": v(30.68, 10.13) * mm, "end": v(30.57, 10.12) * mm});
            skLineSegment(sketch, "E1598", {"start": v(30.57, 10.12) * mm, "end": v(30.46, 10.12) * mm});
            skLineSegment(sketch, "E1599", {"start": v(30.46, 10.12) * mm, "end": v(30.36, 10.12) * mm});
            skLineSegment(sketch, "E1600", {"start": v(30.36, 10.12) * mm, "end": v(30.26, 10.11) * mm});
            skLineSegment(sketch, "E1601", {"start": v(30.26, 10.11) * mm, "end": v(30.16, 10.1) * mm});
            skLineSegment(sketch, "E1602", {"start": v(30.16, 10.1) * mm, "end": v(30.07, 10.1) * mm});
            skLineSegment(sketch, "E1603", {"start": v(30.07, 10.1) * mm, "end": v(29.99, 10.1) * mm});
            skLineSegment(sketch, "E1604", {"start": v(29.99, 10.1) * mm, "end": v(29.9, 10.09) * mm});
            skLineSegment(sketch, "E1605", {"start": v(29.9, 10.09) * mm, "end": v(29.82, 10.08) * mm});
            skLineSegment(sketch, "E1606", {"start": v(29.82, 10.08) * mm, "end": v(29.75, 10.07) * mm});
            skLineSegment(sketch, "E1607", {"start": v(29.75, 10.07) * mm, "end": v(29.68, 10.06) * mm});
            skLineSegment(sketch, "E1608", {"start": v(29.68, 10.06) * mm, "end": v(29.61, 10.05) * mm});
            skLineSegment(sketch, "E1609", {"start": v(29.61, 10.05) * mm, "end": v(29.55, 10.04) * mm});
            skLineSegment(sketch, "E1610", {"start": v(29.55, 10.04) * mm, "end": v(29.5, 10.03) * mm});
            skLineSegment(sketch, "E1611", {"start": v(29.5, 10.03) * mm, "end": v(29.44, 10.02) * mm});
            skLineSegment(sketch, "E1612", {"start": v(29.44, 10.02) * mm, "end": v(29.4, 10.01) * mm});
            skLineSegment(sketch, "E1613", {"start": v(29.4, 10.01) * mm, "end": v(29.35, 10) * mm});
            skLineSegment(sketch, "E1614", {"start": v(29.35, 10) * mm, "end": v(29.3, 10) * mm});
            skLineSegment(sketch, "E1615", {"start": v(29.3, 10) * mm, "end": v(29.27, 9.98) * mm});
            skLineSegment(sketch, "E1616", {"start": v(29.27, 9.98) * mm, "end": v(29.24, 9.98) * mm});
            skLineSegment(sketch, "E1617", {"start": v(29.24, 9.98) * mm, "end": v(29.2, 9.97) * mm});
            skLineSegment(sketch, "E1618", {"start": v(29.2, 9.97) * mm, "end": v(29.18, 9.96) * mm});
            skLineSegment(sketch, "E1619", {"start": v(29.18, 9.96) * mm, "end": v(29.16, 9.96) * mm});
            skLineSegment(sketch, "E1620", {"start": v(29.16, 9.96) * mm, "end": v(29.15, 9.95) * mm});
            skLineSegment(sketch, "E1621", {"start": v(29.15, 9.95) * mm, "end": v(29.14, 9.95) * mm});
            skLineSegment(sketch, "E1622", {"start": v(29.14, 9.95) * mm, "end": v(29.13, 9.95) * mm});
            skLineSegment(sketch, "E1623", {"start": v(29.13, 9.95) * mm, "end": v(28.62, 9.77) * mm});
            skLineSegment(sketch, "E1624", {"start": v(28.62, 9.77) * mm, "end": v(27.78, 11.94) * mm});
            skLineSegment(sketch, "E1625", {"start": v(27.78, 11.94) * mm, "end": v(28.28, 12.16) * mm});
            skLineSegment(sketch, "E1626", {"start": v(28.28, 12.16) * mm, "end": v(28.28, 12.16) * mm});
            skLineSegment(sketch, "E1627", {"start": v(28.28, 12.16) * mm, "end": v(28.3, 12.17) * mm});
            skLineSegment(sketch, "E1628", {"start": v(28.3, 12.17) * mm, "end": v(28.31, 12.17) * mm});
            skLineSegment(sketch, "E1629", {"start": v(28.31, 12.17) * mm, "end": v(28.33, 12.18) * mm});
            skLineSegment(sketch, "E1630", {"start": v(28.33, 12.18) * mm, "end": v(28.35, 12.2) * mm});
            skLineSegment(sketch, "E1631", {"start": v(28.35, 12.2) * mm, "end": v(28.38, 12.2) * mm});
            skLineSegment(sketch, "E1632", {"start": v(28.38, 12.2) * mm, "end": v(28.4, 12.22) * mm});
            skLineSegment(sketch, "E1633", {"start": v(28.4, 12.22) * mm, "end": v(28.44, 12.24) * mm});
            skLineSegment(sketch, "E1634", {"start": v(28.44, 12.24) * mm, "end": v(28.48, 12.26) * mm});
            skLineSegment(sketch, "E1635", {"start": v(28.48, 12.26) * mm, "end": v(28.51, 12.29) * mm});
            skLineSegment(sketch, "E1636", {"start": v(28.51, 12.29) * mm, "end": v(28.56, 12.31) * mm});
            skLineSegment(sketch, "E1637", {"start": v(28.56, 12.31) * mm, "end": v(28.6, 12.34) * mm});
            skLineSegment(sketch, "E1638", {"start": v(28.6, 12.34) * mm, "end": v(28.65, 12.37) * mm});
            skLineSegment(sketch, "E1639", {"start": v(28.65, 12.37) * mm, "end": v(28.7, 12.4) * mm});
            skLineSegment(sketch, "E1640", {"start": v(28.7, 12.4) * mm, "end": v(28.76, 12.44) * mm});
            skLineSegment(sketch, "E1641", {"start": v(28.76, 12.44) * mm, "end": v(28.82, 12.48) * mm});
            skLineSegment(sketch, "E1642", {"start": v(28.82, 12.48) * mm, "end": v(28.88, 12.53) * mm});
            skLineSegment(sketch, "E1643", {"start": v(28.88, 12.53) * mm, "end": v(28.94, 12.57) * mm});
            skLineSegment(sketch, "E1644", {"start": v(28.94, 12.57) * mm, "end": v(29.01, 12.62) * mm});
            skLineSegment(sketch, "E1645", {"start": v(29.01, 12.62) * mm, "end": v(29.08, 12.68) * mm});
            skLineSegment(sketch, "E1646", {"start": v(29.08, 12.68) * mm, "end": v(29.15, 12.73) * mm});
            skLineSegment(sketch, "E1647", {"start": v(29.15, 12.73) * mm, "end": v(29.23, 12.8) * mm});
            skLineSegment(sketch, "E1648", {"start": v(29.23, 12.8) * mm, "end": v(29.3, 12.86) * mm});
            skLineSegment(sketch, "E1649", {"start": v(29.3, 12.86) * mm, "end": v(29.38, 12.92) * mm});
            skLineSegment(sketch, "E1650", {"start": v(29.38, 12.92) * mm, "end": v(29.47, 13) * mm});
            skLineSegment(sketch, "E1651", {"start": v(29.47, 13) * mm, "end": v(29.55, 13.07) * mm});
            skLineSegment(sketch, "E1652", {"start": v(29.55, 13.07) * mm, "end": v(29.64, 13.15) * mm});
            skLineSegment(sketch, "E1653", {"start": v(29.64, 13.15) * mm, "end": v(29.73, 13.23) * mm});
            skLineSegment(sketch, "E1654", {"start": v(29.73, 13.23) * mm, "end": v(29.82, 13.31) * mm});
            skLineSegment(sketch, "E1655", {"start": v(29.82, 13.31) * mm, "end": v(29.91, 13.4) * mm});
            skLineSegment(sketch, "E1656", {"start": v(29.91, 13.4) * mm, "end": v(30, 13.5) * mm});
            skLineSegment(sketch, "E1657", {"start": v(30, 13.5) * mm, "end": v(30.1, 13.6) * mm});
            skLineSegment(sketch, "E1658", {"start": v(30.1, 13.6) * mm, "end": v(30.2, 13.7) * mm});
            skLineSegment(sketch, "E1659", {"start": v(30.2, 13.7) * mm, "end": v(30.3, 13.8) * mm});
            skLineSegment(sketch, "E1660", {"start": v(30.3, 13.8) * mm, "end": v(30.4, 13.91) * mm});
            skLineSegment(sketch, "E1661", {"start": v(30.4, 13.91) * mm, "end": v(30.5, 14.03) * mm});
            skLineSegment(sketch, "E1662", {"start": v(30.5, 14.03) * mm, "end": v(30.61, 14.15) * mm});
            skLineSegment(sketch, "E1663", {"start": v(30.61, 14.15) * mm, "end": v(30.72, 14.27) * mm});
            skLineSegment(sketch, "E1664", {"start": v(30.72, 14.27) * mm, "end": v(30.82, 14.4) * mm});
            skLineSegment(sketch, "E1665", {"start": v(30.82, 14.4) * mm, "end": v(30.93, 14.53) * mm});
            skLineSegment(sketch, "E1666", {"start": v(30.93, 14.53) * mm, "end": v(31.04, 14.66) * mm});
            skLineSegment(sketch, "E1667", {"start": v(31.04, 14.66) * mm, "end": v(31.15, 14.8) * mm});
            skLineSegment(sketch, "E1668", {"start": v(31.15, 14.8) * mm, "end": v(31.26, 14.95) * mm});
            skLineSegment(sketch, "E1669", {"start": v(31.26, 14.95) * mm, "end": v(31.38, 15.1) * mm});
            skLineSegment(sketch, "E1670", {"start": v(31.38, 15.1) * mm, "end": v(31.44, 15.23) * mm});
            skLineSegment(sketch, "E1671", {"start": v(31.44, 15.23) * mm, "end": v(30.77, 16.55) * mm});
            skLineSegment(sketch, "E1672", {"start": v(30.77, 16.55) * mm, "end": v(30.63, 16.57) * mm});
            skLineSegment(sketch, "E1673", {"start": v(30.63, 16.57) * mm, "end": v(30.44, 16.57) * mm});
            skLineSegment(sketch, "E1674", {"start": v(30.44, 16.57) * mm, "end": v(30.25, 16.56) * mm});
            skLineSegment(sketch, "E1675", {"start": v(30.25, 16.56) * mm, "end": v(30.08, 16.56) * mm});
            skLineSegment(sketch, "E1676", {"start": v(30.08, 16.56) * mm, "end": v(29.9, 16.55) * mm});
            skLineSegment(sketch, "E1677", {"start": v(29.9, 16.55) * mm, "end": v(29.73, 16.54) * mm});
            skLineSegment(sketch, "E1678", {"start": v(29.73, 16.54) * mm, "end": v(29.56, 16.53) * mm});
            skLineSegment(sketch, "E1679", {"start": v(29.56, 16.53) * mm, "end": v(29.4, 16.51) * mm});
            skLineSegment(sketch, "E1680", {"start": v(29.4, 16.51) * mm, "end": v(29.24, 16.5) * mm});
            skLineSegment(sketch, "E1681", {"start": v(29.24, 16.5) * mm, "end": v(29.1, 16.48) * mm});
            skLineSegment(sketch, "E1682", {"start": v(29.1, 16.48) * mm, "end": v(28.94, 16.46) * mm});
            skLineSegment(sketch, "E1683", {"start": v(28.94, 16.46) * mm, "end": v(28.8, 16.44) * mm});
            skLineSegment(sketch, "E1684", {"start": v(28.8, 16.44) * mm, "end": v(28.66, 16.42) * mm});
            skLineSegment(sketch, "E1685", {"start": v(28.66, 16.42) * mm, "end": v(28.52, 16.4) * mm});
            skLineSegment(sketch, "E1686", {"start": v(28.52, 16.4) * mm, "end": v(28.4, 16.38) * mm});
            skLineSegment(sketch, "E1687", {"start": v(28.4, 16.38) * mm, "end": v(28.26, 16.36) * mm});
            skLineSegment(sketch, "E1688", {"start": v(28.26, 16.36) * mm, "end": v(28.14, 16.33) * mm});
            skLineSegment(sketch, "E1689", {"start": v(28.14, 16.33) * mm, "end": v(28.02, 16.3) * mm});
            skLineSegment(sketch, "E1690", {"start": v(28.02, 16.3) * mm, "end": v(27.9, 16.28) * mm});
            skLineSegment(sketch, "E1691", {"start": v(27.9, 16.28) * mm, "end": v(27.8, 16.26) * mm});
            skLineSegment(sketch, "E1692", {"start": v(27.8, 16.26) * mm, "end": v(27.7, 16.23) * mm});
            skLineSegment(sketch, "E1693", {"start": v(27.7, 16.23) * mm, "end": v(27.6, 16.2) * mm});
            skLineSegment(sketch, "E1694", {"start": v(27.6, 16.2) * mm, "end": v(27.5, 16.18) * mm});
            skLineSegment(sketch, "E1695", {"start": v(27.5, 16.18) * mm, "end": v(27.4, 16.16) * mm});
            skLineSegment(sketch, "E1696", {"start": v(27.4, 16.16) * mm, "end": v(27.32, 16.13) * mm});
            skLineSegment(sketch, "E1697", {"start": v(27.32, 16.13) * mm, "end": v(27.23, 16.1) * mm});
            skLineSegment(sketch, "E1698", {"start": v(27.23, 16.1) * mm, "end": v(27.15, 16.08) * mm});
            skLineSegment(sketch, "E1699", {"start": v(27.15, 16.08) * mm, "end": v(27.08, 16.06) * mm});
            skLineSegment(sketch, "E1700", {"start": v(27.08, 16.06) * mm, "end": v(27, 16.03) * mm});
            skLineSegment(sketch, "E1701", {"start": v(27, 16.03) * mm, "end": v(26.94, 16) * mm});
            skLineSegment(sketch, "E1702", {"start": v(26.94, 16) * mm, "end": v(26.88, 15.99) * mm});
            skLineSegment(sketch, "E1703", {"start": v(26.88, 15.99) * mm, "end": v(26.82, 15.96) * mm});
            skLineSegment(sketch, "E1704", {"start": v(26.82, 15.96) * mm, "end": v(26.76, 15.94) * mm});
            skLineSegment(sketch, "E1705", {"start": v(26.76, 15.94) * mm, "end": v(26.71, 15.92) * mm});
            skLineSegment(sketch, "E1706", {"start": v(26.71, 15.92) * mm, "end": v(26.67, 15.9) * mm});
            skLineSegment(sketch, "E1707", {"start": v(26.67, 15.9) * mm, "end": v(26.63, 15.88) * mm});
            skLineSegment(sketch, "E1708", {"start": v(26.63, 15.88) * mm, "end": v(26.59, 15.87) * mm});
            skLineSegment(sketch, "E1709", {"start": v(26.59, 15.87) * mm, "end": v(26.55, 15.85) * mm});
            skLineSegment(sketch, "E1710", {"start": v(26.55, 15.85) * mm, "end": v(26.52, 15.84) * mm});
            skLineSegment(sketch, "E1711", {"start": v(26.52, 15.84) * mm, "end": v(26.5, 15.82) * mm});
            skLineSegment(sketch, "E1712", {"start": v(26.5, 15.82) * mm, "end": v(26.47, 15.81) * mm});
            skLineSegment(sketch, "E1713", {"start": v(26.47, 15.81) * mm, "end": v(26.46, 15.8) * mm});
            skLineSegment(sketch, "E1714", {"start": v(26.46, 15.8) * mm, "end": v(26.44, 15.8) * mm});
            skLineSegment(sketch, "E1715", {"start": v(26.44, 15.8) * mm, "end": v(26.43, 15.79) * mm});
            skLineSegment(sketch, "E1716", {"start": v(26.43, 15.79) * mm, "end": v(26.42, 15.79) * mm});
            skLineSegment(sketch, "E1717", {"start": v(26.42, 15.79) * mm, "end": v(25.96, 15.5) * mm});
            skLineSegment(sketch, "E1718", {"start": v(25.96, 15.5) * mm, "end": v(24.69, 17.46) * mm});
            skLineSegment(sketch, "E1719", {"start": v(24.69, 17.46) * mm, "end": v(25.13, 17.77) * mm});
            skLineSegment(sketch, "E1720", {"start": v(25.13, 17.77) * mm, "end": v(25.14, 17.78) * mm});
            skLineSegment(sketch, "E1721", {"start": v(25.14, 17.78) * mm, "end": v(25.15, 17.78) * mm});
            skLineSegment(sketch, "E1722", {"start": v(25.15, 17.78) * mm, "end": v(25.16, 17.8) * mm});
            skLineSegment(sketch, "E1723", {"start": v(25.16, 17.8) * mm, "end": v(25.18, 17.8) * mm});
            skLineSegment(sketch, "E1724", {"start": v(25.18, 17.8) * mm, "end": v(25.2, 17.82) * mm});
            skLineSegment(sketch, "E1725", {"start": v(25.2, 17.82) * mm, "end": v(25.22, 17.84) * mm});
            skLineSegment(sketch, "E1726", {"start": v(25.22, 17.84) * mm, "end": v(25.24, 17.86) * mm});
            skLineSegment(sketch, "E1727", {"start": v(25.24, 17.86) * mm, "end": v(25.27, 17.89) * mm});
            skLineSegment(sketch, "E1728", {"start": v(25.27, 17.89) * mm, "end": v(25.3, 17.92) * mm});
            skLineSegment(sketch, "E1729", {"start": v(25.3, 17.92) * mm, "end": v(25.34, 17.95) * mm});
            skLineSegment(sketch, "E1730", {"start": v(25.34, 17.95) * mm, "end": v(25.37, 17.98) * mm});
            skLineSegment(sketch, "E1731", {"start": v(25.37, 17.98) * mm, "end": v(25.41, 18.02) * mm});
            skLineSegment(sketch, "E1732", {"start": v(25.41, 18.02) * mm, "end": v(25.45, 18.06) * mm});
            skLineSegment(sketch, "E1733", {"start": v(25.45, 18.06) * mm, "end": v(25.5, 18.1) * mm});
            skLineSegment(sketch, "E1734", {"start": v(25.5, 18.1) * mm, "end": v(25.54, 18.15) * mm});
            skLineSegment(sketch, "E1735", {"start": v(25.54, 18.15) * mm, "end": v(25.6, 18.2) * mm});
            skLineSegment(sketch, "E1736", {"start": v(25.6, 18.2) * mm, "end": v(25.64, 18.26) * mm});
            skLineSegment(sketch, "E1737", {"start": v(25.64, 18.26) * mm, "end": v(25.7, 18.32) * mm});
            skLineSegment(sketch, "E1738", {"start": v(25.7, 18.32) * mm, "end": v(25.75, 18.38) * mm});
            skLineSegment(sketch, "E1739", {"start": v(25.75, 18.38) * mm, "end": v(25.8, 18.45) * mm});
            skLineSegment(sketch, "E1740", {"start": v(25.8, 18.45) * mm, "end": v(25.87, 18.52) * mm});
            skLineSegment(sketch, "E1741", {"start": v(25.87, 18.52) * mm, "end": v(25.93, 18.6) * mm});
            skLineSegment(sketch, "E1742", {"start": v(25.93, 18.6) * mm, "end": v(26, 18.67) * mm});
            skLineSegment(sketch, "E1743", {"start": v(26, 18.67) * mm, "end": v(26.06, 18.75) * mm});
            skLineSegment(sketch, "E1744", {"start": v(26.06, 18.75) * mm, "end": v(26.12, 18.84) * mm});
            skLineSegment(sketch, "E1745", {"start": v(26.12, 18.84) * mm, "end": v(26.19, 18.93) * mm});
            skLineSegment(sketch, "E1746", {"start": v(26.19, 18.93) * mm, "end": v(26.26, 19.02) * mm});
            skLineSegment(sketch, "E1747", {"start": v(26.26, 19.02) * mm, "end": v(26.33, 19.12) * mm});
            skLineSegment(sketch, "E1748", {"start": v(26.33, 19.12) * mm, "end": v(26.4, 19.22) * mm});
            skLineSegment(sketch, "E1749", {"start": v(26.4, 19.22) * mm, "end": v(26.47, 19.33) * mm});
            skLineSegment(sketch, "E1750", {"start": v(26.47, 19.33) * mm, "end": v(26.54, 19.44) * mm});
            skLineSegment(sketch, "E1751", {"start": v(26.54, 19.44) * mm, "end": v(26.62, 19.56) * mm});
            skLineSegment(sketch, "E1752", {"start": v(26.62, 19.56) * mm, "end": v(26.7, 19.68) * mm});
            skLineSegment(sketch, "E1753", {"start": v(26.7, 19.68) * mm, "end": v(26.77, 19.8) * mm});
            skLineSegment(sketch, "E1754", {"start": v(26.77, 19.8) * mm, "end": v(26.85, 19.93) * mm});
            skLineSegment(sketch, "E1755", {"start": v(26.85, 19.93) * mm, "end": v(26.92, 20.06) * mm});
            skLineSegment(sketch, "E1756", {"start": v(26.92, 20.06) * mm, "end": v(27, 20.2) * mm});
            skLineSegment(sketch, "E1757", {"start": v(27, 20.2) * mm, "end": v(27.08, 20.34) * mm});
            skLineSegment(sketch, "E1758", {"start": v(27.08, 20.34) * mm, "end": v(27.16, 20.5) * mm});
            skLineSegment(sketch, "E1759", {"start": v(27.16, 20.5) * mm, "end": v(27.24, 20.64) * mm});
            skLineSegment(sketch, "E1760", {"start": v(27.24, 20.64) * mm, "end": v(27.32, 20.8) * mm});
            skLineSegment(sketch, "E1761", {"start": v(27.32, 20.8) * mm, "end": v(27.4, 20.96) * mm});
            skLineSegment(sketch, "E1762", {"start": v(27.4, 20.96) * mm, "end": v(27.47, 21.12) * mm});
            skLineSegment(sketch, "E1763", {"start": v(27.47, 21.12) * mm, "end": v(27.55, 21.3) * mm});
            skLineSegment(sketch, "E1764", {"start": v(27.55, 21.3) * mm, "end": v(27.58, 21.43) * mm});
            skLineSegment(sketch, "E1765", {"start": v(27.58, 21.43) * mm, "end": v(26.65, 22.58) * mm});
            skLineSegment(sketch, "E1766", {"start": v(26.65, 22.58) * mm, "end": v(26.51, 22.58) * mm});
            skLineSegment(sketch, "E1767", {"start": v(26.51, 22.58) * mm, "end": v(26.33, 22.54) * mm});
            skLineSegment(sketch, "E1768", {"start": v(26.33, 22.54) * mm, "end": v(26.15, 22.5) * mm});
            skLineSegment(sketch, "E1769", {"start": v(26.15, 22.5) * mm, "end": v(25.98, 22.45) * mm});
            skLineSegment(sketch, "E1770", {"start": v(25.98, 22.45) * mm, "end": v(25.8, 22.4) * mm});
            skLineSegment(sketch, "E1771", {"start": v(25.8, 22.4) * mm, "end": v(25.64, 22.36) * mm});
            skLineSegment(sketch, "E1772", {"start": v(25.64, 22.36) * mm, "end": v(25.48, 22.31) * mm});
            skLineSegment(sketch, "E1773", {"start": v(25.48, 22.31) * mm, "end": v(25.33, 22.26) * mm});
            skLineSegment(sketch, "E1774", {"start": v(25.33, 22.26) * mm, "end": v(25.18, 22.22) * mm});
            skLineSegment(sketch, "E1775", {"start": v(25.18, 22.22) * mm, "end": v(25.03, 22.17) * mm});
            skLineSegment(sketch, "E1776", {"start": v(25.03, 22.17) * mm, "end": v(24.89, 22.12) * mm});
            skLineSegment(sketch, "E1777", {"start": v(24.89, 22.12) * mm, "end": v(24.75, 22.07) * mm});
            skLineSegment(sketch, "E1778", {"start": v(24.75, 22.07) * mm, "end": v(24.62, 22.02) * mm});
            skLineSegment(sketch, "E1779", {"start": v(24.62, 22.02) * mm, "end": v(24.49, 21.97) * mm});
            skLineSegment(sketch, "E1780", {"start": v(24.49, 21.97) * mm, "end": v(24.36, 21.92) * mm});
            skLineSegment(sketch, "E1781", {"start": v(24.36, 21.92) * mm, "end": v(24.24, 21.88) * mm});
            skLineSegment(sketch, "E1782", {"start": v(24.24, 21.88) * mm, "end": v(24.13, 21.83) * mm});
            skLineSegment(sketch, "E1783", {"start": v(24.13, 21.83) * mm, "end": v(24.02, 21.78) * mm});
            skLineSegment(sketch, "E1784", {"start": v(24.02, 21.78) * mm, "end": v(23.91, 21.73) * mm});
            skLineSegment(sketch, "E1785", {"start": v(23.91, 21.73) * mm, "end": v(23.81, 21.68) * mm});
            skLineSegment(sketch, "E1786", {"start": v(23.81, 21.68) * mm, "end": v(23.71, 21.64) * mm});
            skLineSegment(sketch, "E1787", {"start": v(23.71, 21.64) * mm, "end": v(23.62, 21.6) * mm});
            skLineSegment(sketch, "E1788", {"start": v(23.62, 21.6) * mm, "end": v(23.53, 21.55) * mm});
            skLineSegment(sketch, "E1789", {"start": v(23.53, 21.55) * mm, "end": v(23.45, 21.5) * mm});
            skLineSegment(sketch, "E1790", {"start": v(23.45, 21.5) * mm, "end": v(23.36, 21.46) * mm});
            skLineSegment(sketch, "E1791", {"start": v(23.36, 21.46) * mm, "end": v(23.29, 21.42) * mm});
            skLineSegment(sketch, "E1792", {"start": v(23.29, 21.42) * mm, "end": v(23.22, 21.38) * mm});
            skLineSegment(sketch, "E1793", {"start": v(23.22, 21.38) * mm, "end": v(23.15, 21.34) * mm});
            skLineSegment(sketch, "E1794", {"start": v(23.15, 21.34) * mm, "end": v(23.08, 21.3) * mm});
            skLineSegment(sketch, "E1795", {"start": v(23.08, 21.3) * mm, "end": v(23.02, 21.26) * mm});
            skLineSegment(sketch, "E1796", {"start": v(23.02, 21.26) * mm, "end": v(22.97, 21.22) * mm});
            skLineSegment(sketch, "E1797", {"start": v(22.97, 21.22) * mm, "end": v(22.91, 21.2) * mm});
            skLineSegment(sketch, "E1798", {"start": v(22.91, 21.2) * mm, "end": v(22.86, 21.16) * mm});
            skLineSegment(sketch, "E1799", {"start": v(22.86, 21.16) * mm, "end": v(22.82, 21.13) * mm});
            skLineSegment(sketch, "E1800", {"start": v(22.82, 21.13) * mm, "end": v(22.78, 21.1) * mm});
            skLineSegment(sketch, "E1801", {"start": v(22.78, 21.1) * mm, "end": v(22.74, 21.07) * mm});
            skLineSegment(sketch, "E1802", {"start": v(22.74, 21.07) * mm, "end": v(22.7, 21.05) * mm});
            skLineSegment(sketch, "E1803", {"start": v(22.7, 21.05) * mm, "end": v(22.68, 21.03) * mm});
            skLineSegment(sketch, "E1804", {"start": v(22.68, 21.03) * mm, "end": v(22.65, 21) * mm});
            skLineSegment(sketch, "E1805", {"start": v(22.65, 21) * mm, "end": v(22.63, 20.99) * mm});
            skLineSegment(sketch, "E1806", {"start": v(22.63, 20.99) * mm, "end": v(22.6, 20.97) * mm});
            skLineSegment(sketch, "E1807", {"start": v(22.6, 20.97) * mm, "end": v(22.6, 20.96) * mm});
            skLineSegment(sketch, "E1808", {"start": v(22.6, 20.96) * mm, "end": v(22.58, 20.95) * mm});
            skLineSegment(sketch, "E1809", {"start": v(22.58, 20.95) * mm, "end": v(22.57, 20.94) * mm});
            skLineSegment(sketch, "E1810", {"start": v(22.57, 20.94) * mm, "end": v(22.56, 20.93) * mm});
            skLineSegment(sketch, "E1811", {"start": v(22.56, 20.93) * mm, "end": v(22.17, 20.57) * mm});
            skLineSegment(sketch, "E1812", {"start": v(22.17, 20.57) * mm, "end": v(20.52, 22.21) * mm});
            skLineSegment(sketch, "E1813", {"start": v(20.52, 22.21) * mm, "end": v(20.89, 22.6) * mm});
            skLineSegment(sketch, "E1814", {"start": v(20.89, 22.6) * mm, "end": v(20.9, 22.61) * mm});
            skLineSegment(sketch, "E1815", {"start": v(20.9, 22.61) * mm, "end": v(20.9, 22.62) * mm});
            skLineSegment(sketch, "E1816", {"start": v(20.9, 22.62) * mm, "end": v(20.91, 22.64) * mm});
            skLineSegment(sketch, "E1817", {"start": v(20.91, 22.64) * mm, "end": v(20.92, 22.65) * mm});
            skLineSegment(sketch, "E1818", {"start": v(20.92, 22.65) * mm, "end": v(20.94, 22.67) * mm});
            skLineSegment(sketch, "E1819", {"start": v(20.94, 22.67) * mm, "end": v(20.96, 22.7) * mm});
            skLineSegment(sketch, "E1820", {"start": v(20.96, 22.7) * mm, "end": v(20.98, 22.72) * mm});
            skLineSegment(sketch, "E1821", {"start": v(20.98, 22.72) * mm, "end": v(21, 22.75) * mm});
            skLineSegment(sketch, "E1822", {"start": v(21, 22.75) * mm, "end": v(21.03, 22.79) * mm});
            skLineSegment(sketch, "E1823", {"start": v(21.03, 22.79) * mm, "end": v(21.05, 22.82) * mm});
            skLineSegment(sketch, "E1824", {"start": v(21.05, 22.82) * mm, "end": v(21.08, 22.86) * mm});
            skLineSegment(sketch, "E1825", {"start": v(21.08, 22.86) * mm, "end": v(21.11, 22.9) * mm});
            skLineSegment(sketch, "E1826", {"start": v(21.11, 22.9) * mm, "end": v(21.14, 22.96) * mm});
            skLineSegment(sketch, "E1827", {"start": v(21.14, 22.96) * mm, "end": v(21.18, 23) * mm});
            skLineSegment(sketch, "E1828", {"start": v(21.18, 23) * mm, "end": v(21.21, 23.07) * mm});
            skLineSegment(sketch, "E1829", {"start": v(21.21, 23.07) * mm, "end": v(21.25, 23.13) * mm});
            skLineSegment(sketch, "E1830", {"start": v(21.25, 23.13) * mm, "end": v(21.29, 23.2) * mm});
            skLineSegment(sketch, "E1831", {"start": v(21.29, 23.2) * mm, "end": v(21.33, 23.26) * mm});
            skLineSegment(sketch, "E1832", {"start": v(21.33, 23.26) * mm, "end": v(21.37, 23.33) * mm});
            skLineSegment(sketch, "E1833", {"start": v(21.37, 23.33) * mm, "end": v(21.41, 23.4) * mm});
            skLineSegment(sketch, "E1834", {"start": v(21.41, 23.4) * mm, "end": v(21.45, 23.49) * mm});
            skLineSegment(sketch, "E1835", {"start": v(21.45, 23.49) * mm, "end": v(21.5, 23.57) * mm});
            skLineSegment(sketch, "E1836", {"start": v(21.5, 23.57) * mm, "end": v(21.54, 23.66) * mm});
            skLineSegment(sketch, "E1837", {"start": v(21.54, 23.66) * mm, "end": v(21.59, 23.76) * mm});
            skLineSegment(sketch, "E1838", {"start": v(21.59, 23.76) * mm, "end": v(21.63, 23.86) * mm});
            skLineSegment(sketch, "E1839", {"start": v(21.63, 23.86) * mm, "end": v(21.68, 23.96) * mm});
            skLineSegment(sketch, "E1840", {"start": v(21.68, 23.96) * mm, "end": v(21.73, 24.06) * mm});
            skLineSegment(sketch, "E1841", {"start": v(21.73, 24.06) * mm, "end": v(21.78, 24.18) * mm});
            skLineSegment(sketch, "E1842", {"start": v(21.78, 24.18) * mm, "end": v(21.83, 24.3) * mm});
            skLineSegment(sketch, "E1843", {"start": v(21.83, 24.3) * mm, "end": v(21.87, 24.41) * mm});
            skLineSegment(sketch, "E1844", {"start": v(21.87, 24.41) * mm, "end": v(21.92, 24.53) * mm});
            skLineSegment(sketch, "E1845", {"start": v(21.92, 24.53) * mm, "end": v(21.97, 24.66) * mm});
            skLineSegment(sketch, "E1846", {"start": v(21.97, 24.66) * mm, "end": v(22.02, 24.8) * mm});
            skLineSegment(sketch, "E1847", {"start": v(22.02, 24.8) * mm, "end": v(22.07, 24.93) * mm});
            skLineSegment(sketch, "E1848", {"start": v(22.07, 24.93) * mm, "end": v(22.12, 25.08) * mm});
            skLineSegment(sketch, "E1849", {"start": v(22.12, 25.08) * mm, "end": v(22.16, 25.22) * mm});
            skLineSegment(sketch, "E1850", {"start": v(22.16, 25.22) * mm, "end": v(22.21, 25.37) * mm});
            skLineSegment(sketch, "E1851", {"start": v(22.21, 25.37) * mm, "end": v(22.26, 25.53) * mm});
            skLineSegment(sketch, "E1852", {"start": v(22.26, 25.53) * mm, "end": v(22.3, 25.69) * mm});
            skLineSegment(sketch, "E1853", {"start": v(22.3, 25.69) * mm, "end": v(22.35, 25.85) * mm});
            skLineSegment(sketch, "E1854", {"start": v(22.35, 25.85) * mm, "end": v(22.4, 26.02) * mm});
            skLineSegment(sketch, "E1855", {"start": v(22.4, 26.02) * mm, "end": v(22.44, 26.2) * mm});
            skLineSegment(sketch, "E1856", {"start": v(22.44, 26.2) * mm, "end": v(22.48, 26.37) * mm});
            skLineSegment(sketch, "E1857", {"start": v(22.48, 26.37) * mm, "end": v(22.52, 26.56) * mm});
            skLineSegment(sketch, "E1858", {"start": v(22.52, 26.56) * mm, "end": v(22.52, 26.7) * mm});
            skLineSegment(sketch, "E1859", {"start": v(22.52, 26.7) * mm, "end": v(21.38, 27.63) * mm});
            skLineSegment(sketch, "E1860", {"start": v(21.38, 27.63) * mm, "end": v(21.24, 27.6) * mm});
            skLineSegment(sketch, "E1861", {"start": v(21.24, 27.6) * mm, "end": v(21.07, 27.52) * mm});
            skLineSegment(sketch, "E1862", {"start": v(21.07, 27.52) * mm, "end": v(20.9, 27.44) * mm});
            skLineSegment(sketch, "E1863", {"start": v(20.9, 27.44) * mm, "end": v(20.74, 27.36) * mm});
            skLineSegment(sketch, "E1864", {"start": v(20.74, 27.36) * mm, "end": v(20.59, 27.28) * mm});
            skLineSegment(sketch, "E1865", {"start": v(20.59, 27.28) * mm, "end": v(20.43, 27.2) * mm});
            skLineSegment(sketch, "E1866", {"start": v(20.43, 27.2) * mm, "end": v(20.29, 27.12) * mm});
            skLineSegment(sketch, "E1867", {"start": v(20.29, 27.12) * mm, "end": v(20.14, 27.04) * mm});
            skLineSegment(sketch, "E1868", {"start": v(20.14, 27.04) * mm, "end": v(20, 26.97) * mm});
            skLineSegment(sketch, "E1869", {"start": v(20, 26.97) * mm, "end": v(19.87, 26.89) * mm});
            skLineSegment(sketch, "E1870", {"start": v(19.87, 26.89) * mm, "end": v(19.74, 26.81) * mm});
            skLineSegment(sketch, "E1871", {"start": v(19.74, 26.81) * mm, "end": v(19.62, 26.73) * mm});
            skLineSegment(sketch, "E1872", {"start": v(19.62, 26.73) * mm, "end": v(19.5, 26.66) * mm});
            skLineSegment(sketch, "E1873", {"start": v(19.5, 26.66) * mm, "end": v(19.38, 26.58) * mm});
            skLineSegment(sketch, "E1874", {"start": v(19.38, 26.58) * mm, "end": v(19.27, 26.51) * mm});
            skLineSegment(sketch, "E1875", {"start": v(19.27, 26.51) * mm, "end": v(19.17, 26.44) * mm});
            skLineSegment(sketch, "E1876", {"start": v(19.17, 26.44) * mm, "end": v(19.06, 26.37) * mm});
            skLineSegment(sketch, "E1877", {"start": v(19.06, 26.37) * mm, "end": v(18.97, 26.3) * mm});
            skLineSegment(sketch, "E1878", {"start": v(18.97, 26.3) * mm, "end": v(18.87, 26.23) * mm});
            skLineSegment(sketch, "E1879", {"start": v(18.87, 26.23) * mm, "end": v(18.78, 26.16) * mm});
            skLineSegment(sketch, "E1880", {"start": v(18.78, 26.16) * mm, "end": v(18.7, 26.1) * mm});
            skLineSegment(sketch, "E1881", {"start": v(18.7, 26.1) * mm, "end": v(18.61, 26.03) * mm});
            skLineSegment(sketch, "E1882", {"start": v(18.61, 26.03) * mm, "end": v(18.54, 25.97) * mm});
            skLineSegment(sketch, "E1883", {"start": v(18.54, 25.97) * mm, "end": v(18.46, 25.9) * mm});
            skLineSegment(sketch, "E1884", {"start": v(18.46, 25.9) * mm, "end": v(18.4, 25.85) * mm});
            skLineSegment(sketch, "E1885", {"start": v(18.4, 25.85) * mm, "end": v(18.33, 25.8) * mm});
            skLineSegment(sketch, "E1886", {"start": v(18.33, 25.8) * mm, "end": v(18.26, 25.74) * mm});
            skLineSegment(sketch, "E1887", {"start": v(18.26, 25.74) * mm, "end": v(18.2, 25.68) * mm});
            skLineSegment(sketch, "E1888", {"start": v(18.2, 25.68) * mm, "end": v(18.15, 25.63) * mm});
            skLineSegment(sketch, "E1889", {"start": v(18.15, 25.63) * mm, "end": v(18.1, 25.58) * mm});
            skLineSegment(sketch, "E1890", {"start": v(18.1, 25.58) * mm, "end": v(18.05, 25.54) * mm});
            skLineSegment(sketch, "E1891", {"start": v(18.05, 25.54) * mm, "end": v(18, 25.5) * mm});
            skLineSegment(sketch, "E1892", {"start": v(18, 25.5) * mm, "end": v(17.97, 25.45) * mm});
            skLineSegment(sketch, "E1893", {"start": v(17.97, 25.45) * mm, "end": v(17.93, 25.41) * mm});
            skLineSegment(sketch, "E1894", {"start": v(17.93, 25.41) * mm, "end": v(17.9, 25.37) * mm});
            skLineSegment(sketch, "E1895", {"start": v(17.9, 25.37) * mm, "end": v(17.86, 25.34) * mm});
            skLineSegment(sketch, "E1896", {"start": v(17.86, 25.34) * mm, "end": v(17.84, 25.3) * mm});
            skLineSegment(sketch, "E1897", {"start": v(17.84, 25.3) * mm, "end": v(17.81, 25.28) * mm});
            skLineSegment(sketch, "E1898", {"start": v(17.81, 25.28) * mm, "end": v(17.79, 25.26) * mm});
            skLineSegment(sketch, "E1899", {"start": v(17.79, 25.26) * mm, "end": v(17.77, 25.23) * mm});
            skLineSegment(sketch, "E1900", {"start": v(17.77, 25.23) * mm, "end": v(17.75, 25.21) * mm});
            skLineSegment(sketch, "E1901", {"start": v(17.75, 25.21) * mm, "end": v(17.74, 25.2) * mm});
            skLineSegment(sketch, "E1902", {"start": v(17.74, 25.2) * mm, "end": v(17.73, 25.18) * mm});
            skLineSegment(sketch, "E1903", {"start": v(17.73, 25.18) * mm, "end": v(17.72, 25.17) * mm});
            skLineSegment(sketch, "E1904", {"start": v(17.72, 25.17) * mm, "end": v(17.72, 25.17) * mm});
            skLineSegment(sketch, "E1905", {"start": v(17.72, 25.17) * mm, "end": v(17.4, 24.73) * mm});
            skLineSegment(sketch, "E1906", {"start": v(17.4, 24.73) * mm, "end": v(15.45, 26) * mm});
            skLineSegment(sketch, "E1907", {"start": v(15.45, 26) * mm, "end": v(15.73, 26.46) * mm});
            skLineSegment(sketch, "E1908", {"start": v(15.73, 26.46) * mm, "end": v(15.73, 26.46) * mm});
            skLineSegment(sketch, "E1909", {"start": v(15.73, 26.46) * mm, "end": v(15.74, 26.47) * mm});
            skLineSegment(sketch, "E1910", {"start": v(15.74, 26.47) * mm, "end": v(15.75, 26.49) * mm});
            skLineSegment(sketch, "E1911", {"start": v(15.75, 26.49) * mm, "end": v(15.76, 26.5) * mm});
            skLineSegment(sketch, "E1912", {"start": v(15.76, 26.5) * mm, "end": v(15.77, 26.53) * mm});
            skLineSegment(sketch, "E1913", {"start": v(15.77, 26.53) * mm, "end": v(15.78, 26.56) * mm});
            skLineSegment(sketch, "E1914", {"start": v(15.78, 26.56) * mm, "end": v(15.8, 26.59) * mm});
            skLineSegment(sketch, "E1915", {"start": v(15.8, 26.59) * mm, "end": v(15.81, 26.62) * mm});
            skLineSegment(sketch, "E1916", {"start": v(15.81, 26.62) * mm, "end": v(15.83, 26.66) * mm});
            skLineSegment(sketch, "E1917", {"start": v(15.83, 26.66) * mm, "end": v(15.85, 26.7) * mm});
            skLineSegment(sketch, "E1918", {"start": v(15.85, 26.7) * mm, "end": v(15.87, 26.75) * mm});
            skLineSegment(sketch, "E1919", {"start": v(15.87, 26.75) * mm, "end": v(15.89, 26.8) * mm});
            skLineSegment(sketch, "E1920", {"start": v(15.89, 26.8) * mm, "end": v(15.9, 26.85) * mm});
            skLineSegment(sketch, "E1921", {"start": v(15.9, 26.85) * mm, "end": v(15.93, 26.9) * mm});
            skLineSegment(sketch, "E1922", {"start": v(15.93, 26.9) * mm, "end": v(15.95, 26.97) * mm});
            skLineSegment(sketch, "E1923", {"start": v(15.95, 26.97) * mm, "end": v(15.98, 27.04) * mm});
            skLineSegment(sketch, "E1924", {"start": v(15.98, 27.04) * mm, "end": v(16, 27.11) * mm});
            skLineSegment(sketch, "E1925", {"start": v(16, 27.11) * mm, "end": v(16.03, 27.19) * mm});
            skLineSegment(sketch, "E1926", {"start": v(16.03, 27.19) * mm, "end": v(16.05, 27.26) * mm});
            skLineSegment(sketch, "E1927", {"start": v(16.05, 27.26) * mm, "end": v(16.08, 27.35) * mm});
            skLineSegment(sketch, "E1928", {"start": v(16.08, 27.35) * mm, "end": v(16.1, 27.44) * mm});
            skLineSegment(sketch, "E1929", {"start": v(16.1, 27.44) * mm, "end": v(16.13, 27.53) * mm});
            skLineSegment(sketch, "E1930", {"start": v(16.13, 27.53) * mm, "end": v(16.15, 27.63) * mm});
            skLineSegment(sketch, "E1931", {"start": v(16.15, 27.63) * mm, "end": v(16.18, 27.73) * mm});
            skLineSegment(sketch, "E1932", {"start": v(16.18, 27.73) * mm, "end": v(16.2, 27.83) * mm});
            skLineSegment(sketch, "E1933", {"start": v(16.2, 27.83) * mm, "end": v(16.23, 27.94) * mm});
            skLineSegment(sketch, "E1934", {"start": v(16.23, 27.94) * mm, "end": v(16.25, 28.06) * mm});
            skLineSegment(sketch, "E1935", {"start": v(16.25, 28.06) * mm, "end": v(16.27, 28.17) * mm});
            skLineSegment(sketch, "E1936", {"start": v(16.27, 28.17) * mm, "end": v(16.3, 28.3) * mm});
            skLineSegment(sketch, "E1937", {"start": v(16.3, 28.3) * mm, "end": v(16.32, 28.42) * mm});
            skLineSegment(sketch, "E1938", {"start": v(16.32, 28.42) * mm, "end": v(16.34, 28.56) * mm});
            skLineSegment(sketch, "E1939", {"start": v(16.34, 28.56) * mm, "end": v(16.36, 28.7) * mm});
            skLineSegment(sketch, "E1940", {"start": v(16.36, 28.7) * mm, "end": v(16.38, 28.83) * mm});
            skLineSegment(sketch, "E1941", {"start": v(16.38, 28.83) * mm, "end": v(16.4, 28.98) * mm});
            skLineSegment(sketch, "E1942", {"start": v(16.4, 28.98) * mm, "end": v(16.42, 29.13) * mm});
            skLineSegment(sketch, "E1943", {"start": v(16.42, 29.13) * mm, "end": v(16.44, 29.28) * mm});
            skLineSegment(sketch, "E1944", {"start": v(16.44, 29.28) * mm, "end": v(16.45, 29.44) * mm});
            skLineSegment(sketch, "E1945", {"start": v(16.45, 29.44) * mm, "end": v(16.46, 29.6) * mm});
            skLineSegment(sketch, "E1946", {"start": v(16.46, 29.6) * mm, "end": v(16.48, 29.76) * mm});
            skLineSegment(sketch, "E1947", {"start": v(16.48, 29.76) * mm, "end": v(16.49, 29.94) * mm});
            skLineSegment(sketch, "E1948", {"start": v(16.49, 29.94) * mm, "end": v(16.5, 30.11) * mm});
            skLineSegment(sketch, "E1949", {"start": v(16.5, 30.11) * mm, "end": v(16.5, 30.29) * mm});
            skLineSegment(sketch, "E1950", {"start": v(16.5, 30.29) * mm, "end": v(16.5, 30.47) * mm});
            skLineSegment(sketch, "E1951", {"start": v(16.5, 30.47) * mm, "end": v(16.5, 30.66) * mm});
            skLineSegment(sketch, "E1952", {"start": v(16.5, 30.66) * mm, "end": v(16.48, 30.8) * mm});
            skLineSegment(sketch, "E1953", {"start": v(16.48, 30.8) * mm, "end": v(15.17, 31.47) * mm});
            skLineSegment(sketch, "E1954", {"start": v(15.17, 31.47) * mm, "end": v(15.04, 31.4) * mm});
            skLineSegment(sketch, "E1955", {"start": v(15.04, 31.4) * mm, "end": v(14.89, 31.3) * mm});
            skLineSegment(sketch, "E1956", {"start": v(14.89, 31.3) * mm, "end": v(14.74, 31.18) * mm});
            skLineSegment(sketch, "E1957", {"start": v(14.74, 31.18) * mm, "end": v(14.6, 31.07) * mm});
            skLineSegment(sketch, "E1958", {"start": v(14.6, 31.07) * mm, "end": v(14.46, 30.96) * mm});
            skLineSegment(sketch, "E1959", {"start": v(14.46, 30.96) * mm, "end": v(14.33, 30.85) * mm});
            skLineSegment(sketch, "E1960", {"start": v(14.33, 30.85) * mm, "end": v(14.2, 30.75) * mm});
            skLineSegment(sketch, "E1961", {"start": v(14.2, 30.75) * mm, "end": v(14.08, 30.64) * mm});
            skLineSegment(sketch, "E1962", {"start": v(14.08, 30.64) * mm, "end": v(13.96, 30.54) * mm});
            skLineSegment(sketch, "E1963", {"start": v(13.96, 30.54) * mm, "end": v(13.85, 30.43) * mm});
            skLineSegment(sketch, "E1964", {"start": v(13.85, 30.43) * mm, "end": v(13.74, 30.33) * mm});
            skLineSegment(sketch, "E1965", {"start": v(13.74, 30.33) * mm, "end": v(13.63, 30.23) * mm});
            skLineSegment(sketch, "E1966", {"start": v(13.63, 30.23) * mm, "end": v(13.53, 30.13) * mm});
            skLineSegment(sketch, "E1967", {"start": v(13.53, 30.13) * mm, "end": v(13.43, 30.03) * mm});
            skLineSegment(sketch, "E1968", {"start": v(13.43, 30.03) * mm, "end": v(13.34, 29.94) * mm});
            skLineSegment(sketch, "E1969", {"start": v(13.34, 29.94) * mm, "end": v(13.25, 29.85) * mm});
            skLineSegment(sketch, "E1970", {"start": v(13.25, 29.85) * mm, "end": v(13.17, 29.75) * mm});
            skLineSegment(sketch, "E1971", {"start": v(13.17, 29.75) * mm, "end": v(13.08, 29.67) * mm});
            skLineSegment(sketch, "E1972", {"start": v(13.08, 29.67) * mm, "end": v(13, 29.58) * mm});
            skLineSegment(sketch, "E1973", {"start": v(13, 29.58) * mm, "end": v(12.93, 29.5) * mm});
            skLineSegment(sketch, "E1974", {"start": v(12.93, 29.5) * mm, "end": v(12.86, 29.41) * mm});
            skLineSegment(sketch, "E1975", {"start": v(12.86, 29.41) * mm, "end": v(12.8, 29.33) * mm});
            skLineSegment(sketch, "E1976", {"start": v(12.8, 29.33) * mm, "end": v(12.73, 29.25) * mm});
            skLineSegment(sketch, "E1977", {"start": v(12.73, 29.25) * mm, "end": v(12.67, 29.18) * mm});
            skLineSegment(sketch, "E1978", {"start": v(12.67, 29.18) * mm, "end": v(12.62, 29.1) * mm});
            skLineSegment(sketch, "E1979", {"start": v(12.62, 29.1) * mm, "end": v(12.56, 29.04) * mm});
            skLineSegment(sketch, "E1980", {"start": v(12.56, 29.04) * mm, "end": v(12.51, 28.97) * mm});
            skLineSegment(sketch, "E1981", {"start": v(12.51, 28.97) * mm, "end": v(12.47, 28.9) * mm});
            skLineSegment(sketch, "E1982", {"start": v(12.47, 28.9) * mm, "end": v(12.42, 28.84) * mm});
            skLineSegment(sketch, "E1983", {"start": v(12.42, 28.84) * mm, "end": v(12.38, 28.79) * mm});
            skLineSegment(sketch, "E1984", {"start": v(12.38, 28.79) * mm, "end": v(12.35, 28.73) * mm});
            skLineSegment(sketch, "E1985", {"start": v(12.35, 28.73) * mm, "end": v(12.31, 28.68) * mm});
            skLineSegment(sketch, "E1986", {"start": v(12.31, 28.68) * mm, "end": v(12.28, 28.63) * mm});
            skLineSegment(sketch, "E1987", {"start": v(12.28, 28.63) * mm, "end": v(12.25, 28.58) * mm});
            skLineSegment(sketch, "E1988", {"start": v(12.25, 28.58) * mm, "end": v(12.23, 28.54) * mm});
            skLineSegment(sketch, "E1989", {"start": v(12.23, 28.54) * mm, "end": v(12.2, 28.5) * mm});
            skLineSegment(sketch, "E1990", {"start": v(12.2, 28.5) * mm, "end": v(12.18, 28.46) * mm});
            skLineSegment(sketch, "E1991", {"start": v(12.18, 28.46) * mm, "end": v(12.17, 28.43) * mm});
            skLineSegment(sketch, "E1992", {"start": v(12.17, 28.43) * mm, "end": v(12.15, 28.4) * mm});
            skLineSegment(sketch, "E1993", {"start": v(12.15, 28.4) * mm, "end": v(12.14, 28.38) * mm});
            skLineSegment(sketch, "E1994", {"start": v(12.14, 28.38) * mm, "end": v(12.12, 28.35) * mm});
            skLineSegment(sketch, "E1995", {"start": v(12.12, 28.35) * mm, "end": v(12.11, 28.34) * mm});
            skLineSegment(sketch, "E1996", {"start": v(12.11, 28.34) * mm, "end": v(12.1, 28.32) * mm});
            skLineSegment(sketch, "E1997", {"start": v(12.1, 28.32) * mm, "end": v(12.1, 28.3) * mm});
            skLineSegment(sketch, "E1998", {"start": v(12.1, 28.3) * mm, "end": v(12.1, 28.3) * mm});
            skLineSegment(sketch, "E1999", {"start": v(12.1, 28.3) * mm, "end": v(11.89, 27.8) * mm});
            skLineSegment(sketch, "E2000", {"start": v(11.89, 27.8) * mm, "end": v(9.71, 28.64) * mm});
            skLineSegment(sketch, "E2001", {"start": v(9.71, 28.64) * mm, "end": v(9.89, 29.15) * mm});
            skLineSegment(sketch, "E2002", {"start": v(9.89, 29.15) * mm, "end": v(9.89, 29.16) * mm});
            skLineSegment(sketch, "E2003", {"start": v(9.89, 29.16) * mm, "end": v(9.9, 29.17) * mm});
            skLineSegment(sketch, "E2004", {"start": v(9.9, 29.17) * mm, "end": v(9.9, 29.18) * mm});
            skLineSegment(sketch, "E2005", {"start": v(9.9, 29.18) * mm, "end": v(9.9, 29.2) * mm});
            skLineSegment(sketch, "E2006", {"start": v(9.9, 29.2) * mm, "end": v(9.9, 29.23) * mm});
            skLineSegment(sketch, "E2007", {"start": v(9.9, 29.23) * mm, "end": v(9.92, 29.26) * mm});
            skLineSegment(sketch, "E2008", {"start": v(9.92, 29.26) * mm, "end": v(9.92, 29.29) * mm});
            skLineSegment(sketch, "E2009", {"start": v(9.92, 29.29) * mm, "end": v(9.93, 29.33) * mm});
            skLineSegment(sketch, "E2010", {"start": v(9.93, 29.33) * mm, "end": v(9.94, 29.37) * mm});
            skLineSegment(sketch, "E2011", {"start": v(9.94, 29.37) * mm, "end": v(9.95, 29.41) * mm});
            skLineSegment(sketch, "E2012", {"start": v(9.95, 29.41) * mm, "end": v(9.96, 29.46) * mm});
            skLineSegment(sketch, "E2013", {"start": v(9.96, 29.46) * mm, "end": v(9.97, 29.51) * mm});
            skLineSegment(sketch, "E2014", {"start": v(9.97, 29.51) * mm, "end": v(9.98, 29.57) * mm});
            skLineSegment(sketch, "E2015", {"start": v(9.98, 29.57) * mm, "end": v(9.99, 29.63) * mm});
            skLineSegment(sketch, "E2016", {"start": v(9.99, 29.63) * mm, "end": v(10, 29.7) * mm});
            skLineSegment(sketch, "E2017", {"start": v(10, 29.7) * mm, "end": v(10, 29.77) * mm});
            skLineSegment(sketch, "E2018", {"start": v(10, 29.77) * mm, "end": v(10.01, 29.84) * mm});
            skLineSegment(sketch, "E2019", {"start": v(10.01, 29.84) * mm, "end": v(10.02, 29.92) * mm});
            skLineSegment(sketch, "E2020", {"start": v(10.02, 29.92) * mm, "end": v(10.03, 30) * mm});
            skLineSegment(sketch, "E2021", {"start": v(10.03, 30) * mm, "end": v(10.04, 30.1) * mm});
            skLineSegment(sketch, "E2022", {"start": v(10.04, 30.1) * mm, "end": v(10.04, 30.18) * mm});
            skLineSegment(sketch, "E2023", {"start": v(10.04, 30.18) * mm, "end": v(10.05, 30.28) * mm});
            skLineSegment(sketch, "E2024", {"start": v(10.05, 30.28) * mm, "end": v(10.05, 30.38) * mm});
            skLineSegment(sketch, "E2025", {"start": v(10.05, 30.38) * mm, "end": v(10.06, 30.48) * mm});
            skLineSegment(sketch, "E2026", {"start": v(10.06, 30.48) * mm, "end": v(10.06, 30.6) * mm});
            skLineSegment(sketch, "E2027", {"start": v(10.06, 30.6) * mm, "end": v(10.06, 30.7) * mm});
            skLineSegment(sketch, "E2028", {"start": v(10.06, 30.7) * mm, "end": v(10.06, 30.82) * mm});
            skLineSegment(sketch, "E2029", {"start": v(10.06, 30.82) * mm, "end": v(10.06, 30.94) * mm});
            skLineSegment(sketch, "E2030", {"start": v(10.06, 30.94) * mm, "end": v(10.06, 31.07) * mm});
            skLineSegment(sketch, "E2031", {"start": v(10.06, 31.07) * mm, "end": v(10.05, 31.2) * mm});
            skLineSegment(sketch, "E2032", {"start": v(10.05, 31.2) * mm, "end": v(10.05, 31.33) * mm});
            skLineSegment(sketch, "E2033", {"start": v(10.05, 31.33) * mm, "end": v(10.04, 31.47) * mm});
            skLineSegment(sketch, "E2034", {"start": v(10.04, 31.47) * mm, "end": v(10.03, 31.6) * mm});
            skLineSegment(sketch, "E2035", {"start": v(10.03, 31.6) * mm, "end": v(10.02, 31.75) * mm});
            skLineSegment(sketch, "E2036", {"start": v(10.02, 31.75) * mm, "end": v(10, 31.9) * mm});
            skLineSegment(sketch, "E2037", {"start": v(10, 31.9) * mm, "end": v(9.99, 32.06) * mm});
            skLineSegment(sketch, "E2038", {"start": v(9.99, 32.06) * mm, "end": v(9.97, 32.21) * mm});
            skLineSegment(sketch, "E2039", {"start": v(9.97, 32.21) * mm, "end": v(9.95, 32.38) * mm});
            skLineSegment(sketch, "E2040", {"start": v(9.95, 32.38) * mm, "end": v(9.93, 32.54) * mm});
            skLineSegment(sketch, "E2041", {"start": v(9.93, 32.54) * mm, "end": v(9.9, 32.7) * mm});
            skLineSegment(sketch, "E2042", {"start": v(9.9, 32.7) * mm, "end": v(9.87, 32.88) * mm});
            skLineSegment(sketch, "E2043", {"start": v(9.87, 32.88) * mm, "end": v(9.84, 33.06) * mm});
            skLineSegment(sketch, "E2044", {"start": v(9.84, 33.06) * mm, "end": v(9.8, 33.24) * mm});
            skLineSegment(sketch, "E2045", {"start": v(9.8, 33.24) * mm, "end": v(9.77, 33.42) * mm});
            skLineSegment(sketch, "E2046", {"start": v(9.77, 33.42) * mm, "end": v(9.72, 33.55) * mm});
            skLineSegment(sketch, "E2047", {"start": v(9.72, 33.55) * mm, "end": v(8.3, 33.94) * mm});
            skLineSegment(sketch, "E2048", {"start": v(8.3, 33.94) * mm, "end": v(8.18, 33.85) * mm});
            skLineSegment(sketch, "E2049", {"start": v(8.18, 33.85) * mm, "end": v(8.05, 33.7) * mm});
            skLineSegment(sketch, "E2050", {"start": v(8.05, 33.7) * mm, "end": v(7.93, 33.57) * mm});
            skLineSegment(sketch, "E2051", {"start": v(7.93, 33.57) * mm, "end": v(7.82, 33.43) * mm});
            skLineSegment(sketch, "E2052", {"start": v(7.82, 33.43) * mm, "end": v(7.7, 33.3) * mm});
            skLineSegment(sketch, "E2053", {"start": v(7.7, 33.3) * mm, "end": v(7.6, 33.16) * mm});
            skLineSegment(sketch, "E2054", {"start": v(7.6, 33.16) * mm, "end": v(7.5, 33.03) * mm});
            skLineSegment(sketch, "E2055", {"start": v(7.5, 33.03) * mm, "end": v(7.4, 32.9) * mm});
            skLineSegment(sketch, "E2056", {"start": v(7.4, 32.9) * mm, "end": v(7.3, 32.77) * mm});
            skLineSegment(sketch, "E2057", {"start": v(7.3, 32.77) * mm, "end": v(7.22, 32.65) * mm});
            skLineSegment(sketch, "E2058", {"start": v(7.22, 32.65) * mm, "end": v(7.13, 32.52) * mm});
            skLineSegment(sketch, "E2059", {"start": v(7.13, 32.52) * mm, "end": v(7.05, 32.4) * mm});
            skLineSegment(sketch, "E2060", {"start": v(7.05, 32.4) * mm, "end": v(6.97, 32.29) * mm});
            skLineSegment(sketch, "E2061", {"start": v(6.97, 32.29) * mm, "end": v(6.9, 32.17) * mm});
            skLineSegment(sketch, "E2062", {"start": v(6.9, 32.17) * mm, "end": v(6.82, 32.06) * mm});
            skLineSegment(sketch, "E2063", {"start": v(6.82, 32.06) * mm, "end": v(6.76, 31.95) * mm});
            skLineSegment(sketch, "E2064", {"start": v(6.76, 31.95) * mm, "end": v(6.7, 31.84) * mm});
            skLineSegment(sketch, "E2065", {"start": v(6.7, 31.84) * mm, "end": v(6.63, 31.74) * mm});
            skLineSegment(sketch, "E2066", {"start": v(6.63, 31.74) * mm, "end": v(6.57, 31.64) * mm});
            skLineSegment(sketch, "E2067", {"start": v(6.57, 31.64) * mm, "end": v(6.52, 31.54) * mm});
            skLineSegment(sketch, "E2068", {"start": v(6.52, 31.54) * mm, "end": v(6.47, 31.44) * mm});
            skLineSegment(sketch, "E2069", {"start": v(6.47, 31.44) * mm, "end": v(6.42, 31.35) * mm});
            skLineSegment(sketch, "E2070", {"start": v(6.42, 31.35) * mm, "end": v(6.37, 31.26) * mm});
            skLineSegment(sketch, "E2071", {"start": v(6.37, 31.26) * mm, "end": v(6.33, 31.18) * mm});
            skLineSegment(sketch, "E2072", {"start": v(6.33, 31.18) * mm, "end": v(6.29, 31.1) * mm});
            skLineSegment(sketch, "E2073", {"start": v(6.29, 31.1) * mm, "end": v(6.25, 31.01) * mm});
            skLineSegment(sketch, "E2074", {"start": v(6.25, 31.01) * mm, "end": v(6.22, 30.94) * mm});
            skLineSegment(sketch, "E2075", {"start": v(6.22, 30.94) * mm, "end": v(6.19, 30.87) * mm});
            skLineSegment(sketch, "E2076", {"start": v(6.19, 30.87) * mm, "end": v(6.16, 30.8) * mm});
            skLineSegment(sketch, "E2077", {"start": v(6.16, 30.8) * mm, "end": v(6.13, 30.73) * mm});
            skLineSegment(sketch, "E2078", {"start": v(6.13, 30.73) * mm, "end": v(6.1, 30.67) * mm});
            skLineSegment(sketch, "E2079", {"start": v(6.1, 30.67) * mm, "end": v(6.08, 30.61) * mm});
            skLineSegment(sketch, "E2080", {"start": v(6.08, 30.61) * mm, "end": v(6.06, 30.56) * mm});
            skLineSegment(sketch, "E2081", {"start": v(6.06, 30.56) * mm, "end": v(6.04, 30.5) * mm});
            skLineSegment(sketch, "E2082", {"start": v(6.04, 30.5) * mm, "end": v(6.03, 30.46) * mm});
            skLineSegment(sketch, "E2083", {"start": v(6.03, 30.46) * mm, "end": v(6.01, 30.42) * mm});
            skLineSegment(sketch, "E2084", {"start": v(6.01, 30.42) * mm, "end": v(6, 30.38) * mm});
            skLineSegment(sketch, "E2085", {"start": v(6, 30.38) * mm, "end": v(5.99, 30.34) * mm});
            skLineSegment(sketch, "E2086", {"start": v(5.99, 30.34) * mm, "end": v(5.98, 30.3) * mm});
            skLineSegment(sketch, "E2087", {"start": v(5.98, 30.3) * mm, "end": v(5.97, 30.28) * mm});
            skLineSegment(sketch, "E2088", {"start": v(5.97, 30.28) * mm, "end": v(5.96, 30.26) * mm});
            skLineSegment(sketch, "E2089", {"start": v(5.96, 30.26) * mm, "end": v(5.96, 30.24) * mm});
            skLineSegment(sketch, "E2090", {"start": v(5.96, 30.24) * mm, "end": v(5.95, 30.22) * mm});
            skLineSegment(sketch, "E2091", {"start": v(5.95, 30.22) * mm, "end": v(5.95, 30.2) * mm});
            skLineSegment(sketch, "E2092", {"start": v(5.95, 30.2) * mm, "end": v(5.95, 30.2) * mm});
            skLineSegment(sketch, "E2093", {"start": v(5.95, 30.2) * mm, "end": v(5.85, 29.67) * mm});
            skLineSegment(sketch, "E2094", {"start": v(5.85, 29.67) * mm, "end": v(3.55, 30.03) * mm});
            skLineSegment(sketch, "E2095", {"start": v(3.55, 30.03) * mm, "end": v(3.6, 30.57) * mm});
            skLineSegment(sketch, "E2096", {"start": v(3.6, 30.57) * mm, "end": v(3.61, 30.58) * mm});
            skLineSegment(sketch, "E2097", {"start": v(3.61, 30.58) * mm, "end": v(3.61, 30.59) * mm});
            skLineSegment(sketch, "E2098", {"start": v(3.61, 30.59) * mm, "end": v(3.61, 30.6) * mm});
            skLineSegment(sketch, "E2099", {"start": v(3.61, 30.6) * mm, "end": v(3.61, 30.63) * mm});
            skLineSegment(sketch, "E2100", {"start": v(3.61, 30.63) * mm, "end": v(3.61, 30.65) * mm});
            skLineSegment(sketch, "E2101", {"start": v(3.61, 30.65) * mm, "end": v(3.62, 30.68) * mm});
            skLineSegment(sketch, "E2102", {"start": v(3.62, 30.68) * mm, "end": v(3.62, 30.71) * mm});
            skLineSegment(sketch, "E2103", {"start": v(3.62, 30.71) * mm, "end": v(3.62, 30.75) * mm});
            skLineSegment(sketch, "E2104", {"start": v(3.62, 30.75) * mm, "end": v(3.62, 30.8) * mm});
            skLineSegment(sketch, "E2105", {"start": v(3.62, 30.8) * mm, "end": v(3.62, 30.84) * mm});
            skLineSegment(sketch, "E2106", {"start": v(3.62, 30.84) * mm, "end": v(3.62, 30.89) * mm});
            skLineSegment(sketch, "E2107", {"start": v(3.62, 30.89) * mm, "end": v(3.61, 30.94) * mm});
            skLineSegment(sketch, "E2108", {"start": v(3.61, 30.94) * mm, "end": v(3.61, 31) * mm});
            skLineSegment(sketch, "E2109", {"start": v(3.61, 31) * mm, "end": v(3.6, 31.06) * mm});
            skLineSegment(sketch, "E2110", {"start": v(3.6, 31.06) * mm, "end": v(3.6, 31.13) * mm});
            skLineSegment(sketch, "E2111", {"start": v(3.6, 31.13) * mm, "end": v(3.6, 31.2) * mm});
            skLineSegment(sketch, "E2112", {"start": v(3.6, 31.2) * mm, "end": v(3.6, 31.27) * mm});
            skLineSegment(sketch, "E2113", {"start": v(3.6, 31.27) * mm, "end": v(3.58, 31.35) * mm});
            skLineSegment(sketch, "E2114", {"start": v(3.58, 31.35) * mm, "end": v(3.57, 31.44) * mm});
            skLineSegment(sketch, "E2115", {"start": v(3.57, 31.44) * mm, "end": v(3.56, 31.52) * mm});
            skLineSegment(sketch, "E2116", {"start": v(3.56, 31.52) * mm, "end": v(3.55, 31.61) * mm});
            skLineSegment(sketch, "E2117", {"start": v(3.55, 31.61) * mm, "end": v(3.53, 31.7) * mm});
            skLineSegment(sketch, "E2118", {"start": v(3.53, 31.7) * mm, "end": v(3.52, 31.8) * mm});
            skLineSegment(sketch, "E2119", {"start": v(3.52, 31.8) * mm, "end": v(3.5, 31.9) * mm});
            skLineSegment(sketch, "E2120", {"start": v(3.5, 31.9) * mm, "end": v(3.48, 32.02) * mm});
            skLineSegment(sketch, "E2121", {"start": v(3.48, 32.02) * mm, "end": v(3.46, 32.13) * mm});
            skLineSegment(sketch, "E2122", {"start": v(3.46, 32.13) * mm, "end": v(3.43, 32.24) * mm});
            skLineSegment(sketch, "E2123", {"start": v(3.43, 32.24) * mm, "end": v(3.4, 32.36) * mm});
            skLineSegment(sketch, "E2124", {"start": v(3.4, 32.36) * mm, "end": v(3.38, 32.48) * mm});
            skLineSegment(sketch, "E2125", {"start": v(3.38, 32.48) * mm, "end": v(3.35, 32.6) * mm});
            skLineSegment(sketch, "E2126", {"start": v(3.35, 32.6) * mm, "end": v(3.31, 32.73) * mm});
            skLineSegment(sketch, "E2127", {"start": v(3.31, 32.73) * mm, "end": v(3.28, 32.87) * mm});
            skLineSegment(sketch, "E2128", {"start": v(3.28, 32.87) * mm, "end": v(3.24, 33) * mm});
            skLineSegment(sketch, "E2129", {"start": v(3.24, 33) * mm, "end": v(3.2, 33.14) * mm});
            skLineSegment(sketch, "E2130", {"start": v(3.2, 33.14) * mm, "end": v(3.15, 33.29) * mm});
            skLineSegment(sketch, "E2131", {"start": v(3.15, 33.29) * mm, "end": v(3.1, 33.43) * mm});
            skLineSegment(sketch, "E2132", {"start": v(3.1, 33.43) * mm, "end": v(3.06, 33.58) * mm});
            skLineSegment(sketch, "E2133", {"start": v(3.06, 33.58) * mm, "end": v(3, 33.74) * mm});
            skLineSegment(sketch, "E2134", {"start": v(3, 33.74) * mm, "end": v(2.95, 33.9) * mm});
            skLineSegment(sketch, "E2135", {"start": v(2.95, 33.9) * mm, "end": v(2.89, 34.05) * mm});
            skLineSegment(sketch, "E2136", {"start": v(2.89, 34.05) * mm, "end": v(2.82, 34.22) * mm});
            skLineSegment(sketch, "E2137", {"start": v(2.82, 34.22) * mm, "end": v(2.75, 34.38) * mm});
            skLineSegment(sketch, "E2138", {"start": v(2.75, 34.38) * mm, "end": v(2.68, 34.55) * mm});
            skLineSegment(sketch, "E2139", {"start": v(2.68, 34.55) * mm, "end": v(2.61, 34.72) * mm});
            skLineSegment(sketch, "E2140", {"start": v(2.61, 34.72) * mm, "end": v(2.53, 34.84) * mm});
            skLineSegment(sketch, "E2141", {"start": v(2.53, 34.84) * mm, "end": v(1.05, 34.92) * mm});
            skLineSegment(sketch, "E2142", {"start": v(1.05, 34.92) * mm, "end": v(0.96, 34.8) * mm});
            skLineSegment(sketch, "E2143", {"start": v(0.96, 34.8) * mm, "end": v(0.87, 34.64) * mm});
            skLineSegment(sketch, "E2144", {"start": v(0.87, 34.64) * mm, "end": v(0.78, 34.48) * mm});
            skLineSegment(sketch, "E2145", {"start": v(0.78, 34.48) * mm, "end": v(0.7, 34.33) * mm});
            skLineSegment(sketch, "E2146", {"start": v(0.7, 34.33) * mm, "end": v(0.62, 34.17) * mm});
            skLineSegment(sketch, "E2147", {"start": v(0.62, 34.17) * mm, "end": v(0.54, 34.02) * mm});
            skLineSegment(sketch, "E2148", {"start": v(0.54, 34.02) * mm, "end": v(0.47, 33.87) * mm});
            skLineSegment(sketch, "E2149", {"start": v(0.47, 33.87) * mm, "end": v(0.4, 33.72) * mm});
            skLineSegment(sketch, "E2150", {"start": v(0.4, 33.72) * mm, "end": v(0.34, 33.58) * mm});
            skLineSegment(sketch, "E2151", {"start": v(0.34, 33.58) * mm, "end": v(0.27, 33.43) * mm});
            skLineSegment(sketch, "E2152", {"start": v(0.27, 33.43) * mm, "end": v(0.21, 33.3) * mm});
            skLineSegment(sketch, "E2153", {"start": v(0.21, 33.3) * mm, "end": v(0.16, 33.16) * mm});
            skLineSegment(sketch, "E2154", {"start": v(0.16, 33.16) * mm, "end": v(0.1, 33.03) * mm});
            skLineSegment(sketch, "E2155", {"start": v(0.1, 33.03) * mm, "end": v(0.06, 32.9) * mm});
            skLineSegment(sketch, "E2156", {"start": v(0.06, 32.9) * mm, "end": v(0, 32.78) * mm});
            skLineSegment(sketch, "E2157", {"start": v(0, 32.78) * mm, "end": v(-0.03, 32.66) * mm});
            skLineSegment(sketch, "E2158", {"start": v(-0.03, 32.66) * mm, "end": v(-0.07, 32.54) * mm});
            skLineSegment(sketch, "E2159", {"start": v(-0.07, 32.54) * mm, "end": v(-0.11, 32.42) * mm});
            skLineSegment(sketch, "E2160", {"start": v(-0.11, 32.42) * mm, "end": v(-0.15, 32.31) * mm});
            skLineSegment(sketch, "E2161", {"start": v(-0.15, 32.31) * mm, "end": v(-0.18, 32.2) * mm});
            skLineSegment(sketch, "E2162", {"start": v(-0.18, 32.2) * mm, "end": v(-0.21, 32.1) * mm});
            skLineSegment(sketch, "E2163", {"start": v(-0.21, 32.1) * mm, "end": v(-0.24, 32) * mm});
            skLineSegment(sketch, "E2164", {"start": v(-0.24, 32) * mm, "end": v(-0.27, 31.9) * mm});
            skLineSegment(sketch, "E2165", {"start": v(-0.27, 31.9) * mm, "end": v(-0.3, 31.81) * mm});
            skLineSegment(sketch, "E2166", {"start": v(-0.3, 31.81) * mm, "end": v(-0.31, 31.72) * mm});
            skLineSegment(sketch, "E2167", {"start": v(-0.31, 31.72) * mm, "end": v(-0.33, 31.64) * mm});
            skLineSegment(sketch, "E2168", {"start": v(-0.33, 31.64) * mm, "end": v(-0.35, 31.56) * mm});
            skLineSegment(sketch, "E2169", {"start": v(-0.35, 31.56) * mm, "end": v(-0.37, 31.48) * mm});
            skLineSegment(sketch, "E2170", {"start": v(-0.37, 31.48) * mm, "end": v(-0.38, 31.4) * mm});
            skLineSegment(sketch, "E2171", {"start": v(-0.38, 31.4) * mm, "end": v(-0.4, 31.33) * mm});
            skLineSegment(sketch, "E2172", {"start": v(-0.4, 31.33) * mm, "end": v(-0.4, 31.27) * mm});
            skLineSegment(sketch, "E2173", {"start": v(-0.4, 31.27) * mm, "end": v(-0.42, 31.2) * mm});
            skLineSegment(sketch, "E2174", {"start": v(-0.42, 31.2) * mm, "end": v(-0.42, 31.15) * mm});
            skLineSegment(sketch, "E2175", {"start": v(-0.42, 31.15) * mm, "end": v(-0.43, 31.1) * mm});
            skLineSegment(sketch, "E2176", {"start": v(-0.43, 31.1) * mm, "end": v(-0.44, 31.05) * mm});
            skLineSegment(sketch, "E2177", {"start": v(-0.44, 31.05) * mm, "end": v(-0.44, 31) * mm});
            skLineSegment(sketch, "E2178", {"start": v(-0.44, 31) * mm, "end": v(-0.45, 30.96) * mm});
            skLineSegment(sketch, "E2179", {"start": v(-0.45, 30.96) * mm, "end": v(-0.45, 30.92) * mm});
            skLineSegment(sketch, "E2180", {"start": v(-0.45, 30.92) * mm, "end": v(-0.45, 30.89) * mm});
            skLineSegment(sketch, "E2181", {"start": v(-0.45, 30.89) * mm, "end": v(-0.46, 30.86) * mm});
            skLineSegment(sketch, "E2182", {"start": v(-0.46, 30.86) * mm, "end": v(-0.46, 30.83) * mm});
            skLineSegment(sketch, "E2183", {"start": v(-0.46, 30.83) * mm, "end": v(-0.46, 30.81) * mm});
            skLineSegment(sketch, "E2184", {"start": v(-0.46, 30.81) * mm, "end": v(-0.46, 30.8) * mm});
            skLineSegment(sketch, "E2185", {"start": v(-0.46, 30.8) * mm, "end": v(-0.46, 30.78) * mm});
            skLineSegment(sketch, "E2186", {"start": v(-0.46, 30.78) * mm, "end": v(-0.46, 30.78) * mm});
            skLineSegment(sketch, "E2187", {"start": v(-0.46, 30.78) * mm, "end": v(-0.45, 30.24) * mm});
            skLineSegment(sketch, "E2188", {"start": v(-0.45, 30.24) * mm, "end": v(-2.77, 30.11) * mm});
            skLineSegment(sketch, "E2189", {"start": v(-2.77, 30.11) * mm, "end": v(-2.82, 30.65) * mm});
            skLineSegment(sketch, "E2190", {"start": v(-2.82, 30.65) * mm, "end": v(-2.83, 30.66) * mm});
            skLineSegment(sketch, "E2191", {"start": v(-2.83, 30.66) * mm, "end": v(-2.83, 30.67) * mm});
            skLineSegment(sketch, "E2192", {"start": v(-2.83, 30.67) * mm, "end": v(-2.83, 30.69) * mm});
            skLineSegment(sketch, "E2193", {"start": v(-2.83, 30.69) * mm, "end": v(-2.83, 30.7) * mm});
            skLineSegment(sketch, "E2194", {"start": v(-2.83, 30.7) * mm, "end": v(-2.84, 30.73) * mm});
            skLineSegment(sketch, "E2195", {"start": v(-2.84, 30.73) * mm, "end": v(-2.84, 30.76) * mm});
            skLineSegment(sketch, "E2196", {"start": v(-2.84, 30.76) * mm, "end": v(-2.85, 30.8) * mm});
            skLineSegment(sketch, "E2197", {"start": v(-2.85, 30.8) * mm, "end": v(-2.86, 30.83) * mm});
            skLineSegment(sketch, "E2198", {"start": v(-2.86, 30.83) * mm, "end": v(-2.86, 30.87) * mm});
            skLineSegment(sketch, "E2199", {"start": v(-2.86, 30.87) * mm, "end": v(-2.87, 30.92) * mm});
            skLineSegment(sketch, "E2200", {"start": v(-2.87, 30.92) * mm, "end": v(-2.89, 30.96) * mm});
            skLineSegment(sketch, "E2201", {"start": v(-2.89, 30.96) * mm, "end": v(-2.9, 31.02) * mm});
            skLineSegment(sketch, "E2202", {"start": v(-2.9, 31.02) * mm, "end": v(-2.91, 31.07) * mm});
            skLineSegment(sketch, "E2203", {"start": v(-2.91, 31.07) * mm, "end": v(-2.93, 31.13) * mm});
            skLineSegment(sketch, "E2204", {"start": v(-2.93, 31.13) * mm, "end": v(-2.95, 31.2) * mm});
            skLineSegment(sketch, "E2205", {"start": v(-2.95, 31.2) * mm, "end": v(-2.97, 31.27) * mm});
            skLineSegment(sketch, "E2206", {"start": v(-2.97, 31.27) * mm, "end": v(-3, 31.34) * mm});
            skLineSegment(sketch, "E2207", {"start": v(-3, 31.34) * mm, "end": v(-3.01, 31.41) * mm});
            skLineSegment(sketch, "E2208", {"start": v(-3.01, 31.41) * mm, "end": v(-3.04, 31.5) * mm});
            skLineSegment(sketch, "E2209", {"start": v(-3.04, 31.5) * mm, "end": v(-3.07, 31.57) * mm});
            skLineSegment(sketch, "E2210", {"start": v(-3.07, 31.57) * mm, "end": v(-3.1, 31.66) * mm});
            skLineSegment(sketch, "E2211", {"start": v(-3.1, 31.66) * mm, "end": v(-3.13, 31.75) * mm});
            skLineSegment(sketch, "E2212", {"start": v(-3.13, 31.75) * mm, "end": v(-3.17, 31.84) * mm});
            skLineSegment(sketch, "E2213", {"start": v(-3.17, 31.84) * mm, "end": v(-3.21, 31.94) * mm});
            skLineSegment(sketch, "E2214", {"start": v(-3.21, 31.94) * mm, "end": v(-3.25, 32.04) * mm});
            skLineSegment(sketch, "E2215", {"start": v(-3.25, 32.04) * mm, "end": v(-3.3, 32.14) * mm});
            skLineSegment(sketch, "E2216", {"start": v(-3.3, 32.14) * mm, "end": v(-3.34, 32.25) * mm});
            skLineSegment(sketch, "E2217", {"start": v(-3.34, 32.25) * mm, "end": v(-3.4, 32.36) * mm});
            skLineSegment(sketch, "E2218", {"start": v(-3.4, 32.36) * mm, "end": v(-3.45, 32.47) * mm});
            skLineSegment(sketch, "E2219", {"start": v(-3.45, 32.47) * mm, "end": v(-3.5, 32.59) * mm});
            skLineSegment(sketch, "E2220", {"start": v(-3.5, 32.59) * mm, "end": v(-3.56, 32.7) * mm});
            skLineSegment(sketch, "E2221", {"start": v(-3.56, 32.7) * mm, "end": v(-3.63, 32.83) * mm});
            skLineSegment(sketch, "E2222", {"start": v(-3.63, 32.83) * mm, "end": v(-3.7, 32.96) * mm});
            skLineSegment(sketch, "E2223", {"start": v(-3.7, 32.96) * mm, "end": v(-3.76, 33.08) * mm});
            skLineSegment(sketch, "E2224", {"start": v(-3.76, 33.08) * mm, "end": v(-3.84, 33.21) * mm});
            skLineSegment(sketch, "E2225", {"start": v(-3.84, 33.21) * mm, "end": v(-3.91, 33.35) * mm});
            skLineSegment(sketch, "E2226", {"start": v(-3.91, 33.35) * mm, "end": v(-4, 33.48) * mm});
            skLineSegment(sketch, "E2227", {"start": v(-4, 33.48) * mm, "end": v(-4.08, 33.62) * mm});
            skLineSegment(sketch, "E2228", {"start": v(-4.08, 33.62) * mm, "end": v(-4.17, 33.76) * mm});
            skLineSegment(sketch, "E2229", {"start": v(-4.17, 33.76) * mm, "end": v(-4.26, 33.9) * mm});
            skLineSegment(sketch, "E2230", {"start": v(-4.26, 33.9) * mm, "end": v(-4.35, 34.06) * mm});
            skLineSegment(sketch, "E2231", {"start": v(-4.35, 34.06) * mm, "end": v(-4.45, 34.2) * mm});
            skLineSegment(sketch, "E2232", {"start": v(-4.45, 34.2) * mm, "end": v(-4.56, 34.35) * mm});
            skLineSegment(sketch, "E2233", {"start": v(-4.56, 34.35) * mm, "end": v(-4.67, 34.5) * mm});
            skLineSegment(sketch, "E2234", {"start": v(-4.67, 34.5) * mm, "end": v(-4.77, 34.6) * mm});
            skLineSegment(sketch, "E2235", {"start": v(-4.77, 34.6) * mm, "end": v(-6.23, 34.37) * mm});
            skLineSegment(sketch, "E2236", {"start": v(-6.23, 34.37) * mm, "end": v(-6.3, 34.25) * mm});
            skLineSegment(sketch, "E2237", {"start": v(-6.3, 34.25) * mm, "end": v(-6.35, 34.07) * mm});
            skLineSegment(sketch, "E2238", {"start": v(-6.35, 34.07) * mm, "end": v(-6.4, 33.9) * mm});
            skLineSegment(sketch, "E2239", {"start": v(-6.4, 33.9) * mm, "end": v(-6.45, 33.72) * mm});
            skLineSegment(sketch, "E2240", {"start": v(-6.45, 33.72) * mm, "end": v(-6.5, 33.55) * mm});
            skLineSegment(sketch, "E2241", {"start": v(-6.5, 33.55) * mm, "end": v(-6.54, 33.39) * mm});
            skLineSegment(sketch, "E2242", {"start": v(-6.54, 33.39) * mm, "end": v(-6.58, 33.22) * mm});
            skLineSegment(sketch, "E2243", {"start": v(-6.58, 33.22) * mm, "end": v(-6.62, 33.07) * mm});
            skLineSegment(sketch, "E2244", {"start": v(-6.62, 33.07) * mm, "end": v(-6.65, 32.91) * mm});
            skLineSegment(sketch, "E2245", {"start": v(-6.65, 32.91) * mm, "end": v(-6.68, 32.76) * mm});
            skLineSegment(sketch, "E2246", {"start": v(-6.68, 32.76) * mm, "end": v(-6.71, 32.61) * mm});
            skLineSegment(sketch, "E2247", {"start": v(-6.71, 32.61) * mm, "end": v(-6.74, 32.47) * mm});
            skLineSegment(sketch, "E2248", {"start": v(-6.74, 32.47) * mm, "end": v(-6.76, 32.33) * mm});
            skLineSegment(sketch, "E2249", {"start": v(-6.76, 32.33) * mm, "end": v(-6.79, 32.2) * mm});
            skLineSegment(sketch, "E2250", {"start": v(-6.79, 32.2) * mm, "end": v(-6.8, 32.06) * mm});
            skLineSegment(sketch, "E2251", {"start": v(-6.8, 32.06) * mm, "end": v(-6.82, 31.93) * mm});
            skLineSegment(sketch, "E2252", {"start": v(-6.82, 31.93) * mm, "end": v(-6.84, 31.81) * mm});
            skLineSegment(sketch, "E2253", {"start": v(-6.84, 31.81) * mm, "end": v(-6.85, 31.7) * mm});
            skLineSegment(sketch, "E2254", {"start": v(-6.85, 31.7) * mm, "end": v(-6.86, 31.57) * mm});
            skLineSegment(sketch, "E2255", {"start": v(-6.86, 31.57) * mm, "end": v(-6.87, 31.46) * mm});
            skLineSegment(sketch, "E2256", {"start": v(-6.87, 31.46) * mm, "end": v(-6.88, 31.35) * mm});
            skLineSegment(sketch, "E2257", {"start": v(-6.88, 31.35) * mm, "end": v(-6.89, 31.25) * mm});
            skLineSegment(sketch, "E2258", {"start": v(-6.89, 31.25) * mm, "end": v(-6.9, 31.15) * mm});
            skLineSegment(sketch, "E2259", {"start": v(-6.9, 31.15) * mm, "end": v(-6.9, 31.06) * mm});
            skLineSegment(sketch, "E2260", {"start": v(-6.9, 31.06) * mm, "end": v(-6.9, 30.96) * mm});
            skLineSegment(sketch, "E2261", {"start": v(-6.9, 30.96) * mm, "end": v(-6.9, 30.88) * mm});
            skLineSegment(sketch, "E2262", {"start": v(-6.9, 30.88) * mm, "end": v(-6.9, 30.8) * mm});
            skLineSegment(sketch, "E2263", {"start": v(-6.9, 30.8) * mm, "end": v(-6.9, 30.71) * mm});
            skLineSegment(sketch, "E2264", {"start": v(-6.9, 30.71) * mm, "end": v(-6.9, 30.64) * mm});
            skLineSegment(sketch, "E2265", {"start": v(-6.9, 30.64) * mm, "end": v(-6.9, 30.57) * mm});
            skLineSegment(sketch, "E2266", {"start": v(-6.9, 30.57) * mm, "end": v(-6.9, 30.5) * mm});
            skLineSegment(sketch, "E2267", {"start": v(-6.9, 30.5) * mm, "end": v(-6.9, 30.44) * mm});
            skLineSegment(sketch, "E2268", {"start": v(-6.9, 30.44) * mm, "end": v(-6.9, 30.38) * mm});
            skLineSegment(sketch, "E2269", {"start": v(-6.9, 30.38) * mm, "end": v(-6.89, 30.33) * mm});
            skLineSegment(sketch, "E2270", {"start": v(-6.89, 30.33) * mm, "end": v(-6.88, 30.28) * mm});
            skLineSegment(sketch, "E2271", {"start": v(-6.88, 30.28) * mm, "end": v(-6.88, 30.23) * mm});
            skLineSegment(sketch, "E2272", {"start": v(-6.88, 30.23) * mm, "end": v(-6.87, 30.19) * mm});
            skLineSegment(sketch, "E2273", {"start": v(-6.87, 30.19) * mm, "end": v(-6.87, 30.15) * mm});
            skLineSegment(sketch, "E2274", {"start": v(-6.87, 30.15) * mm, "end": v(-6.87, 30.12) * mm});
            skLineSegment(sketch, "E2275", {"start": v(-6.87, 30.12) * mm, "end": v(-6.86, 30.1) * mm});
            skLineSegment(sketch, "E2276", {"start": v(-6.86, 30.1) * mm, "end": v(-6.86, 30.07) * mm});
            skLineSegment(sketch, "E2277", {"start": v(-6.86, 30.07) * mm, "end": v(-6.85, 30.05) * mm});
            skLineSegment(sketch, "E2278", {"start": v(-6.85, 30.05) * mm, "end": v(-6.85, 30.03) * mm});
            skLineSegment(sketch, "E2279", {"start": v(-6.85, 30.03) * mm, "end": v(-6.85, 30.02) * mm});
            skLineSegment(sketch, "E2280", {"start": v(-6.85, 30.02) * mm, "end": v(-6.85, 30) * mm});
            skLineSegment(sketch, "E2281", {"start": v(-6.85, 30) * mm, "end": v(-6.73, 29.48) * mm});
            skLineSegment(sketch, "E2282", {"start": v(-6.73, 29.48) * mm, "end": v(-8.97, 28.88) * mm});
            skLineSegment(sketch, "E2283", {"start": v(-8.97, 28.88) * mm, "end": v(-9.14, 29.4) * mm});
            skLineSegment(sketch, "E2284", {"start": v(-9.14, 29.4) * mm, "end": v(-9.14, 29.4) * mm});
            skLineSegment(sketch, "E2285", {"start": v(-9.14, 29.4) * mm, "end": v(-9.14, 29.41) * mm});
            skLineSegment(sketch, "E2286", {"start": v(-9.14, 29.41) * mm, "end": v(-9.15, 29.43) * mm});
            skLineSegment(sketch, "E2287", {"start": v(-9.15, 29.43) * mm, "end": v(-9.16, 29.45) * mm});
            skLineSegment(sketch, "E2288", {"start": v(-9.16, 29.45) * mm, "end": v(-9.16, 29.47) * mm});
            skLineSegment(sketch, "E2289", {"start": v(-9.16, 29.47) * mm, "end": v(-9.18, 29.5) * mm});
            skLineSegment(sketch, "E2290", {"start": v(-9.18, 29.5) * mm, "end": v(-9.19, 29.53) * mm});
            skLineSegment(sketch, "E2291", {"start": v(-9.19, 29.53) * mm, "end": v(-9.2, 29.56) * mm});
            skLineSegment(sketch, "E2292", {"start": v(-9.2, 29.56) * mm, "end": v(-9.22, 29.6) * mm});
            skLineSegment(sketch, "E2293", {"start": v(-9.22, 29.6) * mm, "end": v(-9.24, 29.64) * mm});
            skLineSegment(sketch, "E2294", {"start": v(-9.24, 29.64) * mm, "end": v(-9.26, 29.69) * mm});
            skLineSegment(sketch, "E2295", {"start": v(-9.26, 29.69) * mm, "end": v(-9.28, 29.74) * mm});
            skLineSegment(sketch, "E2296", {"start": v(-9.28, 29.74) * mm, "end": v(-9.3, 29.79) * mm});
            skLineSegment(sketch, "E2297", {"start": v(-9.3, 29.79) * mm, "end": v(-9.34, 29.84) * mm});
            skLineSegment(sketch, "E2298", {"start": v(-9.34, 29.84) * mm, "end": v(-9.37, 29.9) * mm});
            skLineSegment(sketch, "E2299", {"start": v(-9.37, 29.9) * mm, "end": v(-9.4, 29.97) * mm});
            skLineSegment(sketch, "E2300", {"start": v(-9.4, 29.97) * mm, "end": v(-9.44, 30.03) * mm});
            skLineSegment(sketch, "E2301", {"start": v(-9.44, 30.03) * mm, "end": v(-9.48, 30.1) * mm});
            skLineSegment(sketch, "E2302", {"start": v(-9.48, 30.1) * mm, "end": v(-9.52, 30.17) * mm});
            skLineSegment(sketch, "E2303", {"start": v(-9.52, 30.17) * mm, "end": v(-9.57, 30.25) * mm});
            skLineSegment(sketch, "E2304", {"start": v(-9.57, 30.25) * mm, "end": v(-9.62, 30.32) * mm});
            skLineSegment(sketch, "E2305", {"start": v(-9.62, 30.32) * mm, "end": v(-9.67, 30.4) * mm});
            skLineSegment(sketch, "E2306", {"start": v(-9.67, 30.4) * mm, "end": v(-9.72, 30.49) * mm});
            skLineSegment(sketch, "E2307", {"start": v(-9.72, 30.49) * mm, "end": v(-9.78, 30.57) * mm});
            skLineSegment(sketch, "E2308", {"start": v(-9.78, 30.57) * mm, "end": v(-9.84, 30.66) * mm});
            skLineSegment(sketch, "E2309", {"start": v(-9.84, 30.66) * mm, "end": v(-9.9, 30.76) * mm});
            skLineSegment(sketch, "E2310", {"start": v(-9.9, 30.76) * mm, "end": v(-9.98, 30.85) * mm});
            skLineSegment(sketch, "E2311", {"start": v(-9.98, 30.85) * mm, "end": v(-10.05, 30.95) * mm});
            skLineSegment(sketch, "E2312", {"start": v(-10.05, 30.95) * mm, "end": v(-10.12, 31.05) * mm});
            skLineSegment(sketch, "E2313", {"start": v(-10.12, 31.05) * mm, "end": v(-10.2, 31.15) * mm});
            skLineSegment(sketch, "E2314", {"start": v(-10.2, 31.15) * mm, "end": v(-10.29, 31.25) * mm});
            skLineSegment(sketch, "E2315", {"start": v(-10.29, 31.25) * mm, "end": v(-10.37, 31.36) * mm});
            skLineSegment(sketch, "E2316", {"start": v(-10.37, 31.36) * mm, "end": v(-10.46, 31.47) * mm});
            skLineSegment(sketch, "E2317", {"start": v(-10.46, 31.47) * mm, "end": v(-10.56, 31.58) * mm});
            skLineSegment(sketch, "E2318", {"start": v(-10.56, 31.58) * mm, "end": v(-10.66, 31.7) * mm});
            skLineSegment(sketch, "E2319", {"start": v(-10.66, 31.7) * mm, "end": v(-10.76, 31.8) * mm});
            skLineSegment(sketch, "E2320", {"start": v(-10.76, 31.8) * mm, "end": v(-10.87, 31.92) * mm});
            skLineSegment(sketch, "E2321", {"start": v(-10.87, 31.92) * mm, "end": v(-10.98, 32.04) * mm});
            skLineSegment(sketch, "E2322", {"start": v(-10.98, 32.04) * mm, "end": v(-11.1, 32.16) * mm});
            skLineSegment(sketch, "E2323", {"start": v(-11.1, 32.16) * mm, "end": v(-11.21, 32.28) * mm});
            skLineSegment(sketch, "E2324", {"start": v(-11.21, 32.28) * mm, "end": v(-11.34, 32.4) * mm});
            skLineSegment(sketch, "E2325", {"start": v(-11.34, 32.4) * mm, "end": v(-11.47, 32.53) * mm});
            skLineSegment(sketch, "E2326", {"start": v(-11.47, 32.53) * mm, "end": v(-11.6, 32.66) * mm});
            skLineSegment(sketch, "E2327", {"start": v(-11.6, 32.66) * mm, "end": v(-11.74, 32.78) * mm});
            skLineSegment(sketch, "E2328", {"start": v(-11.74, 32.78) * mm, "end": v(-11.86, 32.86) * mm});
            skLineSegment(sketch, "E2329", {"start": v(-11.86, 32.86) * mm, "end": v(-13.24, 32.33) * mm});
            skLineSegment(sketch, "E2330", {"start": v(-13.24, 32.33) * mm, "end": v(-13.28, 32.2) * mm});
            skLineSegment(sketch, "E2331", {"start": v(-13.28, 32.2) * mm, "end": v(-13.3, 32) * mm});
            skLineSegment(sketch, "E2332", {"start": v(-13.3, 32) * mm, "end": v(-13.31, 31.82) * mm});
            skLineSegment(sketch, "E2333", {"start": v(-13.31, 31.82) * mm, "end": v(-13.32, 31.64) * mm});
            skLineSegment(sketch, "E2334", {"start": v(-13.32, 31.64) * mm, "end": v(-13.33, 31.47) * mm});
            skLineSegment(sketch, "E2335", {"start": v(-13.33, 31.47) * mm, "end": v(-13.34, 31.3) * mm});
            skLineSegment(sketch, "E2336", {"start": v(-13.34, 31.3) * mm, "end": v(-13.35, 31.13) * mm});
            skLineSegment(sketch, "E2337", {"start": v(-13.35, 31.13) * mm, "end": v(-13.35, 30.97) * mm});
            skLineSegment(sketch, "E2338", {"start": v(-13.35, 30.97) * mm, "end": v(-13.35, 30.8) * mm});
            skLineSegment(sketch, "E2339", {"start": v(-13.35, 30.8) * mm, "end": v(-13.35, 30.65) * mm});
            skLineSegment(sketch, "E2340", {"start": v(-13.35, 30.65) * mm, "end": v(-13.35, 30.5) * mm});
            skLineSegment(sketch, "E2341", {"start": v(-13.35, 30.5) * mm, "end": v(-13.34, 30.36) * mm});
            skLineSegment(sketch, "E2342", {"start": v(-13.34, 30.36) * mm, "end": v(-13.34, 30.22) * mm});
            skLineSegment(sketch, "E2343", {"start": v(-13.34, 30.22) * mm, "end": v(-13.33, 30.08) * mm});
            skLineSegment(sketch, "E2344", {"start": v(-13.33, 30.08) * mm, "end": v(-13.32, 29.95) * mm});
            skLineSegment(sketch, "E2345", {"start": v(-13.32, 29.95) * mm, "end": v(-13.31, 29.82) * mm});
            skLineSegment(sketch, "E2346", {"start": v(-13.31, 29.82) * mm, "end": v(-13.3, 29.7) * mm});
            skLineSegment(sketch, "E2347", {"start": v(-13.3, 29.7) * mm, "end": v(-13.3, 29.57) * mm});
            skLineSegment(sketch, "E2348", {"start": v(-13.3, 29.57) * mm, "end": v(-13.28, 29.46) * mm});
            skLineSegment(sketch, "E2349", {"start": v(-13.28, 29.46) * mm, "end": v(-13.27, 29.35) * mm});
            skLineSegment(sketch, "E2350", {"start": v(-13.27, 29.35) * mm, "end": v(-13.25, 29.24) * mm});
            skLineSegment(sketch, "E2351", {"start": v(-13.25, 29.24) * mm, "end": v(-13.24, 29.14) * mm});
            skLineSegment(sketch, "E2352", {"start": v(-13.24, 29.14) * mm, "end": v(-13.22, 29.04) * mm});
            skLineSegment(sketch, "E2353", {"start": v(-13.22, 29.04) * mm, "end": v(-13.2, 28.94) * mm});
            skLineSegment(sketch, "E2354", {"start": v(-13.2, 28.94) * mm, "end": v(-13.19, 28.85) * mm});
            skLineSegment(sketch, "E2355", {"start": v(-13.19, 28.85) * mm, "end": v(-13.17, 28.77) * mm});
            skLineSegment(sketch, "E2356", {"start": v(-13.17, 28.77) * mm, "end": v(-13.16, 28.68) * mm});
            skLineSegment(sketch, "E2357", {"start": v(-13.16, 28.68) * mm, "end": v(-13.14, 28.6) * mm});
            skLineSegment(sketch, "E2358", {"start": v(-13.14, 28.6) * mm, "end": v(-13.12, 28.53) * mm});
            skLineSegment(sketch, "E2359", {"start": v(-13.12, 28.53) * mm, "end": v(-13.1, 28.46) * mm});
            skLineSegment(sketch, "E2360", {"start": v(-13.1, 28.46) * mm, "end": v(-13.09, 28.4) * mm});
            skLineSegment(sketch, "E2361", {"start": v(-13.09, 28.4) * mm, "end": v(-13.07, 28.34) * mm});
            skLineSegment(sketch, "E2362", {"start": v(-13.07, 28.34) * mm, "end": v(-13.06, 28.28) * mm});
            skLineSegment(sketch, "E2363", {"start": v(-13.06, 28.28) * mm, "end": v(-13.04, 28.23) * mm});
            skLineSegment(sketch, "E2364", {"start": v(-13.04, 28.23) * mm, "end": v(-13.03, 28.18) * mm});
            skLineSegment(sketch, "E2365", {"start": v(-13.03, 28.18) * mm, "end": v(-13.01, 28.14) * mm});
            skLineSegment(sketch, "E2366", {"start": v(-13.01, 28.14) * mm, "end": v(-13, 28.1) * mm});
            skLineSegment(sketch, "E2367", {"start": v(-13, 28.1) * mm, "end": v(-12.99, 28.07) * mm});
            skLineSegment(sketch, "E2368", {"start": v(-12.99, 28.07) * mm, "end": v(-12.98, 28.03) * mm});
            skLineSegment(sketch, "E2369", {"start": v(-12.98, 28.03) * mm, "end": v(-12.97, 28) * mm});
            skLineSegment(sketch, "E2370", {"start": v(-12.97, 28) * mm, "end": v(-12.96, 27.98) * mm});
            skLineSegment(sketch, "E2371", {"start": v(-12.96, 27.98) * mm, "end": v(-12.95, 27.96) * mm});
            skLineSegment(sketch, "E2372", {"start": v(-12.95, 27.96) * mm, "end": v(-12.95, 27.95) * mm});
            skLineSegment(sketch, "E2373", {"start": v(-12.95, 27.95) * mm, "end": v(-12.94, 27.94) * mm});
            skLineSegment(sketch, "E2374", {"start": v(-12.94, 27.94) * mm, "end": v(-12.94, 27.93) * mm});
            skLineSegment(sketch, "E2375", {"start": v(-12.94, 27.93) * mm, "end": v(-12.7, 27.44) * mm});
            skLineSegment(sketch, "E2376", {"start": v(-12.7, 27.44) * mm, "end": v(-14.78, 26.38) * mm});
            skLineSegment(sketch, "E2377", {"start": v(-14.78, 26.38) * mm, "end": v(-15.05, 26.85) * mm});
            skLineSegment(sketch, "E2378", {"start": v(-15.05, 26.85) * mm, "end": v(-15.05, 26.86) * mm});
            skLineSegment(sketch, "E2379", {"start": v(-15.05, 26.86) * mm, "end": v(-15.06, 26.87) * mm});
            skLineSegment(sketch, "E2380", {"start": v(-15.06, 26.87) * mm, "end": v(-15.07, 26.88) * mm});
            skLineSegment(sketch, "E2381", {"start": v(-15.07, 26.88) * mm, "end": v(-15.08, 26.9) * mm});
            skLineSegment(sketch, "E2382", {"start": v(-15.08, 26.9) * mm, "end": v(-15.1, 26.92) * mm});
            skLineSegment(sketch, "E2383", {"start": v(-15.1, 26.92) * mm, "end": v(-15.1, 26.95) * mm});
            skLineSegment(sketch, "E2384", {"start": v(-15.1, 26.95) * mm, "end": v(-15.13, 26.97) * mm});
            skLineSegment(sketch, "E2385", {"start": v(-15.13, 26.97) * mm, "end": v(-15.15, 27) * mm});
            skLineSegment(sketch, "E2386", {"start": v(-15.15, 27) * mm, "end": v(-15.17, 27.04) * mm});
            skLineSegment(sketch, "E2387", {"start": v(-15.17, 27.04) * mm, "end": v(-15.2, 27.07) * mm});
            skLineSegment(sketch, "E2388", {"start": v(-15.2, 27.07) * mm, "end": v(-15.23, 27.11) * mm});
            skLineSegment(sketch, "E2389", {"start": v(-15.23, 27.11) * mm, "end": v(-15.26, 27.16) * mm});
            skLineSegment(sketch, "E2390", {"start": v(-15.26, 27.16) * mm, "end": v(-15.3, 27.2) * mm});
            skLineSegment(sketch, "E2391", {"start": v(-15.3, 27.2) * mm, "end": v(-15.34, 27.25) * mm});
            skLineSegment(sketch, "E2392", {"start": v(-15.34, 27.25) * mm, "end": v(-15.38, 27.3) * mm});
            skLineSegment(sketch, "E2393", {"start": v(-15.38, 27.3) * mm, "end": v(-15.43, 27.36) * mm});
            skLineSegment(sketch, "E2394", {"start": v(-15.43, 27.36) * mm, "end": v(-15.48, 27.41) * mm});
            skLineSegment(sketch, "E2395", {"start": v(-15.48, 27.41) * mm, "end": v(-15.53, 27.47) * mm});
            skLineSegment(sketch, "E2396", {"start": v(-15.53, 27.47) * mm, "end": v(-15.59, 27.53) * mm});
            skLineSegment(sketch, "E2397", {"start": v(-15.59, 27.53) * mm, "end": v(-15.65, 27.6) * mm});
            skLineSegment(sketch, "E2398", {"start": v(-15.65, 27.6) * mm, "end": v(-15.71, 27.66) * mm});
            skLineSegment(sketch, "E2399", {"start": v(-15.71, 27.66) * mm, "end": v(-15.78, 27.73) * mm});
            skLineSegment(sketch, "E2400", {"start": v(-15.78, 27.73) * mm, "end": v(-15.85, 27.8) * mm});
            skLineSegment(sketch, "E2401", {"start": v(-15.85, 27.8) * mm, "end": v(-15.92, 27.87) * mm});
            skLineSegment(sketch, "E2402", {"start": v(-15.92, 27.87) * mm, "end": v(-16, 27.95) * mm});
            skLineSegment(sketch, "E2403", {"start": v(-16, 27.95) * mm, "end": v(-16.09, 28.02) * mm});
            skLineSegment(sketch, "E2404", {"start": v(-16.09, 28.02) * mm, "end": v(-16.17, 28.1) * mm});
            skLineSegment(sketch, "E2405", {"start": v(-16.17, 28.1) * mm, "end": v(-16.26, 28.18) * mm});
            skLineSegment(sketch, "E2406", {"start": v(-16.26, 28.18) * mm, "end": v(-16.36, 28.26) * mm});
            skLineSegment(sketch, "E2407", {"start": v(-16.36, 28.26) * mm, "end": v(-16.46, 28.35) * mm});
            skLineSegment(sketch, "E2408", {"start": v(-16.46, 28.35) * mm, "end": v(-16.56, 28.43) * mm});
            skLineSegment(sketch, "E2409", {"start": v(-16.56, 28.43) * mm, "end": v(-16.67, 28.52) * mm});
            skLineSegment(sketch, "E2410", {"start": v(-16.67, 28.52) * mm, "end": v(-16.78, 28.6) * mm});
            skLineSegment(sketch, "E2411", {"start": v(-16.78, 28.6) * mm, "end": v(-16.9, 28.7) * mm});
            skLineSegment(sketch, "E2412", {"start": v(-16.9, 28.7) * mm, "end": v(-17.01, 28.78) * mm});
            skLineSegment(sketch, "E2413", {"start": v(-17.01, 28.78) * mm, "end": v(-17.14, 28.87) * mm});
            skLineSegment(sketch, "E2414", {"start": v(-17.14, 28.87) * mm, "end": v(-17.27, 28.97) * mm});
            skLineSegment(sketch, "E2415", {"start": v(-17.27, 28.97) * mm, "end": v(-17.4, 29.06) * mm});
            skLineSegment(sketch, "E2416", {"start": v(-17.4, 29.06) * mm, "end": v(-17.54, 29.15) * mm});
            skLineSegment(sketch, "E2417", {"start": v(-17.54, 29.15) * mm, "end": v(-17.68, 29.25) * mm});
            skLineSegment(sketch, "E2418", {"start": v(-17.68, 29.25) * mm, "end": v(-17.83, 29.34) * mm});
            skLineSegment(sketch, "E2419", {"start": v(-17.83, 29.34) * mm, "end": v(-17.98, 29.44) * mm});
            skLineSegment(sketch, "E2420", {"start": v(-17.98, 29.44) * mm, "end": v(-18.14, 29.53) * mm});
            skLineSegment(sketch, "E2421", {"start": v(-18.14, 29.53) * mm, "end": v(-18.3, 29.63) * mm});
            skLineSegment(sketch, "E2422", {"start": v(-18.3, 29.63) * mm, "end": v(-18.43, 29.67) * mm});
            skLineSegment(sketch, "E2423", {"start": v(-18.43, 29.67) * mm, "end": v(-19.67, 28.87) * mm});
            skLineSegment(sketch, "E2424", {"start": v(-19.67, 28.87) * mm, "end": v(-19.68, 28.73) * mm});
            skLineSegment(sketch, "E2425", {"start": v(-19.68, 28.73) * mm, "end": v(-19.66, 28.54) * mm});
            skLineSegment(sketch, "E2426", {"start": v(-19.66, 28.54) * mm, "end": v(-19.64, 28.36) * mm});
            skLineSegment(sketch, "E2427", {"start": v(-19.64, 28.36) * mm, "end": v(-19.61, 28.18) * mm});
            skLineSegment(sketch, "E2428", {"start": v(-19.61, 28.18) * mm, "end": v(-19.58, 28) * mm});
            skLineSegment(sketch, "E2429", {"start": v(-19.58, 28) * mm, "end": v(-19.56, 27.84) * mm});
            skLineSegment(sketch, "E2430", {"start": v(-19.56, 27.84) * mm, "end": v(-19.53, 27.67) * mm});
            skLineSegment(sketch, "E2431", {"start": v(-19.53, 27.67) * mm, "end": v(-19.5, 27.52) * mm});
            skLineSegment(sketch, "E2432", {"start": v(-19.5, 27.52) * mm, "end": v(-19.46, 27.36) * mm});
            skLineSegment(sketch, "E2433", {"start": v(-19.46, 27.36) * mm, "end": v(-19.43, 27.2) * mm});
            skLineSegment(sketch, "E2434", {"start": v(-19.43, 27.2) * mm, "end": v(-19.4, 27.06) * mm});
            skLineSegment(sketch, "E2435", {"start": v(-19.4, 27.06) * mm, "end": v(-19.36, 26.92) * mm});
            skLineSegment(sketch, "E2436", {"start": v(-19.36, 26.92) * mm, "end": v(-19.33, 26.78) * mm});
            skLineSegment(sketch, "E2437", {"start": v(-19.33, 26.78) * mm, "end": v(-19.3, 26.65) * mm});
            skLineSegment(sketch, "E2438", {"start": v(-19.3, 26.65) * mm, "end": v(-19.26, 26.52) * mm});
            skLineSegment(sketch, "E2439", {"start": v(-19.26, 26.52) * mm, "end": v(-19.22, 26.4) * mm});
            skLineSegment(sketch, "E2440", {"start": v(-19.22, 26.4) * mm, "end": v(-19.19, 26.28) * mm});
            skLineSegment(sketch, "E2441", {"start": v(-19.19, 26.28) * mm, "end": v(-19.15, 26.16) * mm});
            skLineSegment(sketch, "E2442", {"start": v(-19.15, 26.16) * mm, "end": v(-19.11, 26.05) * mm});
            skLineSegment(sketch, "E2443", {"start": v(-19.11, 26.05) * mm, "end": v(-19.08, 25.95) * mm});
            skLineSegment(sketch, "E2444", {"start": v(-19.08, 25.95) * mm, "end": v(-19.04, 25.84) * mm});
            skLineSegment(sketch, "E2445", {"start": v(-19.04, 25.84) * mm, "end": v(-19, 25.75) * mm});
            skLineSegment(sketch, "E2446", {"start": v(-19, 25.75) * mm, "end": v(-18.97, 25.65) * mm});
            skLineSegment(sketch, "E2447", {"start": v(-18.97, 25.65) * mm, "end": v(-18.93, 25.56) * mm});
            skLineSegment(sketch, "E2448", {"start": v(-18.93, 25.56) * mm, "end": v(-18.9, 25.48) * mm});
            skLineSegment(sketch, "E2449", {"start": v(-18.9, 25.48) * mm, "end": v(-18.87, 25.4) * mm});
            skLineSegment(sketch, "E2450", {"start": v(-18.87, 25.4) * mm, "end": v(-18.83, 25.32) * mm});
            skLineSegment(sketch, "E2451", {"start": v(-18.83, 25.32) * mm, "end": v(-18.8, 25.25) * mm});
            skLineSegment(sketch, "E2452", {"start": v(-18.8, 25.25) * mm, "end": v(-18.77, 25.18) * mm});
            skLineSegment(sketch, "E2453", {"start": v(-18.77, 25.18) * mm, "end": v(-18.74, 25.12) * mm});
            skLineSegment(sketch, "E2454", {"start": v(-18.74, 25.12) * mm, "end": v(-18.7, 25.06) * mm});
            skLineSegment(sketch, "E2455", {"start": v(-18.7, 25.06) * mm, "end": v(-18.68, 25) * mm});
            skLineSegment(sketch, "E2456", {"start": v(-18.68, 25) * mm, "end": v(-18.65, 24.95) * mm});
            skLineSegment(sketch, "E2457", {"start": v(-18.65, 24.95) * mm, "end": v(-18.63, 24.9) * mm});
            skLineSegment(sketch, "E2458", {"start": v(-18.63, 24.9) * mm, "end": v(-18.6, 24.86) * mm});
            skLineSegment(sketch, "E2459", {"start": v(-18.6, 24.86) * mm, "end": v(-18.58, 24.82) * mm});
            skLineSegment(sketch, "E2460", {"start": v(-18.58, 24.82) * mm, "end": v(-18.56, 24.78) * mm});
            skLineSegment(sketch, "E2461", {"start": v(-18.56, 24.78) * mm, "end": v(-18.54, 24.75) * mm});
            skLineSegment(sketch, "E2462", {"start": v(-18.54, 24.75) * mm, "end": v(-18.52, 24.72) * mm});
            skLineSegment(sketch, "E2463", {"start": v(-18.52, 24.72) * mm, "end": v(-18.5, 24.7) * mm});
            skLineSegment(sketch, "E2464", {"start": v(-18.5, 24.7) * mm, "end": v(-18.5, 24.68) * mm});
            skLineSegment(sketch, "E2465", {"start": v(-18.5, 24.68) * mm, "end": v(-18.48, 24.66) * mm});
            skLineSegment(sketch, "E2466", {"start": v(-18.48, 24.66) * mm, "end": v(-18.47, 24.65) * mm});
            skLineSegment(sketch, "E2467", {"start": v(-18.47, 24.65) * mm, "end": v(-18.47, 24.64) * mm});
            skLineSegment(sketch, "E2468", {"start": v(-18.47, 24.64) * mm, "end": v(-18.46, 24.63) * mm});
            skLineSegment(sketch, "E2469", {"start": v(-18.46, 24.63) * mm, "end": v(-18.14, 24.2) * mm});
            skLineSegment(sketch, "E2470", {"start": v(-18.14, 24.2) * mm, "end": v(-19.94, 22.73) * mm});
            skLineSegment(sketch, "E2471", {"start": v(-19.94, 22.73) * mm, "end": v(-20.3, 23.14) * mm});
            skLineSegment(sketch, "E2472", {"start": v(-20.3, 23.14) * mm, "end": v(-20.3, 23.14) * mm});
            skLineSegment(sketch, "E2473", {"start": v(-20.3, 23.14) * mm, "end": v(-20.31, 23.15) * mm});
            skLineSegment(sketch, "E2474", {"start": v(-20.31, 23.15) * mm, "end": v(-20.33, 23.16) * mm});
            skLineSegment(sketch, "E2475", {"start": v(-20.33, 23.16) * mm, "end": v(-20.34, 23.18) * mm});
            skLineSegment(sketch, "E2476", {"start": v(-20.34, 23.18) * mm, "end": v(-20.36, 23.2) * mm});
            skLineSegment(sketch, "E2477", {"start": v(-20.36, 23.2) * mm, "end": v(-20.38, 23.22) * mm});
            skLineSegment(sketch, "E2478", {"start": v(-20.38, 23.22) * mm, "end": v(-20.4, 23.24) * mm});
            skLineSegment(sketch, "E2479", {"start": v(-20.4, 23.24) * mm, "end": v(-20.43, 23.26) * mm});
            skLineSegment(sketch, "E2480", {"start": v(-20.43, 23.26) * mm, "end": v(-20.46, 23.3) * mm});
            skLineSegment(sketch, "E2481", {"start": v(-20.46, 23.3) * mm, "end": v(-20.5, 23.32) * mm});
            skLineSegment(sketch, "E2482", {"start": v(-20.5, 23.32) * mm, "end": v(-20.53, 23.36) * mm});
            skLineSegment(sketch, "E2483", {"start": v(-20.53, 23.36) * mm, "end": v(-20.58, 23.39) * mm});
            skLineSegment(sketch, "E2484", {"start": v(-20.58, 23.39) * mm, "end": v(-20.62, 23.43) * mm});
            skLineSegment(sketch, "E2485", {"start": v(-20.62, 23.43) * mm, "end": v(-20.67, 23.47) * mm});
            skLineSegment(sketch, "E2486", {"start": v(-20.67, 23.47) * mm, "end": v(-20.72, 23.5) * mm});
            skLineSegment(sketch, "E2487", {"start": v(-20.72, 23.5) * mm, "end": v(-20.78, 23.55) * mm});
            skLineSegment(sketch, "E2488", {"start": v(-20.78, 23.55) * mm, "end": v(-20.84, 23.6) * mm});
            skLineSegment(sketch, "E2489", {"start": v(-20.84, 23.6) * mm, "end": v(-20.9, 23.64) * mm});
            skLineSegment(sketch, "E2490", {"start": v(-20.9, 23.64) * mm, "end": v(-20.97, 23.69) * mm});
            skLineSegment(sketch, "E2491", {"start": v(-20.97, 23.69) * mm, "end": v(-21.04, 23.74) * mm});
            skLineSegment(sketch, "E2492", {"start": v(-21.04, 23.74) * mm, "end": v(-21.12, 23.8) * mm});
            skLineSegment(sketch, "E2493", {"start": v(-21.12, 23.8) * mm, "end": v(-21.2, 23.84) * mm});
            skLineSegment(sketch, "E2494", {"start": v(-21.2, 23.84) * mm, "end": v(-21.28, 23.9) * mm});
            skLineSegment(sketch, "E2495", {"start": v(-21.28, 23.9) * mm, "end": v(-21.37, 23.95) * mm});
            skLineSegment(sketch, "E2496", {"start": v(-21.37, 23.95) * mm, "end": v(-21.46, 24) * mm});
            skLineSegment(sketch, "E2497", {"start": v(-21.46, 24) * mm, "end": v(-21.56, 24.07) * mm});
            skLineSegment(sketch, "E2498", {"start": v(-21.56, 24.07) * mm, "end": v(-21.66, 24.13) * mm});
            skLineSegment(sketch, "E2499", {"start": v(-21.66, 24.13) * mm, "end": v(-21.77, 24.18) * mm});
            skLineSegment(sketch, "E2500", {"start": v(-21.77, 24.18) * mm, "end": v(-21.88, 24.24) * mm});
            skLineSegment(sketch, "E2501", {"start": v(-21.88, 24.24) * mm, "end": v(-21.99, 24.3) * mm});
            skLineSegment(sketch, "E2502", {"start": v(-21.99, 24.3) * mm, "end": v(-22.1, 24.37) * mm});
            skLineSegment(sketch, "E2503", {"start": v(-22.1, 24.37) * mm, "end": v(-22.23, 24.43) * mm});
            skLineSegment(sketch, "E2504", {"start": v(-22.23, 24.43) * mm, "end": v(-22.36, 24.5) * mm});
            skLineSegment(sketch, "E2505", {"start": v(-22.36, 24.5) * mm, "end": v(-22.5, 24.55) * mm});
            skLineSegment(sketch, "E2506", {"start": v(-22.5, 24.55) * mm, "end": v(-22.63, 24.62) * mm});
            skLineSegment(sketch, "E2507", {"start": v(-22.63, 24.62) * mm, "end": v(-22.77, 24.68) * mm});
            skLineSegment(sketch, "E2508", {"start": v(-22.77, 24.68) * mm, "end": v(-22.91, 24.74) * mm});
            skLineSegment(sketch, "E2509", {"start": v(-22.91, 24.74) * mm, "end": v(-23.06, 24.8) * mm});
            skLineSegment(sketch, "E2510", {"start": v(-23.06, 24.8) * mm, "end": v(-23.22, 24.87) * mm});
            skLineSegment(sketch, "E2511", {"start": v(-23.22, 24.87) * mm, "end": v(-23.38, 24.93) * mm});
            skLineSegment(sketch, "E2512", {"start": v(-23.38, 24.93) * mm, "end": v(-23.54, 25) * mm});
            skLineSegment(sketch, "E2513", {"start": v(-23.54, 25) * mm, "end": v(-23.7, 25.05) * mm});
            skLineSegment(sketch, "E2514", {"start": v(-23.7, 25.05) * mm, "end": v(-23.88, 25.11) * mm});
            skLineSegment(sketch, "E2515", {"start": v(-23.88, 25.11) * mm, "end": v(-24.06, 25.17) * mm});
            skLineSegment(sketch, "E2516", {"start": v(-24.06, 25.17) * mm, "end": v(-24.2, 25.2) * mm});
            skLineSegment(sketch, "E2517", {"start": v(-24.2, 25.2) * mm, "end": v(-25.24, 24.15) * mm});
            skLineSegment(sketch, "E2518", {"start": v(-25.24, 24.15) * mm, "end": v(-25.22, 24) * mm});
            skLineSegment(sketch, "E2519", {"start": v(-25.22, 24) * mm, "end": v(-25.16, 23.83) * mm});
            skLineSegment(sketch, "E2520", {"start": v(-25.16, 23.83) * mm, "end": v(-25.1, 23.66) * mm});
            skLineSegment(sketch, "E2521", {"start": v(-25.1, 23.66) * mm, "end": v(-25.04, 23.49) * mm});
            skLineSegment(sketch, "E2522", {"start": v(-25.04, 23.49) * mm, "end": v(-24.98, 23.32) * mm});
            skLineSegment(sketch, "E2523", {"start": v(-24.98, 23.32) * mm, "end": v(-24.92, 23.16) * mm});
            skLineSegment(sketch, "E2524", {"start": v(-24.92, 23.16) * mm, "end": v(-24.85, 23.01) * mm});
            skLineSegment(sketch, "E2525", {"start": v(-24.85, 23.01) * mm, "end": v(-24.79, 22.86) * mm});
            skLineSegment(sketch, "E2526", {"start": v(-24.79, 22.86) * mm, "end": v(-24.73, 22.72) * mm});
            skLineSegment(sketch, "E2527", {"start": v(-24.73, 22.72) * mm, "end": v(-24.66, 22.58) * mm});
            skLineSegment(sketch, "E2528", {"start": v(-24.66, 22.58) * mm, "end": v(-24.6, 22.44) * mm});
            skLineSegment(sketch, "E2529", {"start": v(-24.6, 22.44) * mm, "end": v(-24.54, 22.3) * mm});
            skLineSegment(sketch, "E2530", {"start": v(-24.54, 22.3) * mm, "end": v(-24.48, 22.18) * mm});
            skLineSegment(sketch, "E2531", {"start": v(-24.48, 22.18) * mm, "end": v(-24.41, 22.06) * mm});
            skLineSegment(sketch, "E2532", {"start": v(-24.41, 22.06) * mm, "end": v(-24.35, 21.94) * mm});
            skLineSegment(sketch, "E2533", {"start": v(-24.35, 21.94) * mm, "end": v(-24.3, 21.83) * mm});
            skLineSegment(sketch, "E2534", {"start": v(-24.3, 21.83) * mm, "end": v(-24.23, 21.72) * mm});
            skLineSegment(sketch, "E2535", {"start": v(-24.23, 21.72) * mm, "end": v(-24.17, 21.61) * mm});
            skLineSegment(sketch, "E2536", {"start": v(-24.17, 21.61) * mm, "end": v(-24.11, 21.51) * mm});
            skLineSegment(sketch, "E2537", {"start": v(-24.11, 21.51) * mm, "end": v(-24.05, 21.41) * mm});
            skLineSegment(sketch, "E2538", {"start": v(-24.05, 21.41) * mm, "end": v(-24, 21.32) * mm});
            skLineSegment(sketch, "E2539", {"start": v(-24, 21.32) * mm, "end": v(-23.94, 21.23) * mm});
            skLineSegment(sketch, "E2540", {"start": v(-23.94, 21.23) * mm, "end": v(-23.89, 21.15) * mm});
            skLineSegment(sketch, "E2541", {"start": v(-23.89, 21.15) * mm, "end": v(-23.83, 21.07) * mm});
            skLineSegment(sketch, "E2542", {"start": v(-23.83, 21.07) * mm, "end": v(-23.78, 21) * mm});
            skLineSegment(sketch, "E2543", {"start": v(-23.78, 21) * mm, "end": v(-23.73, 20.92) * mm});
            skLineSegment(sketch, "E2544", {"start": v(-23.73, 20.92) * mm, "end": v(-23.69, 20.85) * mm});
            skLineSegment(sketch, "E2545", {"start": v(-23.69, 20.85) * mm, "end": v(-23.64, 20.79) * mm});
            skLineSegment(sketch, "E2546", {"start": v(-23.64, 20.79) * mm, "end": v(-23.6, 20.73) * mm});
            skLineSegment(sketch, "E2547", {"start": v(-23.6, 20.73) * mm, "end": v(-23.55, 20.67) * mm});
            skLineSegment(sketch, "E2548", {"start": v(-23.55, 20.67) * mm, "end": v(-23.5, 20.62) * mm});
            skLineSegment(sketch, "E2549", {"start": v(-23.5, 20.62) * mm, "end": v(-23.47, 20.57) * mm});
            skLineSegment(sketch, "E2550", {"start": v(-23.47, 20.57) * mm, "end": v(-23.43, 20.53) * mm});
            skLineSegment(sketch, "E2551", {"start": v(-23.43, 20.53) * mm, "end": v(-23.4, 20.49) * mm});
            skLineSegment(sketch, "E2552", {"start": v(-23.4, 20.49) * mm, "end": v(-23.37, 20.45) * mm});
            skLineSegment(sketch, "E2553", {"start": v(-23.37, 20.45) * mm, "end": v(-23.33, 20.41) * mm});
            skLineSegment(sketch, "E2554", {"start": v(-23.33, 20.41) * mm, "end": v(-23.3, 20.38) * mm});
            skLineSegment(sketch, "E2555", {"start": v(-23.3, 20.38) * mm, "end": v(-23.28, 20.36) * mm});
            skLineSegment(sketch, "E2556", {"start": v(-23.28, 20.36) * mm, "end": v(-23.26, 20.33) * mm});
            skLineSegment(sketch, "E2557", {"start": v(-23.26, 20.33) * mm, "end": v(-23.24, 20.31) * mm});
            skLineSegment(sketch, "E2558", {"start": v(-23.24, 20.31) * mm, "end": v(-23.22, 20.3) * mm});
            skLineSegment(sketch, "E2559", {"start": v(-23.22, 20.3) * mm, "end": v(-23.2, 20.28) * mm});
            skLineSegment(sketch, "E2560", {"start": v(-23.2, 20.28) * mm, "end": v(-23.2, 20.27) * mm});
            skLineSegment(sketch, "E2561", {"start": v(-23.2, 20.27) * mm, "end": v(-23.18, 20.26) * mm});
            skLineSegment(sketch, "E2562", {"start": v(-23.18, 20.26) * mm, "end": v(-23.18, 20.25) * mm});
            skLineSegment(sketch, "E2563", {"start": v(-23.18, 20.25) * mm, "end": v(-22.77, 19.9) * mm});
            skLineSegment(sketch, "E2564", {"start": v(-22.77, 19.9) * mm, "end": v(-24.23, 18.09) * mm});
            skLineSegment(sketch, "E2565", {"start": v(-24.23, 18.09) * mm, "end": v(-24.67, 18.4) * mm});
            skLineSegment(sketch, "E2566", {"start": v(-24.67, 18.4) * mm, "end": v(-24.67, 18.41) * mm});
            skLineSegment(sketch, "E2567", {"start": v(-24.67, 18.41) * mm, "end": v(-24.68, 18.42) * mm});
            skLineSegment(sketch, "E2568", {"start": v(-24.68, 18.42) * mm, "end": v(-24.7, 18.43) * mm});
            skLineSegment(sketch, "E2569", {"start": v(-24.7, 18.43) * mm, "end": v(-24.72, 18.44) * mm});
            skLineSegment(sketch, "E2570", {"start": v(-24.72, 18.44) * mm, "end": v(-24.74, 18.46) * mm});
            skLineSegment(sketch, "E2571", {"start": v(-24.74, 18.46) * mm, "end": v(-24.76, 18.47) * mm});
            skLineSegment(sketch, "E2572", {"start": v(-24.76, 18.47) * mm, "end": v(-24.79, 18.49) * mm});
            skLineSegment(sketch, "E2573", {"start": v(-24.79, 18.49) * mm, "end": v(-24.82, 18.5) * mm});
            skLineSegment(sketch, "E2574", {"start": v(-24.82, 18.5) * mm, "end": v(-24.86, 18.53) * mm});
            skLineSegment(sketch, "E2575", {"start": v(-24.86, 18.53) * mm, "end": v(-24.9, 18.55) * mm});
            skLineSegment(sketch, "E2576", {"start": v(-24.9, 18.55) * mm, "end": v(-24.94, 18.58) * mm});
            skLineSegment(sketch, "E2577", {"start": v(-24.94, 18.58) * mm, "end": v(-24.99, 18.6) * mm});
            skLineSegment(sketch, "E2578", {"start": v(-24.99, 18.6) * mm, "end": v(-25.04, 18.63) * mm});
            skLineSegment(sketch, "E2579", {"start": v(-25.04, 18.63) * mm, "end": v(-25.1, 18.66) * mm});
            skLineSegment(sketch, "E2580", {"start": v(-25.1, 18.66) * mm, "end": v(-25.16, 18.69) * mm});
            skLineSegment(sketch, "E2581", {"start": v(-25.16, 18.69) * mm, "end": v(-25.22, 18.72) * mm});
            skLineSegment(sketch, "E2582", {"start": v(-25.22, 18.72) * mm, "end": v(-25.29, 18.75) * mm});
            skLineSegment(sketch, "E2583", {"start": v(-25.29, 18.75) * mm, "end": v(-25.36, 18.78) * mm});
            skLineSegment(sketch, "E2584", {"start": v(-25.36, 18.78) * mm, "end": v(-25.44, 18.81) * mm});
            skLineSegment(sketch, "E2585", {"start": v(-25.44, 18.81) * mm, "end": v(-25.52, 18.85) * mm});
            skLineSegment(sketch, "E2586", {"start": v(-25.52, 18.85) * mm, "end": v(-25.6, 18.88) * mm});
            skLineSegment(sketch, "E2587", {"start": v(-25.6, 18.88) * mm, "end": v(-25.7, 18.92) * mm});
            skLineSegment(sketch, "E2588", {"start": v(-25.7, 18.92) * mm, "end": v(-25.79, 18.95) * mm});
            skLineSegment(sketch, "E2589", {"start": v(-25.79, 18.95) * mm, "end": v(-25.88, 18.99) * mm});
            skLineSegment(sketch, "E2590", {"start": v(-25.88, 18.99) * mm, "end": v(-25.99, 19.02) * mm});
            skLineSegment(sketch, "E2591", {"start": v(-25.99, 19.02) * mm, "end": v(-26.1, 19.06) * mm});
            skLineSegment(sketch, "E2592", {"start": v(-26.1, 19.06) * mm, "end": v(-26.2, 19.1) * mm});
            skLineSegment(sketch, "E2593", {"start": v(-26.2, 19.1) * mm, "end": v(-26.32, 19.13) * mm});
            skLineSegment(sketch, "E2594", {"start": v(-26.32, 19.13) * mm, "end": v(-26.44, 19.17) * mm});
            skLineSegment(sketch, "E2595", {"start": v(-26.44, 19.17) * mm, "end": v(-26.56, 19.2) * mm});
            skLineSegment(sketch, "E2596", {"start": v(-26.56, 19.2) * mm, "end": v(-26.7, 19.24) * mm});
            skLineSegment(sketch, "E2597", {"start": v(-26.7, 19.24) * mm, "end": v(-26.82, 19.27) * mm});
            skLineSegment(sketch, "E2598", {"start": v(-26.82, 19.27) * mm, "end": v(-26.96, 19.3) * mm});
            skLineSegment(sketch, "E2599", {"start": v(-26.96, 19.3) * mm, "end": v(-27.1, 19.34) * mm});
            skLineSegment(sketch, "E2600", {"start": v(-27.1, 19.34) * mm, "end": v(-27.25, 19.37) * mm});
            skLineSegment(sketch, "E2601", {"start": v(-27.25, 19.37) * mm, "end": v(-27.4, 19.4) * mm});
            skLineSegment(sketch, "E2602", {"start": v(-27.4, 19.4) * mm, "end": v(-27.56, 19.44) * mm});
            skLineSegment(sketch, "E2603", {"start": v(-27.56, 19.44) * mm, "end": v(-27.72, 19.47) * mm});
            skLineSegment(sketch, "E2604", {"start": v(-27.72, 19.47) * mm, "end": v(-27.88, 19.5) * mm});
            skLineSegment(sketch, "E2605", {"start": v(-27.88, 19.5) * mm, "end": v(-28.05, 19.53) * mm});
            skLineSegment(sketch, "E2606", {"start": v(-28.05, 19.53) * mm, "end": v(-28.22, 19.55) * mm});
            skLineSegment(sketch, "E2607", {"start": v(-28.22, 19.55) * mm, "end": v(-28.4, 19.58) * mm});
            skLineSegment(sketch, "E2608", {"start": v(-28.4, 19.58) * mm, "end": v(-28.58, 19.6) * mm});
            skLineSegment(sketch, "E2609", {"start": v(-28.58, 19.6) * mm, "end": v(-28.77, 19.62) * mm});
            skLineSegment(sketch, "E2610", {"start": v(-28.77, 19.62) * mm, "end": v(-28.9, 19.61) * mm});
            skLineSegment(sketch, "E2611", {"start": v(-28.9, 19.61) * mm, "end": v(-29.71, 18.37) * mm});
            skLineSegment(sketch, "E2612", {"start": v(-29.71, 18.37) * mm, "end": v(-29.66, 18.24) * mm});
            skLineSegment(sketch, "E2613", {"start": v(-29.66, 18.24) * mm, "end": v(-29.57, 18.08) * mm});
            skLineSegment(sketch, "E2614", {"start": v(-29.57, 18.08) * mm, "end": v(-29.47, 17.92) * mm});
            skLineSegment(sketch, "E2615", {"start": v(-29.47, 17.92) * mm, "end": v(-29.38, 17.77) * mm});
            skLineSegment(sketch, "E2616", {"start": v(-29.38, 17.77) * mm, "end": v(-29.28, 17.62) * mm});
            skLineSegment(sketch, "E2617", {"start": v(-29.28, 17.62) * mm, "end": v(-29.19, 17.48) * mm});
            skLineSegment(sketch, "E2618", {"start": v(-29.19, 17.48) * mm, "end": v(-29.1, 17.34) * mm});
            skLineSegment(sketch, "E2619", {"start": v(-29.1, 17.34) * mm, "end": v(-29, 17.2) * mm});
            skLineSegment(sketch, "E2620", {"start": v(-29, 17.2) * mm, "end": v(-28.9, 17.08) * mm});
            skLineSegment(sketch, "E2621", {"start": v(-28.9, 17.08) * mm, "end": v(-28.82, 16.95) * mm});
            skLineSegment(sketch, "E2622", {"start": v(-28.82, 16.95) * mm, "end": v(-28.73, 16.83) * mm});
            skLineSegment(sketch, "E2623", {"start": v(-28.73, 16.83) * mm, "end": v(-28.64, 16.72) * mm});
            skLineSegment(sketch, "E2624", {"start": v(-28.64, 16.72) * mm, "end": v(-28.55, 16.6) * mm});
            skLineSegment(sketch, "E2625", {"start": v(-28.55, 16.6) * mm, "end": v(-28.47, 16.5) * mm});
            skLineSegment(sketch, "E2626", {"start": v(-28.47, 16.5) * mm, "end": v(-28.38, 16.4) * mm});
            skLineSegment(sketch, "E2627", {"start": v(-28.38, 16.4) * mm, "end": v(-28.3, 16.3) * mm});
            skLineSegment(sketch, "E2628", {"start": v(-28.3, 16.3) * mm, "end": v(-28.22, 16.2) * mm});
            skLineSegment(sketch, "E2629", {"start": v(-28.22, 16.2) * mm, "end": v(-28.14, 16.11) * mm});
            skLineSegment(sketch, "E2630", {"start": v(-28.14, 16.11) * mm, "end": v(-28.06, 16.03) * mm});
            skLineSegment(sketch, "E2631", {"start": v(-28.06, 16.03) * mm, "end": v(-27.98, 15.94) * mm});
            skLineSegment(sketch, "E2632", {"start": v(-27.98, 15.94) * mm, "end": v(-27.9, 15.87) * mm});
            skLineSegment(sketch, "E2633", {"start": v(-27.9, 15.87) * mm, "end": v(-27.83, 15.8) * mm});
            skLineSegment(sketch, "E2634", {"start": v(-27.83, 15.8) * mm, "end": v(-27.76, 15.72) * mm});
            skLineSegment(sketch, "E2635", {"start": v(-27.76, 15.72) * mm, "end": v(-27.7, 15.65) * mm});
            skLineSegment(sketch, "E2636", {"start": v(-27.7, 15.65) * mm, "end": v(-27.63, 15.59) * mm});
            skLineSegment(sketch, "E2637", {"start": v(-27.63, 15.59) * mm, "end": v(-27.56, 15.53) * mm});
            skLineSegment(sketch, "E2638", {"start": v(-27.56, 15.53) * mm, "end": v(-27.5, 15.47) * mm});
            skLineSegment(sketch, "E2639", {"start": v(-27.5, 15.47) * mm, "end": v(-27.44, 15.42) * mm});
            skLineSegment(sketch, "E2640", {"start": v(-27.44, 15.42) * mm, "end": v(-27.39, 15.37) * mm});
            skLineSegment(sketch, "E2641", {"start": v(-27.39, 15.37) * mm, "end": v(-27.33, 15.33) * mm});
            skLineSegment(sketch, "E2642", {"start": v(-27.33, 15.33) * mm, "end": v(-27.28, 15.28) * mm});
            skLineSegment(sketch, "E2643", {"start": v(-27.28, 15.28) * mm, "end": v(-27.23, 15.24) * mm});
            skLineSegment(sketch, "E2644", {"start": v(-27.23, 15.24) * mm, "end": v(-27.19, 15.2) * mm});
            skLineSegment(sketch, "E2645", {"start": v(-27.19, 15.2) * mm, "end": v(-27.15, 15.17) * mm});
            skLineSegment(sketch, "E2646", {"start": v(-27.15, 15.17) * mm, "end": v(-27.1, 15.14) * mm});
            skLineSegment(sketch, "E2647", {"start": v(-27.1, 15.14) * mm, "end": v(-27.07, 15.12) * mm});
            skLineSegment(sketch, "E2648", {"start": v(-27.07, 15.12) * mm, "end": v(-27.04, 15.1) * mm});
            skLineSegment(sketch, "E2649", {"start": v(-27.04, 15.1) * mm, "end": v(-27, 15.07) * mm});
            skLineSegment(sketch, "E2650", {"start": v(-27, 15.07) * mm, "end": v(-26.98, 15.05) * mm});
            skLineSegment(sketch, "E2651", {"start": v(-26.98, 15.05) * mm, "end": v(-26.95, 15.04) * mm});
            skLineSegment(sketch, "E2652", {"start": v(-26.95, 15.04) * mm, "end": v(-26.93, 15.02) * mm});
            skLineSegment(sketch, "E2653", {"start": v(-26.93, 15.02) * mm, "end": v(-26.91, 15.01) * mm});
            skLineSegment(sketch, "E2654", {"start": v(-26.91, 15.01) * mm, "end": v(-26.9, 15) * mm});
            skLineSegment(sketch, "E2655", {"start": v(-26.9, 15) * mm, "end": v(-26.89, 15) * mm});
            skLineSegment(sketch, "E2656", {"start": v(-26.89, 15) * mm, "end": v(-26.88, 15) * mm});
            skLineSegment(sketch, "E2657", {"start": v(-26.88, 15) * mm, "end": v(-26.41, 14.73) * mm});
            skLineSegment(sketch, "E2658", {"start": v(-26.41, 14.73) * mm, "end": v(-27.46, 12.65) * mm});
            skLineSegment(sketch, "E2659", {"start": v(-27.46, 12.65) * mm, "end": v(-27.96, 12.88) * mm});
            skLineSegment(sketch, "E2660", {"start": v(-27.96, 12.88) * mm, "end": v(-27.96, 12.88) * mm});
            skLineSegment(sketch, "E2661", {"start": v(-27.96, 12.88) * mm, "end": v(-27.97, 12.89) * mm});
            skLineSegment(sketch, "E2662", {"start": v(-27.97, 12.89) * mm, "end": v(-28, 12.9) * mm});
            skLineSegment(sketch, "E2663", {"start": v(-28, 12.9) * mm, "end": v(-28, 12.9) * mm});
            skLineSegment(sketch, "E2664", {"start": v(-28, 12.9) * mm, "end": v(-28.03, 12.9) * mm});
            skLineSegment(sketch, "E2665", {"start": v(-28.03, 12.9) * mm, "end": v(-28.06, 12.92) * mm});
            skLineSegment(sketch, "E2666", {"start": v(-28.06, 12.92) * mm, "end": v(-28.1, 12.93) * mm});
            skLineSegment(sketch, "E2667", {"start": v(-28.1, 12.93) * mm, "end": v(-28.13, 12.94) * mm});
            skLineSegment(sketch, "E2668", {"start": v(-28.13, 12.94) * mm, "end": v(-28.17, 12.96) * mm});
            skLineSegment(sketch, "E2669", {"start": v(-28.17, 12.96) * mm, "end": v(-28.21, 12.97) * mm});
            skLineSegment(sketch, "E2670", {"start": v(-28.21, 12.97) * mm, "end": v(-28.26, 12.98) * mm});
            skLineSegment(sketch, "E2671", {"start": v(-28.26, 12.98) * mm, "end": v(-28.31, 13) * mm});
            skLineSegment(sketch, "E2672", {"start": v(-28.31, 13) * mm, "end": v(-28.37, 13.01) * mm});
            skLineSegment(sketch, "E2673", {"start": v(-28.37, 13.01) * mm, "end": v(-28.43, 13.03) * mm});
            skLineSegment(sketch, "E2674", {"start": v(-28.43, 13.03) * mm, "end": v(-28.5, 13.05) * mm});
            skLineSegment(sketch, "E2675", {"start": v(-28.5, 13.05) * mm, "end": v(-28.56, 13.06) * mm});
            skLineSegment(sketch, "E2676", {"start": v(-28.56, 13.06) * mm, "end": v(-28.63, 13.08) * mm});
            skLineSegment(sketch, "E2677", {"start": v(-28.63, 13.08) * mm, "end": v(-28.71, 13.1) * mm});
            skLineSegment(sketch, "E2678", {"start": v(-28.71, 13.1) * mm, "end": v(-28.8, 13.11) * mm});
            skLineSegment(sketch, "E2679", {"start": v(-28.8, 13.11) * mm, "end": v(-28.88, 13.13) * mm});
            skLineSegment(sketch, "E2680", {"start": v(-28.88, 13.13) * mm, "end": v(-28.97, 13.14) * mm});
            skLineSegment(sketch, "E2681", {"start": v(-28.97, 13.14) * mm, "end": v(-29.06, 13.16) * mm});
            skLineSegment(sketch, "E2682", {"start": v(-29.06, 13.16) * mm, "end": v(-29.16, 13.18) * mm});
            skLineSegment(sketch, "E2683", {"start": v(-29.16, 13.18) * mm, "end": v(-29.27, 13.19) * mm});
            skLineSegment(sketch, "E2684", {"start": v(-29.27, 13.19) * mm, "end": v(-29.37, 13.2) * mm});
            skLineSegment(sketch, "E2685", {"start": v(-29.37, 13.2) * mm, "end": v(-29.49, 13.22) * mm});
            skLineSegment(sketch, "E2686", {"start": v(-29.49, 13.22) * mm, "end": v(-29.6, 13.23) * mm});
            skLineSegment(sketch, "E2687", {"start": v(-29.6, 13.23) * mm, "end": v(-29.72, 13.24) * mm});
            skLineSegment(sketch, "E2688", {"start": v(-29.72, 13.24) * mm, "end": v(-29.85, 13.25) * mm});
            skLineSegment(sketch, "E2689", {"start": v(-29.85, 13.25) * mm, "end": v(-29.97, 13.26) * mm});
            skLineSegment(sketch, "E2690", {"start": v(-29.97, 13.26) * mm, "end": v(-30.1, 13.27) * mm});
            skLineSegment(sketch, "E2691", {"start": v(-30.1, 13.27) * mm, "end": v(-30.25, 13.27) * mm});
            skLineSegment(sketch, "E2692", {"start": v(-30.25, 13.27) * mm, "end": v(-30.39, 13.28) * mm});
            skLineSegment(sketch, "E2693", {"start": v(-30.39, 13.28) * mm, "end": v(-30.53, 13.28) * mm});
            skLineSegment(sketch, "E2694", {"start": v(-30.53, 13.28) * mm, "end": v(-30.68, 13.29) * mm});
            skLineSegment(sketch, "E2695", {"start": v(-30.68, 13.29) * mm, "end": v(-30.84, 13.29) * mm});
            skLineSegment(sketch, "E2696", {"start": v(-30.84, 13.29) * mm, "end": v(-31, 13.28) * mm});
            skLineSegment(sketch, "E2697", {"start": v(-31, 13.28) * mm, "end": v(-31.16, 13.28) * mm});
            skLineSegment(sketch, "E2698", {"start": v(-31.16, 13.28) * mm, "end": v(-31.32, 13.27) * mm});
            skLineSegment(sketch, "E2699", {"start": v(-31.32, 13.27) * mm, "end": v(-31.5, 13.27) * mm});
            skLineSegment(sketch, "E2700", {"start": v(-31.5, 13.27) * mm, "end": v(-31.67, 13.26) * mm});
            skLineSegment(sketch, "E2701", {"start": v(-31.67, 13.26) * mm, "end": v(-31.85, 13.24) * mm});
            skLineSegment(sketch, "E2702", {"start": v(-31.85, 13.24) * mm, "end": v(-32.03, 13.23) * mm});
            skLineSegment(sketch, "E2703", {"start": v(-32.03, 13.23) * mm, "end": v(-32.22, 13.21) * mm});
            skLineSegment(sketch, "E2704", {"start": v(-32.22, 13.21) * mm, "end": v(-32.36, 13.17) * mm});
            skLineSegment(sketch, "E2705", {"start": v(-32.36, 13.17) * mm, "end": v(-32.88, 11.8) * mm});
            skLineSegment(sketch, "E2706", {"start": v(-32.88, 11.8) * mm, "end": v(-32.8, 11.67) * mm});
            skLineSegment(sketch, "E2707", {"start": v(-32.8, 11.67) * mm, "end": v(-32.68, 11.53) * mm});
            skLineSegment(sketch, "E2708", {"start": v(-32.68, 11.53) * mm, "end": v(-32.55, 11.4) * mm});
            skLineSegment(sketch, "E2709", {"start": v(-32.55, 11.4) * mm, "end": v(-32.43, 11.27) * mm});
            skLineSegment(sketch, "E2710", {"start": v(-32.43, 11.27) * mm, "end": v(-32.3, 11.15) * mm});
            skLineSegment(sketch, "E2711", {"start": v(-32.3, 11.15) * mm, "end": v(-32.18, 11.03) * mm});
            skLineSegment(sketch, "E2712", {"start": v(-32.18, 11.03) * mm, "end": v(-32.06, 10.91) * mm});
            skLineSegment(sketch, "E2713", {"start": v(-32.06, 10.91) * mm, "end": v(-31.95, 10.8) * mm});
            skLineSegment(sketch, "E2714", {"start": v(-31.95, 10.8) * mm, "end": v(-31.83, 10.7) * mm});
            skLineSegment(sketch, "E2715", {"start": v(-31.83, 10.7) * mm, "end": v(-31.71, 10.6) * mm});
            skLineSegment(sketch, "E2716", {"start": v(-31.71, 10.6) * mm, "end": v(-31.6, 10.5) * mm});
            skLineSegment(sketch, "E2717", {"start": v(-31.6, 10.5) * mm, "end": v(-31.49, 10.4) * mm});
            skLineSegment(sketch, "E2718", {"start": v(-31.49, 10.4) * mm, "end": v(-31.38, 10.3) * mm});
            skLineSegment(sketch, "E2719", {"start": v(-31.38, 10.3) * mm, "end": v(-31.27, 10.22) * mm});
            skLineSegment(sketch, "E2720", {"start": v(-31.27, 10.22) * mm, "end": v(-31.17, 10.14) * mm});
            skLineSegment(sketch, "E2721", {"start": v(-31.17, 10.14) * mm, "end": v(-31.07, 10.06) * mm});
            skLineSegment(sketch, "E2722", {"start": v(-31.07, 10.06) * mm, "end": v(-30.97, 9.98) * mm});
            skLineSegment(sketch, "E2723", {"start": v(-30.97, 9.98) * mm, "end": v(-30.87, 9.91) * mm});
            skLineSegment(sketch, "E2724", {"start": v(-30.87, 9.91) * mm, "end": v(-30.78, 9.84) * mm});
            skLineSegment(sketch, "E2725", {"start": v(-30.78, 9.84) * mm, "end": v(-30.68, 9.78) * mm});
            skLineSegment(sketch, "E2726", {"start": v(-30.68, 9.78) * mm, "end": v(-30.6, 9.72) * mm});
            skLineSegment(sketch, "E2727", {"start": v(-30.6, 9.72) * mm, "end": v(-30.5, 9.66) * mm});
            skLineSegment(sketch, "E2728", {"start": v(-30.5, 9.66) * mm, "end": v(-30.42, 9.6) * mm});
            skLineSegment(sketch, "E2729", {"start": v(-30.42, 9.6) * mm, "end": v(-30.34, 9.55) * mm});
            skLineSegment(sketch, "E2730", {"start": v(-30.34, 9.55) * mm, "end": v(-30.27, 9.5) * mm});
            skLineSegment(sketch, "E2731", {"start": v(-30.27, 9.5) * mm, "end": v(-30.2, 9.46) * mm});
            skLineSegment(sketch, "E2732", {"start": v(-30.2, 9.46) * mm, "end": v(-30.12, 9.42) * mm});
            skLineSegment(sketch, "E2733", {"start": v(-30.12, 9.42) * mm, "end": v(-30.05, 9.38) * mm});
            skLineSegment(sketch, "E2734", {"start": v(-30.05, 9.38) * mm, "end": v(-29.99, 9.34) * mm});
            skLineSegment(sketch, "E2735", {"start": v(-29.99, 9.34) * mm, "end": v(-29.92, 9.3) * mm});
            skLineSegment(sketch, "E2736", {"start": v(-29.92, 9.3) * mm, "end": v(-29.86, 9.28) * mm});
            skLineSegment(sketch, "E2737", {"start": v(-29.86, 9.28) * mm, "end": v(-29.8, 9.25) * mm});
            skLineSegment(sketch, "E2738", {"start": v(-29.8, 9.25) * mm, "end": v(-29.76, 9.22) * mm});
            skLineSegment(sketch, "E2739", {"start": v(-29.76, 9.22) * mm, "end": v(-29.7, 9.2) * mm});
            skLineSegment(sketch, "E2740", {"start": v(-29.7, 9.2) * mm, "end": v(-29.66, 9.18) * mm});
            skLineSegment(sketch, "E2741", {"start": v(-29.66, 9.18) * mm, "end": v(-29.62, 9.16) * mm});
            skLineSegment(sketch, "E2742", {"start": v(-29.62, 9.16) * mm, "end": v(-29.58, 9.14) * mm});
            skLineSegment(sketch, "E2743", {"start": v(-29.58, 9.14) * mm, "end": v(-29.55, 9.13) * mm});
            skLineSegment(sketch, "E2744", {"start": v(-29.55, 9.13) * mm, "end": v(-29.52, 9.11) * mm});
            skLineSegment(sketch, "E2745", {"start": v(-29.52, 9.11) * mm, "end": v(-29.49, 9.1) * mm});
            skLineSegment(sketch, "E2746", {"start": v(-29.49, 9.1) * mm, "end": v(-29.47, 9.1) * mm});
            skLineSegment(sketch, "E2747", {"start": v(-29.47, 9.1) * mm, "end": v(-29.45, 9.09) * mm});
            skLineSegment(sketch, "E2748", {"start": v(-29.45, 9.09) * mm, "end": v(-29.43, 9.08) * mm});
            skLineSegment(sketch, "E2749", {"start": v(-29.43, 9.08) * mm, "end": v(-29.42, 9.08) * mm});
            skLineSegment(sketch, "E2750", {"start": v(-29.42, 9.08) * mm, "end": v(-29.41, 9.07) * mm});
            skLineSegment(sketch, "E2751", {"start": v(-29.41, 9.07) * mm, "end": v(-28.9, 8.91) * mm});
            skLineSegment(sketch, "E2752", {"start": v(-28.9, 8.91) * mm, "end": v(-29.5, 6.67) * mm});
            skLineSegment(sketch, "E2753", {"start": v(-29.5, 6.67) * mm, "end": v(-30.02, 6.78) * mm});
            skLineSegment(sketch, "E2754", {"start": v(-30.02, 6.78) * mm, "end": v(-30.03, 6.79) * mm});
            skLineSegment(sketch, "E2755", {"start": v(-30.03, 6.79) * mm, "end": v(-30.04, 6.79) * mm});
            skLineSegment(sketch, "E2756", {"start": v(-30.04, 6.79) * mm, "end": v(-30.06, 6.8) * mm});
            skLineSegment(sketch, "E2757", {"start": v(-30.06, 6.8) * mm, "end": v(-30.08, 6.8) * mm});
            skLineSegment(sketch, "E2758", {"start": v(-30.08, 6.8) * mm, "end": v(-30.1, 6.8) * mm});
            skLineSegment(sketch, "E2759", {"start": v(-30.1, 6.8) * mm, "end": v(-30.13, 6.8) * mm});
            skLineSegment(sketch, "E2760", {"start": v(-30.13, 6.8) * mm, "end": v(-30.17, 6.8) * mm});
            skLineSegment(sketch, "E2761", {"start": v(-30.17, 6.8) * mm, "end": v(-30.2, 6.81) * mm});
            skLineSegment(sketch, "E2762", {"start": v(-30.2, 6.81) * mm, "end": v(-30.25, 6.82) * mm});
            skLineSegment(sketch, "E2763", {"start": v(-30.25, 6.82) * mm, "end": v(-30.3, 6.82) * mm});
            skLineSegment(sketch, "E2764", {"start": v(-30.3, 6.82) * mm, "end": v(-30.34, 6.82) * mm});
            skLineSegment(sketch, "E2765", {"start": v(-30.34, 6.82) * mm, "end": v(-30.4, 6.83) * mm});
            skLineSegment(sketch, "E2766", {"start": v(-30.4, 6.83) * mm, "end": v(-30.45, 6.83) * mm});
            skLineSegment(sketch, "E2767", {"start": v(-30.45, 6.83) * mm, "end": v(-30.52, 6.83) * mm});
            skLineSegment(sketch, "E2768", {"start": v(-30.52, 6.83) * mm, "end": v(-30.58, 6.84) * mm});
            skLineSegment(sketch, "E2769", {"start": v(-30.58, 6.84) * mm, "end": v(-30.65, 6.84) * mm});
            skLineSegment(sketch, "E2770", {"start": v(-30.65, 6.84) * mm, "end": v(-30.73, 6.84) * mm});
            skLineSegment(sketch, "E2771", {"start": v(-30.73, 6.84) * mm, "end": v(-30.8, 6.84) * mm});
            skLineSegment(sketch, "E2772", {"start": v(-30.8, 6.84) * mm, "end": v(-30.9, 6.84) * mm});
            skLineSegment(sketch, "E2773", {"start": v(-30.9, 6.84) * mm, "end": v(-30.98, 6.84) * mm});
            skLineSegment(sketch, "E2774", {"start": v(-30.98, 6.84) * mm, "end": v(-31.07, 6.83) * mm});
            skLineSegment(sketch, "E2775", {"start": v(-31.07, 6.83) * mm, "end": v(-31.17, 6.83) * mm});
            skLineSegment(sketch, "E2776", {"start": v(-31.17, 6.83) * mm, "end": v(-31.26, 6.82) * mm});
            skLineSegment(sketch, "E2777", {"start": v(-31.26, 6.82) * mm, "end": v(-31.37, 6.82) * mm});
            skLineSegment(sketch, "E2778", {"start": v(-31.37, 6.82) * mm, "end": v(-31.48, 6.8) * mm});
            skLineSegment(sketch, "E2779", {"start": v(-31.48, 6.8) * mm, "end": v(-31.59, 6.8) * mm});
            skLineSegment(sketch, "E2780", {"start": v(-31.59, 6.8) * mm, "end": v(-31.7, 6.79) * mm});
            skLineSegment(sketch, "E2781", {"start": v(-31.7, 6.79) * mm, "end": v(-31.82, 6.77) * mm});
            skLineSegment(sketch, "E2782", {"start": v(-31.82, 6.77) * mm, "end": v(-31.95, 6.76) * mm});
            skLineSegment(sketch, "E2783", {"start": v(-31.95, 6.76) * mm, "end": v(-32.08, 6.74) * mm});
            skLineSegment(sketch, "E2784", {"start": v(-32.08, 6.74) * mm, "end": v(-32.2, 6.72) * mm});
            skLineSegment(sketch, "E2785", {"start": v(-32.2, 6.72) * mm, "end": v(-32.34, 6.7) * mm});
            skLineSegment(sketch, "E2786", {"start": v(-32.34, 6.7) * mm, "end": v(-32.48, 6.67) * mm});
            skLineSegment(sketch, "E2787", {"start": v(-32.48, 6.67) * mm, "end": v(-32.63, 6.65) * mm});
            skLineSegment(sketch, "E2788", {"start": v(-32.63, 6.65) * mm, "end": v(-32.77, 6.62) * mm});
            skLineSegment(sketch, "E2789", {"start": v(-32.77, 6.62) * mm, "end": v(-32.93, 6.58) * mm});
            skLineSegment(sketch, "E2790", {"start": v(-32.93, 6.58) * mm, "end": v(-33.08, 6.55) * mm});
            skLineSegment(sketch, "E2791", {"start": v(-33.08, 6.55) * mm, "end": v(-33.24, 6.51) * mm});
            skLineSegment(sketch, "E2792", {"start": v(-33.24, 6.51) * mm, "end": v(-33.4, 6.47) * mm});
            skLineSegment(sketch, "E2793", {"start": v(-33.4, 6.47) * mm, "end": v(-33.56, 6.43) * mm});
            skLineSegment(sketch, "E2794", {"start": v(-33.56, 6.43) * mm, "end": v(-33.73, 6.38) * mm});
            skLineSegment(sketch, "E2795", {"start": v(-33.73, 6.38) * mm, "end": v(-33.9, 6.33) * mm});
            skLineSegment(sketch, "E2796", {"start": v(-33.9, 6.33) * mm, "end": v(-34.08, 6.28) * mm});
            skLineSegment(sketch, "E2797", {"start": v(-34.08, 6.28) * mm, "end": v(-34.26, 6.23) * mm});
            skLineSegment(sketch, "E2798", {"start": v(-34.26, 6.23) * mm, "end": v(-34.39, 6.16) * mm});
            skLineSegment(sketch, "E2799", {"start": v(-34.39, 6.16) * mm, "end": v(-34.62, 4.7) * mm});
            skLineSegment(sketch, "E2800", {"start": v(-34.62, 4.7) * mm, "end": v(-34.52, 4.6) * mm});
            skLineSegment(sketch, "E2801", {"start": v(-34.52, 4.6) * mm, "end": v(-34.36, 4.49) * mm});
            skLineSegment(sketch, "E2802", {"start": v(-34.36, 4.49) * mm, "end": v(-34.21, 4.38) * mm});
            skLineSegment(sketch, "E2803", {"start": v(-34.21, 4.38) * mm, "end": v(-34.06, 4.28) * mm});
            skLineSegment(sketch, "E2804", {"start": v(-34.06, 4.28) * mm, "end": v(-33.92, 4.19) * mm});
            skLineSegment(sketch, "E2805", {"start": v(-33.92, 4.19) * mm, "end": v(-33.77, 4.1) * mm});
            skLineSegment(sketch, "E2806", {"start": v(-33.77, 4.1) * mm, "end": v(-33.63, 4) * mm});
            skLineSegment(sketch, "E2807", {"start": v(-33.63, 4) * mm, "end": v(-33.5, 3.92) * mm});
            skLineSegment(sketch, "E2808", {"start": v(-33.5, 3.92) * mm, "end": v(-33.36, 3.84) * mm});
            skLineSegment(sketch, "E2809", {"start": v(-33.36, 3.84) * mm, "end": v(-33.22, 3.77) * mm});
            skLineSegment(sketch, "E2810", {"start": v(-33.22, 3.77) * mm, "end": v(-33.1, 3.7) * mm});
            skLineSegment(sketch, "E2811", {"start": v(-33.1, 3.7) * mm, "end": v(-32.96, 3.62) * mm});
            skLineSegment(sketch, "E2812", {"start": v(-32.96, 3.62) * mm, "end": v(-32.84, 3.56) * mm});
            skLineSegment(sketch, "E2813", {"start": v(-32.84, 3.56) * mm, "end": v(-32.72, 3.5) * mm});
            skLineSegment(sketch, "E2814", {"start": v(-32.72, 3.5) * mm, "end": v(-32.6, 3.44) * mm});
            skLineSegment(sketch, "E2815", {"start": v(-32.6, 3.44) * mm, "end": v(-32.48, 3.38) * mm});
            skLineSegment(sketch, "E2816", {"start": v(-32.48, 3.38) * mm, "end": v(-32.37, 3.33) * mm});
            skLineSegment(sketch, "E2817", {"start": v(-32.37, 3.33) * mm, "end": v(-32.26, 3.28) * mm});
            skLineSegment(sketch, "E2818", {"start": v(-32.26, 3.28) * mm, "end": v(-32.15, 3.23) * mm});
            skLineSegment(sketch, "E2819", {"start": v(-32.15, 3.23) * mm, "end": v(-32.05, 3.19) * mm});
            skLineSegment(sketch, "E2820", {"start": v(-32.05, 3.19) * mm, "end": v(-31.95, 3.14) * mm});
            skLineSegment(sketch, "E2821", {"start": v(-31.95, 3.14) * mm, "end": v(-31.85, 3.1) * mm});
            skLineSegment(sketch, "E2822", {"start": v(-31.85, 3.1) * mm, "end": v(-31.76, 3.07) * mm});
            skLineSegment(sketch, "E2823", {"start": v(-31.76, 3.07) * mm, "end": v(-31.67, 3.04) * mm});
            skLineSegment(sketch, "E2824", {"start": v(-31.67, 3.04) * mm, "end": v(-31.58, 3) * mm});
            skLineSegment(sketch, "E2825", {"start": v(-31.58, 3) * mm, "end": v(-31.5, 2.98) * mm});
            skLineSegment(sketch, "E2826", {"start": v(-31.5, 2.98) * mm, "end": v(-31.42, 2.95) * mm});
            skLineSegment(sketch, "E2827", {"start": v(-31.42, 2.95) * mm, "end": v(-31.34, 2.92) * mm});
            skLineSegment(sketch, "E2828", {"start": v(-31.34, 2.92) * mm, "end": v(-31.27, 2.9) * mm});
            skLineSegment(sketch, "E2829", {"start": v(-31.27, 2.9) * mm, "end": v(-31.2, 2.88) * mm});
            skLineSegment(sketch, "E2830", {"start": v(-31.2, 2.88) * mm, "end": v(-31.14, 2.86) * mm});
            skLineSegment(sketch, "E2831", {"start": v(-31.14, 2.86) * mm, "end": v(-31.08, 2.85) * mm});
            skLineSegment(sketch, "E2832", {"start": v(-31.08, 2.85) * mm, "end": v(-31.02, 2.83) * mm});
            skLineSegment(sketch, "E2833", {"start": v(-31.02, 2.83) * mm, "end": v(-30.97, 2.82) * mm});
            skLineSegment(sketch, "E2834", {"start": v(-30.97, 2.82) * mm, "end": v(-30.92, 2.8) * mm});
            skLineSegment(sketch, "E2835", {"start": v(-30.92, 2.8) * mm, "end": v(-30.88, 2.8) * mm});
            skLineSegment(sketch, "E2836", {"start": v(-30.88, 2.8) * mm, "end": v(-30.84, 2.8) * mm});
            skLineSegment(sketch, "E2837", {"start": v(-30.84, 2.8) * mm, "end": v(-30.8, 2.78) * mm});
            skLineSegment(sketch, "E2838", {"start": v(-30.8, 2.78) * mm, "end": v(-30.77, 2.78) * mm});
            skLineSegment(sketch, "E2839", {"start": v(-30.77, 2.78) * mm, "end": v(-30.74, 2.77) * mm});
            skLineSegment(sketch, "E2840", {"start": v(-30.74, 2.77) * mm, "end": v(-30.71, 2.77) * mm});
            skLineSegment(sketch, "E2841", {"start": v(-30.71, 2.77) * mm, "end": v(-30.7, 2.77) * mm});
            skLineSegment(sketch, "E2842", {"start": v(-30.7, 2.77) * mm, "end": v(-30.68, 2.76) * mm});
            skLineSegment(sketch, "E2843", {"start": v(-30.68, 2.76) * mm, "end": v(-30.66, 2.76) * mm});
            skLineSegment(sketch, "E2844", {"start": v(-30.66, 2.76) * mm, "end": v(-30.66, 2.76) * mm});
            skLineSegment(sketch, "E2845", {"start": v(-30.66, 2.76) * mm, "end": v(-30.12, 2.71) * mm});
            skLineSegment(sketch, "E2846", {"start": v(-30.12, 2.71) * mm, "end": v(-30.24, 0.39) * mm});
            skLineSegment(sketch, "E2847", {"start": v(-26.28, 13.82) * mm, "end": v(-26.4, 13.52) * mm});
            skLineSegment(sketch, "E2848", {"start": v(-26.4, 13.52) * mm, "end": v(-26.53, 13.22) * mm});
            skLineSegment(sketch, "E2849", {"start": v(-26.53, 13.22) * mm, "end": v(-26.65, 12.9) * mm});
            skArc(sketch, "E2850", {"start": v(6, 0.1) * mm, "mid": v(5.74, 1.78) * mm, "end": v(5, 3.32) * mm});
            skArc(sketch, "E2851", {"start": v(1.95, -5.68) * mm, "mid": v(3.47, -4.9) * mm, "end": v(4.7, -3.74) * mm});
            skArc(sketch, "E2852", {"start": v(-4.8, -3.61) * mm, "mid": v(-3.6, -4.82) * mm, "end": v(-2.1, -5.63) * mm});
            skArc(sketch, "E2853", {"start": v(-4.92, 3.45) * mm, "mid": v(-5.7, 1.93) * mm, "end": v(-6, 0.26) * mm});
            skArc(sketch, "E2854", {"start": v(1.76, 5.75) * mm, "mid": v(0.08, 6) * mm, "end": v(-1.61, 5.79) * mm});
            skSolve(sketch);
        }
        {
            var Q0;
            Q0 = qSketchRegion(id + "F0", true);
            extrude(context, id + "F1", {"entities" : qUnion([Q0]), "depth" : 8 * mm, "offsetDistance" : 25 * mm});
        }
    });
